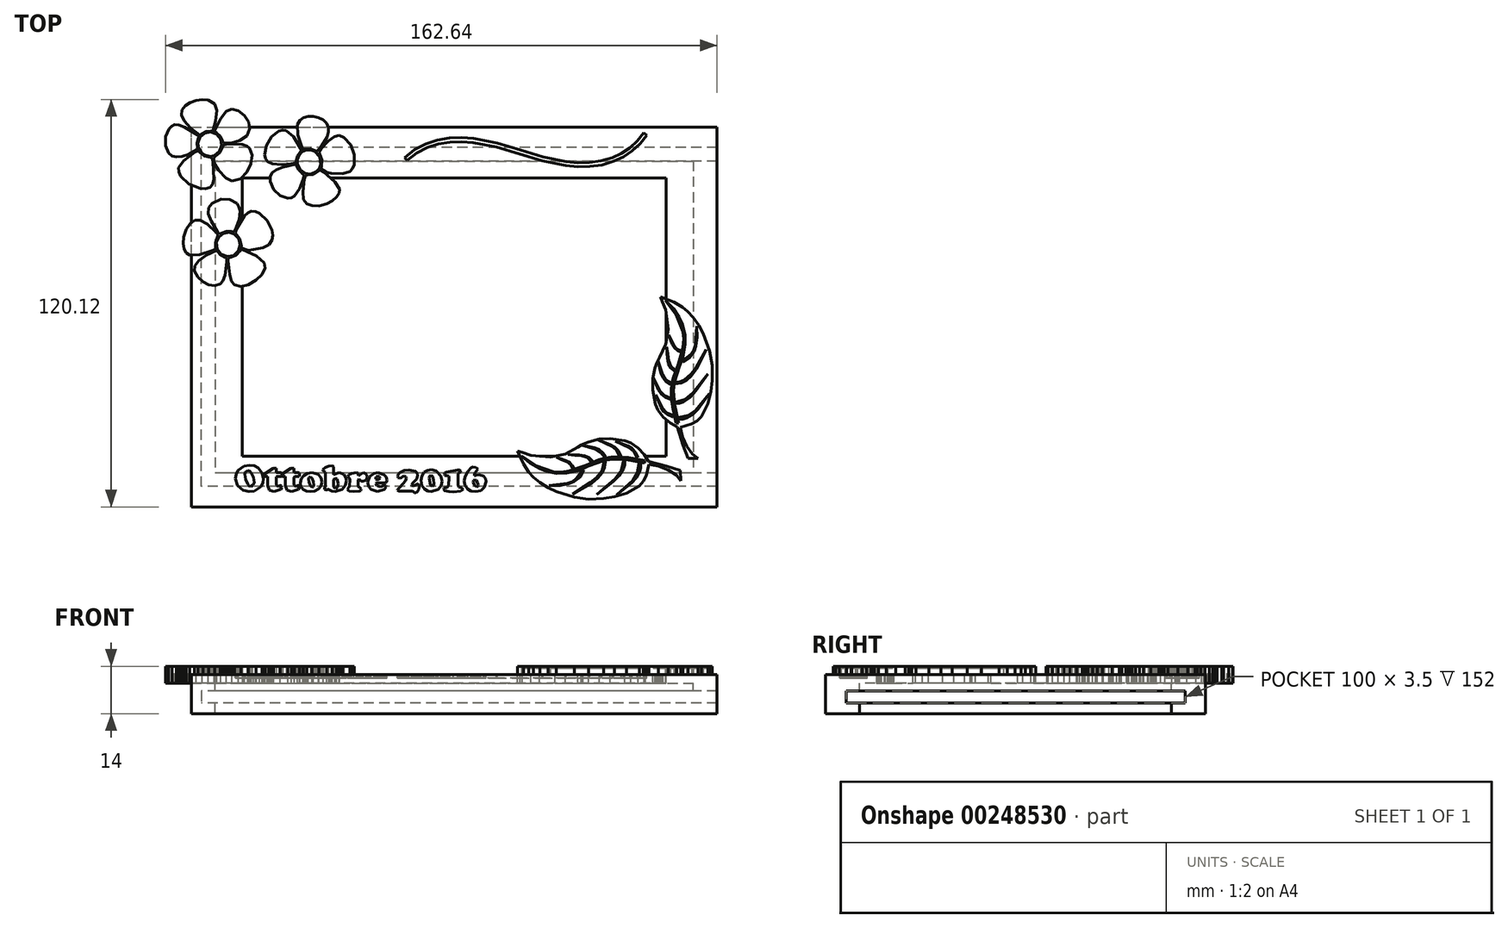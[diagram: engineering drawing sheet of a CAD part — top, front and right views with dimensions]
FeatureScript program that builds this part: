
annotation { "Feature Type Name" : "Feature", "Feature Type Description" : "" }
export const myFeature = defineFeature(function(context is Context, id is Id, definition is map)
    precondition{}
    {
        {
            var Q0;
            Q0=qCreatedBy(makeId("Top.planeOp"),FACE);
            var sketch = newSketch(context, id + "F0", { "sketchPlane" : qUnion([Q0])});
            skLineSegment(sketch, "E0", {"start": v(-50.6, -42.36) * mm, "end": v(-50.6, 49.64) * mm});
            skLineSegment(sketch, "E1", {"start": v(-50.6, 49.64) * mm, "end": v(90.4, 49.64) * mm});
            skLineSegment(sketch, "E2", {"start": v(90.4, 49.64) * mm, "end": v(90.4, -42.36) * mm});
            skLineSegment(sketch, "E3", {"start": v(90.4, -42.36) * mm, "end": v(-50.6, -42.36) * mm});
            skLineSegment(sketch, "E4", {"start": v(97.4, 59.64) * mm, "end": v(97.4, -52.22) * mm});
            skLineSegment(sketch, "E5", {"start": v(97.4, -52.36) * mm, "end": v(-57.31, -52.36) * mm});
            skLineSegment(sketch, "E6", {"start": v(-57.6, -52.22) * mm, "end": v(-57.6, 59.64) * mm});
            skLineSegment(sketch, "E7", {"start": v(-57.6, 59.64) * mm, "end": v(97.4, 59.64) * mm});
            skLineSegment(sketch, "E8", {"start": v(-42.6, 44.64) * mm, "end": v(-42.6, -37.36) * mm});
            skLineSegment(sketch, "E9", {"start": v(-42.6, -37.36) * mm, "end": v(82.4, -37.36) * mm});
            skLineSegment(sketch, "E10", {"start": v(82.4, -37.36) * mm, "end": v(82.4, 44.64) * mm});
            skLineSegment(sketch, "E11", {"start": v(82.4, 44.64) * mm, "end": v(-42.31, 44.64) * mm});
            skLineSegment(sketch, "E12", {"start": v(-57.6, -52.22) * mm, "end": v(-57.6, -52.36) * mm});
            skLineSegment(sketch, "E13", {"start": v(-57.6, -52.36) * mm, "end": v(-57.31, -52.36) * mm});
            skLineSegment(sketch, "E14", {"start": v(97.4, -52.22) * mm, "end": v(97.4, -52.36) * mm});
            skLineSegment(sketch, "E15", {"start": v(-42.31, 44.64) * mm, "end": v(-42.6, 44.64) * mm});
            skLineSegment(sketch, "E16", {"start": v(90.4, -42.36) * mm, "end": v(97.4, -42.36) * mm});
            skLineSegment(sketch, "E17", {"start": v(90.4, 49.64) * mm, "end": v(97.4, 49.64) * mm});
            skSolve(sketch);
        }
        {
            var Q0;
            Q0=makeQuery(id+"F0.imprint","IMPRINT",FACE,{"disambiguationData":[TD([[makeQuery(id+"F0.imprint","IMPRINT",EDGE,{"derivedFrom":sQuery(id+"F0.wireOp",EDGE,"E0")}),-1.0]])]});
            var Q1;
            Q1=makeQuery(id+"F0.imprint","IMPRINT",FACE,{"disambiguationData":[TD([[makeQuery(id+"F0.imprint","IMPRINT",EDGE,{"derivedFrom":sQuery(id+"F0.wireOp",EDGE,"E0")}),1.0]])]});
            var Q2;
            Q2=makeQuery(id+"F0.imprint","IMPRINT",FACE,{"disambiguationData":[TD([[makeQuery(id+"F0.imprint","IMPRINT",EDGE,{"derivedFrom":sQuery(id+"F0.wireOp",EDGE,"E2")}),1.0]])]});
            extrude(context, id + "F1", {"entities" : qUnion([Q0, Q1, Q2]), "depth" : 2.5 * mm});
        }
        {
            var Q0;
            Q0=makeQuery(id+"F0.imprint","IMPRINT",FACE,{"disambiguationData":[TD([[makeQuery(id+"F0.imprint","IMPRINT",EDGE,{"derivedFrom":sQuery(id+"F0.wireOp",EDGE,"E0")}),1.0]])]});
            extrude(context, id + "F2", {"entities" : qUnion([Q0]), "operationType" : NewBodyOperationType.ADD, "oppositeDirection" : true, "depth" : 9 * mm});
        }
        {
            var Q0;
            Q0=makeQuery(id+"F0.imprint","IMPRINT",FACE,{"disambiguationData":[TD([[makeQuery(id+"F0.imprint","IMPRINT",EDGE,{"derivedFrom":sQuery(id+"F0.wireOp",EDGE,"E2")}),1.0]])]});
            extrude(context, id + "F3", {"entities" : qUnion([Q0]), "operationType" : NewBodyOperationType.ADD, "oppositeDirection" : true, "depth" : 2.3 * mm});
        }
        {
            var Q0;
            Q0=makeQuery(id+"F2.opExtrude","SWEPT_FACE",FACE,{"disambiguationData":[OSD([sQuery(id+"F0.wireOp",EDGE,"E3"),sQuery(id+"F0.wireOp",EDGE,"E16")])]});
            var sketch = newSketch(context, id + "F4", { "sketchPlane" : qUnion([Q0])});
            skLineSegment(sketch, "E18.bottom", {"start": v(-97.4, -2.3) * mm, "end": v(54.6, -2.3) * mm});
            skLineSegment(sketch, "E18.top", {"start": v(-97.4, -5.8) * mm, "end": v(54.57, -5.8) * mm});
            skLineSegment(sketch, "E18.left", {"start": v(-97.4, -2.3) * mm, "end": v(-97.4, -5.8) * mm});
            skLineSegment(sketch, "E18.right", {"start": v(54.6, -2.3) * mm, "end": v(54.6, -5.8) * mm});
            skLineSegment(sketch, "E19.bottom", {"start": v(54.6, -5.8) * mm, "end": v(-97.4, -5.8) * mm});
            skLineSegment(sketch, "E19.top", {"start": v(54.6, -2.3) * mm, "end": v(-97.4, -2.3) * mm});
            skLineSegment(sketch, "E19.left", {"start": v(54.6, -5.8) * mm, "end": v(54.6, -2.3) * mm});
            skLineSegment(sketch, "E19.right", {"start": v(-97.4, -5.8) * mm, "end": v(-97.4, -2.3) * mm});
            skSolve(sketch);
        }
        {
            var Q0;
            Q0=makeQuery(id+"F2.opExtrude","SWEPT_FACE",FACE,{"disambiguationData":[OSD([sQuery(id+"F0.wireOp",EDGE,"E1"),sQuery(id+"F0.wireOp",EDGE,"E17")])]});
            var sketch = newSketch(context, id + "F5", { "sketchPlane" : qUnion([Q0])});
            skLineSegment(sketch, "E20.bottom", {"start": v(97.4, -2.3) * mm, "end": v(-54.6, -2.3) * mm});
            skLineSegment(sketch, "E20.top", {"start": v(97.4, -5.8) * mm, "end": v(-54.6, -5.8) * mm});
            skLineSegment(sketch, "E20.left", {"start": v(97.4, -2.3) * mm, "end": v(97.4, -5.8) * mm});
            skLineSegment(sketch, "E20.right", {"start": v(-54.6, -2.3) * mm, "end": v(-54.6, -5.8) * mm});
            skSolve(sketch);
        }
        {
            var Q0;
            Q0 = qSketchRegion(id + "F4", true);
            extrude(context, id + "F6", {"entities" : qUnion([Q0]), "operationType" : NewBodyOperationType.REMOVE, "oppositeDirection" : true, "depth" : 4 * mm});
        }
        {
            var Q0;
            {var subQ0=sQuery(id+"F5.wireOp",EDGE,"E20.right");Q0=makeQuery(id+"F5.imprint","IMPRINT",FACE,{"disambiguationData":[TD([[makeQuery(id+"F5.imprint","IMPRINT",EDGE,{"derivedFrom":subQ0}),1.0]])]});}
            var Q1;
            {var subQ0=sQuery(id+"F5.wireOp",EDGE,"E20.left");Q1=makeQuery(id+"F5.imprint","IMPRINT",FACE,{"disambiguationData":[TD([[makeQuery(id+"F5.imprint","IMPRINT",EDGE,{"derivedFrom":subQ0}),1.0]])]});}
            extrude(context, id + "F7", {"entities" : qUnion([Q0, Q1]), "operationType" : NewBodyOperationType.REMOVE, "oppositeDirection" : true, "depth" : 4 * mm});
        }
        {
            var Q0;
            Q0=makeQuery(id+"F2.opExtrude","SWEPT_FACE",FACE,{"disambiguationData":[OSD([sQuery(id+"F0.wireOp",EDGE,"E0")])]});
            var sketch = newSketch(context, id + "F8", { "sketchPlane" : qUnion([Q0])});
            skLineSegment(sketch, "E21.bottom", {"start": v(49.64, -2.3) * mm, "end": v(-42.36, -2.3) * mm});
            skLineSegment(sketch, "E21.top", {"start": v(49.64, -5.8) * mm, "end": v(-42.36, -5.8) * mm});
            skLineSegment(sketch, "E21.left", {"start": v(49.64, -2.3) * mm, "end": v(49.64, -5.8) * mm});
            skLineSegment(sketch, "E21.right", {"start": v(-42.36, -2.3) * mm, "end": v(-42.36, -5.8) * mm});
            skSolve(sketch);
        }
        {
            var Q0;
            Q0=makeQuery(id+"F8.imprint","IMPRINT",FACE,{"disambiguationData":[TD([[makeQuery(id+"F8.imprint","IMPRINT",EDGE,{"derivedFrom":sQuery(id+"F8.wireOp",EDGE,"E21.bottom")}),1.0]])]});
            extrude(context, id + "F9", {"entities" : qUnion([Q0]), "operationType" : NewBodyOperationType.REMOVE, "oppositeDirection" : true, "depth" : 4 * mm});
        }
        {
            var Q0;
            Q0=makeQuery(id+"F1.opExtrude","CAP_FACE",FACE,{"disambiguationData":[OSD([sQuery(id+"F0.wireOp",EDGE,"E4"),sQuery(id+"F0.wireOp",EDGE,"E5"),sQuery(id+"F0.wireOp",EDGE,"E6"),sQuery(id+"F0.wireOp",EDGE,"E7"),sQuery(id+"F0.wireOp",EDGE,"E8"),sQuery(id+"F0.wireOp",EDGE,"E9"),sQuery(id+"F0.wireOp",EDGE,"E10"),sQuery(id+"F0.wireOp",EDGE,"E11"),sQuery(id+"F0.wireOp",EDGE,"E12"),sQuery(id+"F0.wireOp",EDGE,"E13"),sQuery(id+"F0.wireOp",EDGE,"E14"),sQuery(id+"F0.wireOp",EDGE,"E15")])],"isStart":false});
            var sketch = newSketch(context, id + "F10", { "sketchPlane" : qUnion([Q0])});
            skLineSegment(sketch, "E22", {"start": v(-43.34, 12.36) * mm, "end": v(-44.56, 12.62) * mm});
            skLineSegment(sketch, "E23", {"start": v(-44.56, 12.62) * mm, "end": v(-45.45, 13.22) * mm});
            skLineSegment(sketch, "E24", {"start": v(-45.45, 13.22) * mm, "end": v(-46.62, 15.86) * mm});
            skLineSegment(sketch, "E25", {"start": v(-46.62, 15.86) * mm, "end": v(-46.97, 17.25) * mm});
            skLineSegment(sketch, "E26", {"start": v(-46.97, 17.25) * mm, "end": v(-47.22, 16.26) * mm});
            skLineSegment(sketch, "E27", {"start": v(-47.22, 16.26) * mm, "end": v(-48.3, 13.7) * mm});
            skLineSegment(sketch, "E28", {"start": v(-48.3, 13.7) * mm, "end": v(-49.1, 13.03) * mm});
            skLineSegment(sketch, "E29", {"start": v(-49.1, 13.03) * mm, "end": v(-50.16, 12.66) * mm});
            skLineSegment(sketch, "E30", {"start": v(-50.16, 12.66) * mm, "end": v(-52.63, 12.87) * mm});
            skLineSegment(sketch, "E31", {"start": v(-52.63, 12.87) * mm, "end": v(-54.94, 14.2) * mm});
            skLineSegment(sketch, "E32", {"start": v(-54.94, 14.2) * mm, "end": v(-56.58, 16.2) * mm});
            skLineSegment(sketch, "E33", {"start": v(-56.58, 16.2) * mm, "end": v(-57.03, 18.45) * mm});
            skLineSegment(sketch, "E34", {"start": v(-57.03, 18.45) * mm, "end": v(-56.32, 19.86) * mm});
            skLineSegment(sketch, "E35", {"start": v(-56.32, 19.86) * mm, "end": v(-54.27, 21.6) * mm});
            skLineSegment(sketch, "E36", {"start": v(-54.27, 21.6) * mm, "end": v(-54.18, 21.75) * mm});
            skLineSegment(sketch, "E37", {"start": v(-54.18, 21.75) * mm, "end": v(-55.13, 21.62) * mm});
            skLineSegment(sketch, "E38", {"start": v(-55.13, 21.62) * mm, "end": v(-58.2, 21.58) * mm});
            skLineSegment(sketch, "E39", {"start": v(-58.2, 21.58) * mm, "end": v(-59.42, 22.34) * mm});
            skLineSegment(sketch, "E40", {"start": v(-59.42, 22.34) * mm, "end": v(-60.13, 23.68) * mm});
            skLineSegment(sketch, "E41", {"start": v(-60.13, 23.68) * mm, "end": v(-60.37, 25.4) * mm});
            skLineSegment(sketch, "E42", {"start": v(-60.37, 25.4) * mm, "end": v(-60.18, 27.31) * mm});
            skLineSegment(sketch, "E43", {"start": v(-60.18, 27.31) * mm, "end": v(-59.6, 29.19) * mm});
            skLineSegment(sketch, "E44", {"start": v(-59.6, 29.19) * mm, "end": v(-58.69, 30.83) * mm});
            skLineSegment(sketch, "E45", {"start": v(-58.69, 30.83) * mm, "end": v(-57.46, 32.04) * mm});
            skLineSegment(sketch, "E46", {"start": v(-57.46, 32.04) * mm, "end": v(-55.97, 32.62) * mm});
            skLineSegment(sketch, "E47", {"start": v(-55.97, 32.62) * mm, "end": v(-54.14, 32.17) * mm});
            skLineSegment(sketch, "E48", {"start": v(-54.14, 32.17) * mm, "end": v(-51.85, 30.54) * mm});
            skLineSegment(sketch, "E49", {"start": v(-51.85, 30.54) * mm, "end": v(-51.1, 29.93) * mm});
            skLineSegment(sketch, "E50", {"start": v(-51.1, 29.93) * mm, "end": v(-51.57, 30.85) * mm});
            skLineSegment(sketch, "E51", {"start": v(-51.57, 30.85) * mm, "end": v(-52.74, 33.3) * mm});
            skLineSegment(sketch, "E52", {"start": v(-52.74, 33.3) * mm, "end": v(-53.03, 35.08) * mm});
            skLineSegment(sketch, "E53", {"start": v(-53.03, 35.08) * mm, "end": v(-52.68, 36.16) * mm});
            skLineSegment(sketch, "E54", {"start": v(-52.68, 36.16) * mm, "end": v(-51.98, 37.1) * mm});
            skLineSegment(sketch, "E55", {"start": v(-51.98, 37.1) * mm, "end": v(-49.88, 38.4) * mm});
            skLineSegment(sketch, "E56", {"start": v(-49.88, 38.4) * mm, "end": v(-47.29, 38.79) * mm});
            skLineSegment(sketch, "E57", {"start": v(-47.29, 38.79) * mm, "end": v(-44.81, 38.05) * mm});
            skLineSegment(sketch, "E58", {"start": v(-44.81, 38.05) * mm, "end": v(-43.79, 37.16) * mm});
            skLineSegment(sketch, "E59", {"start": v(-43.79, 37.16) * mm, "end": v(-43.16, 36) * mm});
            skLineSegment(sketch, "E60", {"start": v(-43.16, 36) * mm, "end": v(-42.94, 34.58) * mm});
            skLineSegment(sketch, "E61", {"start": v(-42.94, 34.58) * mm, "end": v(-43.12, 32.88) * mm});
            skLineSegment(sketch, "E62", {"start": v(-43.12, 32.88) * mm, "end": v(-43.13, 32.45) * mm});
            skLineSegment(sketch, "E63", {"start": v(-43.13, 32.45) * mm, "end": v(-42.7, 32.97) * mm});
            skLineSegment(sketch, "E64", {"start": v(-42.7, 32.97) * mm, "end": v(-41.54, 34.37) * mm});
            skLineSegment(sketch, "E65", {"start": v(-41.54, 34.37) * mm, "end": v(-40.34, 35.1) * mm});
            skLineSegment(sketch, "E66", {"start": v(-40.34, 35.1) * mm, "end": v(-39.05, 35.17) * mm});
            skLineSegment(sketch, "E67", {"start": v(-39.05, 35.17) * mm, "end": v(-37.57, 34.63) * mm});
            skLineSegment(sketch, "E68", {"start": v(-37.57, 34.63) * mm, "end": v(-35.67, 33.07) * mm});
            skLineSegment(sketch, "E69", {"start": v(-35.67, 33.07) * mm, "end": v(-34.1, 30.87) * mm});
            skLineSegment(sketch, "E70", {"start": v(-34.1, 30.87) * mm, "end": v(-33.47, 28.96) * mm});
            skLineSegment(sketch, "E71", {"start": v(-33.47, 28.96) * mm, "end": v(-33.27, 27.17) * mm});
            skLineSegment(sketch, "E72", {"start": v(-33.27, 27.17) * mm, "end": v(-33.68, 25.67) * mm});
            skLineSegment(sketch, "E73", {"start": v(-33.68, 25.67) * mm, "end": v(-34.55, 24.6) * mm});
            skLineSegment(sketch, "E74", {"start": v(-34.55, 24.6) * mm, "end": v(-36.05, 23.87) * mm});
            skLineSegment(sketch, "E75", {"start": v(-36.05, 23.87) * mm, "end": v(-38.36, 23.31) * mm});
            skLineSegment(sketch, "E76", {"start": v(-38.36, 23.31) * mm, "end": v(-40.2, 22.94) * mm});
            skLineSegment(sketch, "E77", {"start": v(-40.2, 22.94) * mm, "end": v(-39.3, 22.45) * mm});
            skLineSegment(sketch, "E78", {"start": v(-39.3, 22.45) * mm, "end": v(-36.3, 20.38) * mm});
            skLineSegment(sketch, "E79", {"start": v(-36.3, 20.38) * mm, "end": v(-35.66, 19.35) * mm});
            skLineSegment(sketch, "E80", {"start": v(-35.66, 19.35) * mm, "end": v(-35.54, 18.28) * mm});
            skLineSegment(sketch, "E81", {"start": v(-35.54, 18.28) * mm, "end": v(-36.46, 16.1) * mm});
            skLineSegment(sketch, "E82", {"start": v(-36.46, 16.1) * mm, "end": v(-38.38, 14.15) * mm});
            skLineSegment(sketch, "E83", {"start": v(-38.38, 14.15) * mm, "end": v(-40.84, 12.78) * mm});
            skLineSegment(sketch, "E84", {"start": v(-40.84, 12.78) * mm, "end": v(-43.34, 12.36) * mm});
            skLineSegment(sketch, "E85", {"start": v(-43.34, 12.36) * mm, "end": v(-43.34, 12.36) * mm});
            skLineSegment(sketch, "E86", {"start": v(-40.74, 13.15) * mm, "end": v(-38.48, 14.47) * mm});
            skLineSegment(sketch, "E87", {"start": v(-38.48, 14.47) * mm, "end": v(-36.79, 16.2) * mm});
            skLineSegment(sketch, "E88", {"start": v(-36.79, 16.2) * mm, "end": v(-35.9, 18.02) * mm});
            skLineSegment(sketch, "E89", {"start": v(-35.9, 18.02) * mm, "end": v(-36.06, 19.6) * mm});
            skLineSegment(sketch, "E90", {"start": v(-36.06, 19.6) * mm, "end": v(-38.45, 21.6) * mm});
            skLineSegment(sketch, "E91", {"start": v(-38.45, 21.6) * mm, "end": v(-42.61, 23.57) * mm});
            skLineSegment(sketch, "E92", {"start": v(-42.61, 23.57) * mm, "end": v(-42.98, 23.7) * mm});
            skLineSegment(sketch, "E93", {"start": v(-42.98, 23.7) * mm, "end": v(-43.4, 23.02) * mm});
            skLineSegment(sketch, "E94", {"start": v(-43.4, 23.02) * mm, "end": v(-44.4, 21.86) * mm});
            skLineSegment(sketch, "E95", {"start": v(-44.4, 21.86) * mm, "end": v(-45.86, 21.25) * mm});
            skLineSegment(sketch, "E96", {"start": v(-45.86, 21.25) * mm, "end": v(-46.82, 21.02) * mm});
            skLineSegment(sketch, "E97", {"start": v(-46.82, 21.02) * mm, "end": v(-46.8, 20.23) * mm});
            skLineSegment(sketch, "E98", {"start": v(-46.8, 20.23) * mm, "end": v(-46.32, 16.21) * mm});
            skLineSegment(sketch, "E99", {"start": v(-46.32, 16.21) * mm, "end": v(-45.73, 14.1) * mm});
            skLineSegment(sketch, "E100", {"start": v(-45.73, 14.1) * mm, "end": v(-44.87, 13.2) * mm});
            skLineSegment(sketch, "E101", {"start": v(-44.87, 13.2) * mm, "end": v(-43, 12.67) * mm});
            skLineSegment(sketch, "E102", {"start": v(-43, 12.67) * mm, "end": v(-40.74, 13.15) * mm});
            skLineSegment(sketch, "E103", {"start": v(-40.74, 13.15) * mm, "end": v(-40.74, 13.15) * mm});
            skLineSegment(sketch, "E104", {"start": v(-49.1, 13.41) * mm, "end": v(-48.28, 14.34) * mm});
            skLineSegment(sketch, "E105", {"start": v(-48.28, 14.34) * mm, "end": v(-47.63, 15.87) * mm});
            skLineSegment(sketch, "E106", {"start": v(-47.63, 15.87) * mm, "end": v(-47.1, 19.88) * mm});
            skLineSegment(sketch, "E107", {"start": v(-47.1, 19.88) * mm, "end": v(-47.19, 21) * mm});
            skLineSegment(sketch, "E108", {"start": v(-47.19, 21) * mm, "end": v(-47.69, 21.26) * mm});
            skLineSegment(sketch, "E109", {"start": v(-47.69, 21.26) * mm, "end": v(-49.2, 22.12) * mm});
            skLineSegment(sketch, "E110", {"start": v(-49.2, 22.12) * mm, "end": v(-50.1, 23.25) * mm});
            skLineSegment(sketch, "E111", {"start": v(-50.1, 23.25) * mm, "end": v(-53.17, 21.87) * mm});
            skLineSegment(sketch, "E112", {"start": v(-53.17, 21.87) * mm, "end": v(-55.45, 20.28) * mm});
            skLineSegment(sketch, "E113", {"start": v(-55.45, 20.28) * mm, "end": v(-56.6, 18.76) * mm});
            skLineSegment(sketch, "E114", {"start": v(-56.6, 18.76) * mm, "end": v(-56.68, 17.2) * mm});
            skLineSegment(sketch, "E115", {"start": v(-56.68, 17.2) * mm, "end": v(-55.73, 15.48) * mm});
            skLineSegment(sketch, "E116", {"start": v(-55.73, 15.48) * mm, "end": v(-54.2, 14.02) * mm});
            skLineSegment(sketch, "E117", {"start": v(-54.2, 14.02) * mm, "end": v(-52.44, 13.15) * mm});
            skLineSegment(sketch, "E118", {"start": v(-52.44, 13.15) * mm, "end": v(-50.68, 12.92) * mm});
            skLineSegment(sketch, "E119", {"start": v(-50.68, 12.92) * mm, "end": v(-49.1, 13.41) * mm});
            skLineSegment(sketch, "E120", {"start": v(-45.15, 21.8) * mm, "end": v(-43.7, 23.13) * mm});
            skLineSegment(sketch, "E121", {"start": v(-43.7, 23.13) * mm, "end": v(-43.17, 24.9) * mm});
            skLineSegment(sketch, "E122", {"start": v(-43.17, 24.9) * mm, "end": v(-43.59, 26.7) * mm});
            skLineSegment(sketch, "E123", {"start": v(-43.59, 26.7) * mm, "end": v(-44.96, 28.14) * mm});
            skLineSegment(sketch, "E124", {"start": v(-44.96, 28.14) * mm, "end": v(-46.58, 28.61) * mm});
            skLineSegment(sketch, "E125", {"start": v(-46.58, 28.61) * mm, "end": v(-48.2, 28.27) * mm});
            skLineSegment(sketch, "E126", {"start": v(-48.2, 28.27) * mm, "end": v(-49.5, 27.25) * mm});
            skLineSegment(sketch, "E127", {"start": v(-49.5, 27.25) * mm, "end": v(-50.18, 25.69) * mm});
            skLineSegment(sketch, "E128", {"start": v(-50.18, 25.69) * mm, "end": v(-49.95, 23.69) * mm});
            skLineSegment(sketch, "E129", {"start": v(-49.95, 23.69) * mm, "end": v(-48.79, 22.19) * mm});
            skLineSegment(sketch, "E130", {"start": v(-48.79, 22.19) * mm, "end": v(-47.07, 21.47) * mm});
            skLineSegment(sketch, "E131", {"start": v(-47.07, 21.47) * mm, "end": v(-45.15, 21.8) * mm});
            skLineSegment(sketch, "E132", {"start": v(-36.53, 24.04) * mm, "end": v(-34.66, 24.94) * mm});
            skLineSegment(sketch, "E133", {"start": v(-34.66, 24.94) * mm, "end": v(-33.79, 26.31) * mm});
            skLineSegment(sketch, "E134", {"start": v(-33.79, 26.31) * mm, "end": v(-33.6, 27.72) * mm});
            skLineSegment(sketch, "E135", {"start": v(-33.6, 27.72) * mm, "end": v(-33.82, 29.2) * mm});
            skLineSegment(sketch, "E136", {"start": v(-33.82, 29.2) * mm, "end": v(-35.22, 32.07) * mm});
            skLineSegment(sketch, "E137", {"start": v(-35.22, 32.07) * mm, "end": v(-37.45, 34.18) * mm});
            skLineSegment(sketch, "E138", {"start": v(-37.45, 34.18) * mm, "end": v(-38.7, 34.73) * mm});
            skLineSegment(sketch, "E139", {"start": v(-38.7, 34.73) * mm, "end": v(-39.98, 34.8) * mm});
            skLineSegment(sketch, "E140", {"start": v(-39.98, 34.8) * mm, "end": v(-40.97, 34.4) * mm});
            skLineSegment(sketch, "E141", {"start": v(-40.97, 34.4) * mm, "end": v(-41.98, 33.43) * mm});
            skLineSegment(sketch, "E142", {"start": v(-41.98, 33.43) * mm, "end": v(-44.19, 29.65) * mm});
            skLineSegment(sketch, "E143", {"start": v(-44.19, 29.65) * mm, "end": v(-44.66, 28.55) * mm});
            skLineSegment(sketch, "E144", {"start": v(-44.66, 28.55) * mm, "end": v(-44.5, 28.24) * mm});
            skLineSegment(sketch, "E145", {"start": v(-44.5, 28.24) * mm, "end": v(-43.3, 26.78) * mm});
            skLineSegment(sketch, "E146", {"start": v(-43.3, 26.78) * mm, "end": v(-42.87, 24.64) * mm});
            skLineSegment(sketch, "E147", {"start": v(-42.87, 24.64) * mm, "end": v(-42.86, 24.04) * mm});
            skLineSegment(sketch, "E148", {"start": v(-42.86, 24.04) * mm, "end": v(-41.98, 23.68) * mm});
            skLineSegment(sketch, "E149", {"start": v(-41.98, 23.68) * mm, "end": v(-40.82, 23.35) * mm});
            skLineSegment(sketch, "E150", {"start": v(-40.82, 23.35) * mm, "end": v(-39.23, 23.48) * mm});
            skLineSegment(sketch, "E151", {"start": v(-39.23, 23.48) * mm, "end": v(-36.53, 24.04) * mm});
            skLineSegment(sketch, "E152", {"start": v(-36.53, 24.04) * mm, "end": v(-36.53, 24.04) * mm});
            skLineSegment(sketch, "E153", {"start": v(-51.58, 23.12) * mm, "end": v(-50.39, 23.72) * mm});
            skLineSegment(sketch, "E154", {"start": v(-50.39, 23.72) * mm, "end": v(-50.45, 24.04) * mm});
            skLineSegment(sketch, "E155", {"start": v(-50.45, 24.04) * mm, "end": v(-50.5, 25.63) * mm});
            skLineSegment(sketch, "E156", {"start": v(-50.5, 25.63) * mm, "end": v(-49.97, 27.08) * mm});
            skLineSegment(sketch, "E157", {"start": v(-49.97, 27.08) * mm, "end": v(-49.67, 27.81) * mm});
            skLineSegment(sketch, "E158", {"start": v(-49.67, 27.81) * mm, "end": v(-50.35, 28.65) * mm});
            skLineSegment(sketch, "E159", {"start": v(-50.35, 28.65) * mm, "end": v(-52.93, 31) * mm});
            skLineSegment(sketch, "E160", {"start": v(-52.93, 31) * mm, "end": v(-54.99, 32.2) * mm});
            skLineSegment(sketch, "E161", {"start": v(-54.99, 32.2) * mm, "end": v(-56.52, 32.14) * mm});
            skLineSegment(sketch, "E162", {"start": v(-56.52, 32.14) * mm, "end": v(-57.97, 31.18) * mm});
            skLineSegment(sketch, "E163", {"start": v(-57.97, 31.18) * mm, "end": v(-59.14, 29.48) * mm});
            skLineSegment(sketch, "E164", {"start": v(-59.14, 29.48) * mm, "end": v(-59.89, 27.22) * mm});
            skLineSegment(sketch, "E165", {"start": v(-59.89, 27.22) * mm, "end": v(-60.04, 25.31) * mm});
            skLineSegment(sketch, "E166", {"start": v(-60.04, 25.31) * mm, "end": v(-59.77, 23.7) * mm});
            skLineSegment(sketch, "E167", {"start": v(-59.77, 23.7) * mm, "end": v(-59.13, 22.51) * mm});
            skLineSegment(sketch, "E168", {"start": v(-59.13, 22.51) * mm, "end": v(-58.14, 21.87) * mm});
            skLineSegment(sketch, "E169", {"start": v(-58.14, 21.87) * mm, "end": v(-55.11, 21.96) * mm});
            skLineSegment(sketch, "E170", {"start": v(-55.11, 21.96) * mm, "end": v(-51.58, 23.12) * mm});
            skLineSegment(sketch, "E171", {"start": v(-44.4, 29.96) * mm, "end": v(-43.52, 32.5) * mm});
            skLineSegment(sketch, "E172", {"start": v(-43.52, 32.5) * mm, "end": v(-43.28, 35.02) * mm});
            skLineSegment(sketch, "E173", {"start": v(-43.28, 35.02) * mm, "end": v(-43.54, 36.18) * mm});
            skLineSegment(sketch, "E174", {"start": v(-43.54, 36.18) * mm, "end": v(-44.17, 37.12) * mm});
            skLineSegment(sketch, "E175", {"start": v(-44.17, 37.12) * mm, "end": v(-46.22, 38.3) * mm});
            skLineSegment(sketch, "E176", {"start": v(-46.22, 38.3) * mm, "end": v(-48.84, 38.36) * mm});
            skLineSegment(sketch, "E177", {"start": v(-48.84, 38.36) * mm, "end": v(-51.42, 37.18) * mm});
            skLineSegment(sketch, "E178", {"start": v(-51.42, 37.18) * mm, "end": v(-52.5, 35.85) * mm});
            skLineSegment(sketch, "E179", {"start": v(-52.5, 35.85) * mm, "end": v(-52.63, 34.15) * mm});
            skLineSegment(sketch, "E180", {"start": v(-52.63, 34.15) * mm, "end": v(-51.78, 31.89) * mm});
            skLineSegment(sketch, "E181", {"start": v(-51.78, 31.89) * mm, "end": v(-49.93, 28.87) * mm});
            skLineSegment(sketch, "E182", {"start": v(-49.93, 28.87) * mm, "end": v(-49.33, 28.13) * mm});
            skLineSegment(sketch, "E183", {"start": v(-49.33, 28.13) * mm, "end": v(-48.74, 28.36) * mm});
            skLineSegment(sketch, "E184", {"start": v(-48.74, 28.36) * mm, "end": v(-47.29, 28.92) * mm});
            skLineSegment(sketch, "E185", {"start": v(-47.29, 28.92) * mm, "end": v(-45.77, 28.82) * mm});
            skLineSegment(sketch, "E186", {"start": v(-45.77, 28.82) * mm, "end": v(-45.05, 28.8) * mm});
            skLineSegment(sketch, "E187", {"start": v(-45.05, 28.8) * mm, "end": v(-44.4, 29.96) * mm});
            skLineSegment(sketch, "E188", {"start": v(-44.4, 29.96) * mm, "end": v(-44.4, 29.96) * mm});
            skLineSegment(sketch, "E189", {"start": v(-20.43, 36.02) * mm, "end": v(-22.8, 36.34) * mm});
            skLineSegment(sketch, "E190", {"start": v(-22.8, 36.34) * mm, "end": v(-24.44, 37.43) * mm});
            skLineSegment(sketch, "E191", {"start": v(-24.44, 37.43) * mm, "end": v(-25, 39.14) * mm});
            skLineSegment(sketch, "E192", {"start": v(-25, 39.14) * mm, "end": v(-25.02, 41.53) * mm});
            skLineSegment(sketch, "E193", {"start": v(-25.02, 41.53) * mm, "end": v(-25.05, 41.87) * mm});
            skLineSegment(sketch, "E194", {"start": v(-25.05, 41.87) * mm, "end": v(-25.5, 41.08) * mm});
            skLineSegment(sketch, "E195", {"start": v(-25.5, 41.08) * mm, "end": v(-26.76, 39.28) * mm});
            skLineSegment(sketch, "E196", {"start": v(-26.76, 39.28) * mm, "end": v(-28.2, 38.37) * mm});
            skLineSegment(sketch, "E197", {"start": v(-28.2, 38.37) * mm, "end": v(-29.84, 38.34) * mm});
            skLineSegment(sketch, "E198", {"start": v(-29.84, 38.34) * mm, "end": v(-31.68, 39.2) * mm});
            skLineSegment(sketch, "E199", {"start": v(-31.68, 39.2) * mm, "end": v(-33.33, 40.7) * mm});
            skLineSegment(sketch, "E200", {"start": v(-33.33, 40.7) * mm, "end": v(-34.4, 42.49) * mm});
            skLineSegment(sketch, "E201", {"start": v(-34.4, 42.49) * mm, "end": v(-34.77, 44.32) * mm});
            skLineSegment(sketch, "E202", {"start": v(-34.77, 44.32) * mm, "end": v(-34.36, 45.95) * mm});
            skLineSegment(sketch, "E203", {"start": v(-34.36, 45.95) * mm, "end": v(-33.02, 47.11) * mm});
            skLineSegment(sketch, "E204", {"start": v(-33.02, 47.11) * mm, "end": v(-31.14, 47.93) * mm});
            skLineSegment(sketch, "E205", {"start": v(-31.14, 47.93) * mm, "end": v(-30.94, 48.1) * mm});
            skLineSegment(sketch, "E206", {"start": v(-30.94, 48.1) * mm, "end": v(-31.99, 48.25) * mm});
            skLineSegment(sketch, "E207", {"start": v(-31.99, 48.25) * mm, "end": v(-33.83, 48.53) * mm});
            skLineSegment(sketch, "E208", {"start": v(-33.83, 48.53) * mm, "end": v(-35.08, 49.04) * mm});
            skLineSegment(sketch, "E209", {"start": v(-35.08, 49.04) * mm, "end": v(-35.82, 49.85) * mm});
            skLineSegment(sketch, "E210", {"start": v(-35.82, 49.85) * mm, "end": v(-36.18, 51.05) * mm});
            skLineSegment(sketch, "E211", {"start": v(-36.18, 51.05) * mm, "end": v(-36.18, 52.66) * mm});
            skLineSegment(sketch, "E212", {"start": v(-36.18, 52.66) * mm, "end": v(-35.77, 54.27) * mm});
            skLineSegment(sketch, "E213", {"start": v(-35.77, 54.27) * mm, "end": v(-34.03, 57.12) * mm});
            skLineSegment(sketch, "E214", {"start": v(-34.03, 57.12) * mm, "end": v(-31.62, 58.87) * mm});
            skLineSegment(sketch, "E215", {"start": v(-31.62, 58.87) * mm, "end": v(-30.37, 59.1) * mm});
            skLineSegment(sketch, "E216", {"start": v(-30.37, 59.1) * mm, "end": v(-29.2, 58.8) * mm});
            skLineSegment(sketch, "E217", {"start": v(-29.2, 58.8) * mm, "end": v(-27.76, 57.55) * mm});
            skLineSegment(sketch, "E218", {"start": v(-27.76, 57.55) * mm, "end": v(-26.3, 55.66) * mm});
            skLineSegment(sketch, "E219", {"start": v(-26.3, 55.66) * mm, "end": v(-26, 55.3) * mm});
            skLineSegment(sketch, "E220", {"start": v(-26, 55.3) * mm, "end": v(-26.04, 55.62) * mm});
            skLineSegment(sketch, "E221", {"start": v(-26.04, 55.62) * mm, "end": v(-26.79, 59.6) * mm});
            skLineSegment(sketch, "E222", {"start": v(-26.79, 59.6) * mm, "end": v(-26.54, 60.73) * mm});
            skLineSegment(sketch, "E223", {"start": v(-26.54, 60.73) * mm, "end": v(-25.93, 61.67) * mm});
            skLineSegment(sketch, "E224", {"start": v(-25.93, 61.67) * mm, "end": v(-23.91, 62.9) * mm});
            skLineSegment(sketch, "E225", {"start": v(-23.91, 62.9) * mm, "end": v(-21.3, 63.11) * mm});
            skLineSegment(sketch, "E226", {"start": v(-21.3, 63.11) * mm, "end": v(-18.65, 62.13) * mm});
            skLineSegment(sketch, "E227", {"start": v(-18.65, 62.13) * mm, "end": v(-17.48, 61.07) * mm});
            skLineSegment(sketch, "E228", {"start": v(-17.48, 61.07) * mm, "end": v(-16.87, 59.8) * mm});
            skLineSegment(sketch, "E229", {"start": v(-16.87, 59.8) * mm, "end": v(-16.83, 58.3) * mm});
            skLineSegment(sketch, "E230", {"start": v(-16.83, 58.3) * mm, "end": v(-17.34, 56.5) * mm});
            skLineSegment(sketch, "E231", {"start": v(-17.34, 56.5) * mm, "end": v(-17.67, 55.62) * mm});
            skLineSegment(sketch, "E232", {"start": v(-17.67, 55.62) * mm, "end": v(-16.83, 56.26) * mm});
            skLineSegment(sketch, "E233", {"start": v(-16.83, 56.26) * mm, "end": v(-14.5, 57.5) * mm});
            skLineSegment(sketch, "E234", {"start": v(-14.5, 57.5) * mm, "end": v(-13.13, 57.31) * mm});
            skLineSegment(sketch, "E235", {"start": v(-13.13, 57.31) * mm, "end": v(-11.88, 56.53) * mm});
            skLineSegment(sketch, "E236", {"start": v(-11.88, 56.53) * mm, "end": v(-9.9, 53.74) * mm});
            skLineSegment(sketch, "E237", {"start": v(-9.9, 53.74) * mm, "end": v(-9.07, 50.24) * mm});
            skLineSegment(sketch, "E238", {"start": v(-9.07, 50.24) * mm, "end": v(-9.23, 48.56) * mm});
            skLineSegment(sketch, "E239", {"start": v(-9.23, 48.56) * mm, "end": v(-9.86, 47.11) * mm});
            skLineSegment(sketch, "E240", {"start": v(-9.86, 47.11) * mm, "end": v(-10.74, 46.2) * mm});
            skLineSegment(sketch, "E241", {"start": v(-10.74, 46.2) * mm, "end": v(-11.94, 45.67) * mm});
            skLineSegment(sketch, "E242", {"start": v(-11.94, 45.67) * mm, "end": v(-15.95, 45.68) * mm});
            skLineSegment(sketch, "E243", {"start": v(-15.95, 45.68) * mm, "end": v(-17.03, 45.75) * mm});
            skLineSegment(sketch, "E244", {"start": v(-17.03, 45.75) * mm, "end": v(-16.3, 44.98) * mm});
            skLineSegment(sketch, "E245", {"start": v(-16.3, 44.98) * mm, "end": v(-14.6, 43.25) * mm});
            skLineSegment(sketch, "E246", {"start": v(-14.6, 43.25) * mm, "end": v(-13.7, 41.79) * mm});
            skLineSegment(sketch, "E247", {"start": v(-13.7, 41.79) * mm, "end": v(-13.57, 40.47) * mm});
            skLineSegment(sketch, "E248", {"start": v(-13.57, 40.47) * mm, "end": v(-14.17, 39.17) * mm});
            skLineSegment(sketch, "E249", {"start": v(-14.17, 39.17) * mm, "end": v(-15.32, 38.03) * mm});
            skLineSegment(sketch, "E250", {"start": v(-15.32, 38.03) * mm, "end": v(-16.9, 37.04) * mm});
            skLineSegment(sketch, "E251", {"start": v(-16.9, 37.04) * mm, "end": v(-18.68, 36.33) * mm});
            skLineSegment(sketch, "E252", {"start": v(-18.68, 36.33) * mm, "end": v(-20.43, 36.02) * mm});
            skLineSegment(sketch, "E253", {"start": v(-17.74, 37) * mm, "end": v(-16, 37.9) * mm});
            skLineSegment(sketch, "E254", {"start": v(-16, 37.9) * mm, "end": v(-14.73, 39) * mm});
            skLineSegment(sketch, "E255", {"start": v(-14.73, 39) * mm, "end": v(-14, 40.19) * mm});
            skLineSegment(sketch, "E256", {"start": v(-14, 40.19) * mm, "end": v(-13.9, 41.36) * mm});
            skLineSegment(sketch, "E257", {"start": v(-13.9, 41.36) * mm, "end": v(-15.27, 43.54) * mm});
            skLineSegment(sketch, "E258", {"start": v(-15.27, 43.54) * mm, "end": v(-18.61, 46.46) * mm});
            skLineSegment(sketch, "E259", {"start": v(-18.61, 46.46) * mm, "end": v(-19.55, 47.1) * mm});
            skLineSegment(sketch, "E260", {"start": v(-19.55, 47.1) * mm, "end": v(-20.04, 46.74) * mm});
            skLineSegment(sketch, "E261", {"start": v(-20.04, 46.74) * mm, "end": v(-21.61, 45.7) * mm});
            skLineSegment(sketch, "E262", {"start": v(-21.61, 45.7) * mm, "end": v(-23.39, 45.5) * mm});
            skLineSegment(sketch, "E263", {"start": v(-23.39, 45.5) * mm, "end": v(-23.96, 45.44) * mm});
            skLineSegment(sketch, "E264", {"start": v(-23.96, 45.44) * mm, "end": v(-24.28, 44.18) * mm});
            skLineSegment(sketch, "E265", {"start": v(-24.28, 44.18) * mm, "end": v(-24.73, 40.6) * mm});
            skLineSegment(sketch, "E266", {"start": v(-24.73, 40.6) * mm, "end": v(-24.49, 38.22) * mm});
            skLineSegment(sketch, "E267", {"start": v(-24.49, 38.22) * mm, "end": v(-23.55, 37.06) * mm});
            skLineSegment(sketch, "E268", {"start": v(-23.55, 37.06) * mm, "end": v(-21.97, 36.44) * mm});
            skLineSegment(sketch, "E269", {"start": v(-21.97, 36.44) * mm, "end": v(-19.96, 36.41) * mm});
            skLineSegment(sketch, "E270", {"start": v(-19.96, 36.41) * mm, "end": v(-17.74, 37) * mm});
            skLineSegment(sketch, "E271", {"start": v(-27.2, 39.24) * mm, "end": v(-25.64, 41.51) * mm});
            skLineSegment(sketch, "E272", {"start": v(-25.64, 41.51) * mm, "end": v(-24.54, 44.55) * mm});
            skLineSegment(sketch, "E273", {"start": v(-24.54, 44.55) * mm, "end": v(-24.3, 45.68) * mm});
            skLineSegment(sketch, "E274", {"start": v(-24.3, 45.68) * mm, "end": v(-24.9, 46.06) * mm});
            skLineSegment(sketch, "E275", {"start": v(-24.9, 46.06) * mm, "end": v(-25.9, 47) * mm});
            skLineSegment(sketch, "E276", {"start": v(-25.9, 47) * mm, "end": v(-26.53, 48.15) * mm});
            skLineSegment(sketch, "E277", {"start": v(-26.53, 48.15) * mm, "end": v(-26.8, 48.67) * mm});
            skLineSegment(sketch, "E278", {"start": v(-26.8, 48.67) * mm, "end": v(-30.59, 47.77) * mm});
            skLineSegment(sketch, "E279", {"start": v(-30.59, 47.77) * mm, "end": v(-32.62, 46.98) * mm});
            skLineSegment(sketch, "E280", {"start": v(-32.62, 46.98) * mm, "end": v(-33.84, 46.12) * mm});
            skLineSegment(sketch, "E281", {"start": v(-33.84, 46.12) * mm, "end": v(-34.38, 45.05) * mm});
            skLineSegment(sketch, "E282", {"start": v(-34.38, 45.05) * mm, "end": v(-34.36, 43.65) * mm});
            skLineSegment(sketch, "E283", {"start": v(-34.36, 43.65) * mm, "end": v(-33.3, 41.16) * mm});
            skLineSegment(sketch, "E284", {"start": v(-33.3, 41.16) * mm, "end": v(-31.38, 39.37) * mm});
            skLineSegment(sketch, "E285", {"start": v(-31.38, 39.37) * mm, "end": v(-29.16, 38.62) * mm});
            skLineSegment(sketch, "E286", {"start": v(-29.16, 38.62) * mm, "end": v(-28.12, 38.74) * mm});
            skLineSegment(sketch, "E287", {"start": v(-28.12, 38.74) * mm, "end": v(-27.2, 39.24) * mm});
            skLineSegment(sketch, "E288", {"start": v(-10.83, 46.47) * mm, "end": v(-10.04, 47.38) * mm});
            skLineSegment(sketch, "E289", {"start": v(-10.04, 47.38) * mm, "end": v(-9.57, 48.59) * mm});
            skLineSegment(sketch, "E290", {"start": v(-9.57, 48.59) * mm, "end": v(-9.53, 51.48) * mm});
            skLineSegment(sketch, "E291", {"start": v(-9.53, 51.48) * mm, "end": v(-10.56, 54.4) * mm});
            skLineSegment(sketch, "E292", {"start": v(-10.56, 54.4) * mm, "end": v(-12.55, 56.62) * mm});
            skLineSegment(sketch, "E293", {"start": v(-12.55, 56.62) * mm, "end": v(-13.96, 57.15) * mm});
            skLineSegment(sketch, "E294", {"start": v(-13.96, 57.15) * mm, "end": v(-15.46, 56.8) * mm});
            skLineSegment(sketch, "E295", {"start": v(-15.46, 56.8) * mm, "end": v(-17.2, 55.52) * mm});
            skLineSegment(sketch, "E296", {"start": v(-17.2, 55.52) * mm, "end": v(-19.36, 53.2) * mm});
            skLineSegment(sketch, "E297", {"start": v(-19.36, 53.2) * mm, "end": v(-20.04, 52.26) * mm});
            skLineSegment(sketch, "E298", {"start": v(-20.04, 52.26) * mm, "end": v(-19.75, 51.6) * mm});
            skLineSegment(sketch, "E299", {"start": v(-19.75, 51.6) * mm, "end": v(-19.1, 49.9) * mm});
            skLineSegment(sketch, "E300", {"start": v(-19.1, 49.9) * mm, "end": v(-19.25, 48.1) * mm});
            skLineSegment(sketch, "E301", {"start": v(-19.25, 48.1) * mm, "end": v(-19.34, 47.5) * mm});
            skLineSegment(sketch, "E302", {"start": v(-19.34, 47.5) * mm, "end": v(-18.65, 46.88) * mm});
            skLineSegment(sketch, "E303", {"start": v(-18.65, 46.88) * mm, "end": v(-17.74, 46.3) * mm});
            skLineSegment(sketch, "E304", {"start": v(-17.74, 46.3) * mm, "end": v(-16.44, 46.06) * mm});
            skLineSegment(sketch, "E305", {"start": v(-16.44, 46.06) * mm, "end": v(-12.94, 45.89) * mm});
            skLineSegment(sketch, "E306", {"start": v(-12.94, 45.89) * mm, "end": v(-10.83, 46.47) * mm});
            skLineSegment(sketch, "E307", {"start": v(-20.76, 46.52) * mm, "end": v(-19.88, 47.48) * mm});
            skLineSegment(sketch, "E308", {"start": v(-19.88, 47.48) * mm, "end": v(-19.44, 48.59) * mm});
            skLineSegment(sketch, "E309", {"start": v(-19.44, 48.59) * mm, "end": v(-19.72, 50.85) * mm});
            skLineSegment(sketch, "E310", {"start": v(-19.72, 50.85) * mm, "end": v(-21.24, 52.54) * mm});
            skLineSegment(sketch, "E311", {"start": v(-21.24, 52.54) * mm, "end": v(-22.35, 52.92) * mm});
            skLineSegment(sketch, "E312", {"start": v(-22.35, 52.92) * mm, "end": v(-23.65, 52.87) * mm});
            skLineSegment(sketch, "E313", {"start": v(-23.65, 52.87) * mm, "end": v(-24.96, 52.32) * mm});
            skLineSegment(sketch, "E314", {"start": v(-24.96, 52.32) * mm, "end": v(-25.87, 51.39) * mm});
            skLineSegment(sketch, "E315", {"start": v(-25.87, 51.39) * mm, "end": v(-26.32, 50.14) * mm});
            skLineSegment(sketch, "E316", {"start": v(-26.32, 50.14) * mm, "end": v(-26.27, 48.69) * mm});
            skLineSegment(sketch, "E317", {"start": v(-26.27, 48.69) * mm, "end": v(-25.47, 47) * mm});
            skLineSegment(sketch, "E318", {"start": v(-25.47, 47) * mm, "end": v(-24.1, 46) * mm});
            skLineSegment(sketch, "E319", {"start": v(-24.1, 46) * mm, "end": v(-22.43, 45.8) * mm});
            skLineSegment(sketch, "E320", {"start": v(-22.43, 45.8) * mm, "end": v(-20.76, 46.52) * mm});
            skLineSegment(sketch, "E321", {"start": v(-26.75, 49.44) * mm, "end": v(-26.37, 51.04) * mm});
            skLineSegment(sketch, "E322", {"start": v(-26.37, 51.04) * mm, "end": v(-25.42, 52.36) * mm});
            skLineSegment(sketch, "E323", {"start": v(-25.42, 52.36) * mm, "end": v(-25.02, 52.79) * mm});
            skLineSegment(sketch, "E324", {"start": v(-25.02, 52.79) * mm, "end": v(-27.5, 56.76) * mm});
            skLineSegment(sketch, "E325", {"start": v(-27.5, 56.76) * mm, "end": v(-29.6, 58.6) * mm});
            skLineSegment(sketch, "E326", {"start": v(-29.6, 58.6) * mm, "end": v(-30.62, 58.77) * mm});
            skLineSegment(sketch, "E327", {"start": v(-30.62, 58.77) * mm, "end": v(-31.75, 58.49) * mm});
            skLineSegment(sketch, "E328", {"start": v(-31.75, 58.49) * mm, "end": v(-33.94, 56.78) * mm});
            skLineSegment(sketch, "E329", {"start": v(-33.94, 56.78) * mm, "end": v(-35.42, 54.19) * mm});
            skLineSegment(sketch, "E330", {"start": v(-35.42, 54.19) * mm, "end": v(-35.92, 51.49) * mm});
            skLineSegment(sketch, "E331", {"start": v(-35.92, 51.49) * mm, "end": v(-35.7, 50.34) * mm});
            skLineSegment(sketch, "E332", {"start": v(-35.7, 50.34) * mm, "end": v(-35.14, 49.46) * mm});
            skLineSegment(sketch, "E333", {"start": v(-35.14, 49.46) * mm, "end": v(-33.66, 48.81) * mm});
            skLineSegment(sketch, "E334", {"start": v(-33.66, 48.81) * mm, "end": v(-31.06, 48.52) * mm});
            skLineSegment(sketch, "E335", {"start": v(-31.06, 48.52) * mm, "end": v(-28.08, 48.78) * mm});
            skLineSegment(sketch, "E336", {"start": v(-28.08, 48.78) * mm, "end": v(-26.76, 49.04) * mm});
            skLineSegment(sketch, "E337", {"start": v(-26.76, 49.04) * mm, "end": v(-26.75, 49.44) * mm});
            skLineSegment(sketch, "E338", {"start": v(-19.45, 53.59) * mm, "end": v(-17.58, 56.73) * mm});
            skLineSegment(sketch, "E339", {"start": v(-17.58, 56.73) * mm, "end": v(-17.14, 58.24) * mm});
            skLineSegment(sketch, "E340", {"start": v(-17.14, 58.24) * mm, "end": v(-17.14, 59.5) * mm});
            skLineSegment(sketch, "E341", {"start": v(-17.14, 59.5) * mm, "end": v(-17.71, 60.8) * mm});
            skLineSegment(sketch, "E342", {"start": v(-17.71, 60.8) * mm, "end": v(-18.74, 61.78) * mm});
            skLineSegment(sketch, "E343", {"start": v(-18.74, 61.78) * mm, "end": v(-20.08, 62.45) * mm});
            skLineSegment(sketch, "E344", {"start": v(-20.08, 62.45) * mm, "end": v(-21.58, 62.78) * mm});
            skLineSegment(sketch, "E345", {"start": v(-21.58, 62.78) * mm, "end": v(-23.1, 62.76) * mm});
            skLineSegment(sketch, "E346", {"start": v(-23.1, 62.76) * mm, "end": v(-24.5, 62.37) * mm});
            skLineSegment(sketch, "E347", {"start": v(-24.5, 62.37) * mm, "end": v(-25.63, 61.6) * mm});
            skLineSegment(sketch, "E348", {"start": v(-25.63, 61.6) * mm, "end": v(-26.35, 60.43) * mm});
            skLineSegment(sketch, "E349", {"start": v(-26.35, 60.43) * mm, "end": v(-26.15, 57.35) * mm});
            skLineSegment(sketch, "E350", {"start": v(-26.15, 57.35) * mm, "end": v(-24.77, 53.1) * mm});
            skLineSegment(sketch, "E351", {"start": v(-24.77, 53.1) * mm, "end": v(-23.88, 53.14) * mm});
            skLineSegment(sketch, "E352", {"start": v(-23.88, 53.14) * mm, "end": v(-22.46, 53.27) * mm});
            skLineSegment(sketch, "E353", {"start": v(-22.46, 53.27) * mm, "end": v(-20.63, 52.54) * mm});
            skLineSegment(sketch, "E354", {"start": v(-20.63, 52.54) * mm, "end": v(-19.45, 53.59) * mm});
            skLineSegment(sketch, "E355", {"start": v(-53.8, 41.12) * mm, "end": v(-56.24, 41.5) * mm});
            skLineSegment(sketch, "E356", {"start": v(-56.24, 41.5) * mm, "end": v(-58.58, 42.62) * mm});
            skLineSegment(sketch, "E357", {"start": v(-58.58, 42.62) * mm, "end": v(-60.46, 44.26) * mm});
            skLineSegment(sketch, "E358", {"start": v(-60.46, 44.26) * mm, "end": v(-61.53, 46.18) * mm});
            skLineSegment(sketch, "E359", {"start": v(-61.53, 46.18) * mm, "end": v(-61.68, 47.26) * mm});
            skLineSegment(sketch, "E360", {"start": v(-61.68, 47.26) * mm, "end": v(-61.45, 48.23) * mm});
            skLineSegment(sketch, "E361", {"start": v(-61.45, 48.23) * mm, "end": v(-59.67, 50.33) * mm});
            skLineSegment(sketch, "E362", {"start": v(-59.67, 50.33) * mm, "end": v(-58.93, 50.97) * mm});
            skLineSegment(sketch, "E363", {"start": v(-58.93, 50.97) * mm, "end": v(-60.48, 50.68) * mm});
            skLineSegment(sketch, "E364", {"start": v(-60.48, 50.68) * mm, "end": v(-62.43, 50.46) * mm});
            skLineSegment(sketch, "E365", {"start": v(-62.43, 50.46) * mm, "end": v(-63.64, 50.94) * mm});
            skLineSegment(sketch, "E366", {"start": v(-63.64, 50.94) * mm, "end": v(-64.94, 52.4) * mm});
            skLineSegment(sketch, "E367", {"start": v(-64.94, 52.4) * mm, "end": v(-65.58, 54.43) * mm});
            skLineSegment(sketch, "E368", {"start": v(-65.58, 54.43) * mm, "end": v(-65.53, 56.7) * mm});
            skLineSegment(sketch, "E369", {"start": v(-65.53, 56.7) * mm, "end": v(-64.73, 58.87) * mm});
            skLineSegment(sketch, "E370", {"start": v(-64.73, 58.87) * mm, "end": v(-63.78, 60.05) * mm});
            skLineSegment(sketch, "E371", {"start": v(-63.78, 60.05) * mm, "end": v(-62.65, 60.62) * mm});
            skLineSegment(sketch, "E372", {"start": v(-62.65, 60.62) * mm, "end": v(-61.27, 60.58) * mm});
            skLineSegment(sketch, "E373", {"start": v(-61.27, 60.58) * mm, "end": v(-59.56, 59.95) * mm});
            skLineSegment(sketch, "E374", {"start": v(-59.56, 59.95) * mm, "end": v(-58.6, 59.5) * mm});
            skLineSegment(sketch, "E375", {"start": v(-58.6, 59.5) * mm, "end": v(-59.27, 60.43) * mm});
            skLineSegment(sketch, "E376", {"start": v(-59.27, 60.43) * mm, "end": v(-60.7, 62.66) * mm});
            skLineSegment(sketch, "E377", {"start": v(-60.7, 62.66) * mm, "end": v(-60.88, 64.28) * mm});
            skLineSegment(sketch, "E378", {"start": v(-60.88, 64.28) * mm, "end": v(-60.35, 65.38) * mm});
            skLineSegment(sketch, "E379", {"start": v(-60.35, 65.38) * mm, "end": v(-59.44, 66.33) * mm});
            skLineSegment(sketch, "E380", {"start": v(-59.44, 66.33) * mm, "end": v(-56.9, 67.68) * mm});
            skLineSegment(sketch, "E381", {"start": v(-56.9, 67.68) * mm, "end": v(-53.94, 68.1) * mm});
            skLineSegment(sketch, "E382", {"start": v(-53.94, 68.1) * mm, "end": v(-51.29, 67.36) * mm});
            skLineSegment(sketch, "E383", {"start": v(-51.29, 67.36) * mm, "end": v(-50.32, 66.49) * mm});
            skLineSegment(sketch, "E384", {"start": v(-50.32, 66.49) * mm, "end": v(-49.8, 65.3) * mm});
            skLineSegment(sketch, "E385", {"start": v(-49.8, 65.3) * mm, "end": v(-49.72, 63.7) * mm});
            skLineSegment(sketch, "E386", {"start": v(-49.72, 63.7) * mm, "end": v(-50.04, 61.58) * mm});
            skLineSegment(sketch, "E387", {"start": v(-50.04, 61.58) * mm, "end": v(-50.16, 60.84) * mm});
            skLineSegment(sketch, "E388", {"start": v(-50.16, 60.84) * mm, "end": v(-49.91, 61.16) * mm});
            skLineSegment(sketch, "E389", {"start": v(-49.91, 61.16) * mm, "end": v(-47.34, 64.72) * mm});
            skLineSegment(sketch, "E390", {"start": v(-47.34, 64.72) * mm, "end": v(-46.27, 65.24) * mm});
            skLineSegment(sketch, "E391", {"start": v(-46.27, 65.24) * mm, "end": v(-45.06, 65.27) * mm});
            skLineSegment(sketch, "E392", {"start": v(-45.06, 65.27) * mm, "end": v(-42.6, 64.12) * mm});
            skLineSegment(sketch, "E393", {"start": v(-42.6, 64.12) * mm, "end": v(-40.7, 61.85) * mm});
            skLineSegment(sketch, "E394", {"start": v(-40.7, 61.85) * mm, "end": v(-40.17, 60.47) * mm});
            skLineSegment(sketch, "E395", {"start": v(-40.17, 60.47) * mm, "end": v(-40.06, 59.02) * mm});
            skLineSegment(sketch, "E396", {"start": v(-40.06, 59.02) * mm, "end": v(-40.34, 57.79) * mm});
            skLineSegment(sketch, "E397", {"start": v(-40.34, 57.79) * mm, "end": v(-40.98, 56.78) * mm});
            skLineSegment(sketch, "E398", {"start": v(-40.98, 56.78) * mm, "end": v(-43.43, 55.32) * mm});
            skLineSegment(sketch, "E399", {"start": v(-43.43, 55.32) * mm, "end": v(-43.97, 55.06) * mm});
            skLineSegment(sketch, "E400", {"start": v(-43.97, 55.06) * mm, "end": v(-43.42, 54.92) * mm});
            skLineSegment(sketch, "E401", {"start": v(-43.42, 54.92) * mm, "end": v(-40.64, 54.1) * mm});
            skLineSegment(sketch, "E402", {"start": v(-40.64, 54.1) * mm, "end": v(-39.9, 53.26) * mm});
            skLineSegment(sketch, "E403", {"start": v(-39.9, 53.26) * mm, "end": v(-39.48, 52.07) * mm});
            skLineSegment(sketch, "E404", {"start": v(-39.48, 52.07) * mm, "end": v(-39.5, 49.69) * mm});
            skLineSegment(sketch, "E405", {"start": v(-39.5, 49.69) * mm, "end": v(-40.34, 47.22) * mm});
            skLineSegment(sketch, "E406", {"start": v(-40.34, 47.22) * mm, "end": v(-41.8, 45.09) * mm});
            skLineSegment(sketch, "E407", {"start": v(-41.8, 45.09) * mm, "end": v(-43.68, 43.7) * mm});
            skLineSegment(sketch, "E408", {"start": v(-43.68, 43.7) * mm, "end": v(-45.17, 43.38) * mm});
            skLineSegment(sketch, "E409", {"start": v(-45.17, 43.38) * mm, "end": v(-46.62, 43.75) * mm});
            skLineSegment(sketch, "E410", {"start": v(-46.62, 43.75) * mm, "end": v(-48.14, 44.88) * mm});
            skLineSegment(sketch, "E411", {"start": v(-48.14, 44.88) * mm, "end": v(-49.83, 46.82) * mm});
            skLineSegment(sketch, "E412", {"start": v(-49.83, 46.82) * mm, "end": v(-50.67, 47.83) * mm});
            skLineSegment(sketch, "E413", {"start": v(-50.67, 47.83) * mm, "end": v(-50.65, 46.7) * mm});
            skLineSegment(sketch, "E414", {"start": v(-50.65, 46.7) * mm, "end": v(-50.7, 44.11) * mm});
            skLineSegment(sketch, "E415", {"start": v(-50.7, 44.11) * mm, "end": v(-51.2, 42.4) * mm});
            skLineSegment(sketch, "E416", {"start": v(-51.2, 42.4) * mm, "end": v(-52.2, 41.45) * mm});
            skLineSegment(sketch, "E417", {"start": v(-52.2, 41.45) * mm, "end": v(-53.8, 41.12) * mm});
            skLineSegment(sketch, "E418", {"start": v(-53.8, 41.12) * mm, "end": v(-53.8, 41.12) * mm});
            skLineSegment(sketch, "E419", {"start": v(-52.16, 41.88) * mm, "end": v(-51.4, 42.7) * mm});
            skLineSegment(sketch, "E420", {"start": v(-51.4, 42.7) * mm, "end": v(-51, 44.2) * mm});
            skLineSegment(sketch, "E421", {"start": v(-51, 44.2) * mm, "end": v(-51.22, 49.43) * mm});
            skLineSegment(sketch, "E422", {"start": v(-51.22, 49.43) * mm, "end": v(-51.43, 50.55) * mm});
            skLineSegment(sketch, "E423", {"start": v(-51.43, 50.55) * mm, "end": v(-52.03, 50.67) * mm});
            skLineSegment(sketch, "E424", {"start": v(-52.03, 50.67) * mm, "end": v(-53.76, 51.08) * mm});
            skLineSegment(sketch, "E425", {"start": v(-53.76, 51.08) * mm, "end": v(-55.15, 52.2) * mm});
            skLineSegment(sketch, "E426", {"start": v(-55.15, 52.2) * mm, "end": v(-55.65, 52.65) * mm});
            skLineSegment(sketch, "E427", {"start": v(-55.65, 52.65) * mm, "end": v(-56.52, 52.2) * mm});
            skLineSegment(sketch, "E428", {"start": v(-56.52, 52.2) * mm, "end": v(-59.88, 49.7) * mm});
            skLineSegment(sketch, "E429", {"start": v(-59.88, 49.7) * mm, "end": v(-61.33, 47.65) * mm});
            skLineSegment(sketch, "E430", {"start": v(-61.33, 47.65) * mm, "end": v(-61.3, 46.36) * mm});
            skLineSegment(sketch, "E431", {"start": v(-61.3, 46.36) * mm, "end": v(-60.7, 45.08) * mm});
            skLineSegment(sketch, "E432", {"start": v(-60.7, 45.08) * mm, "end": v(-58.28, 42.83) * mm});
            skLineSegment(sketch, "E433", {"start": v(-58.28, 42.83) * mm, "end": v(-55.1, 41.55) * mm});
            skLineSegment(sketch, "E434", {"start": v(-55.1, 41.55) * mm, "end": v(-53.53, 41.47) * mm});
            skLineSegment(sketch, "E435", {"start": v(-53.53, 41.47) * mm, "end": v(-52.16, 41.88) * mm});
            skLineSegment(sketch, "E436", {"start": v(-52.16, 41.88) * mm, "end": v(-52.16, 41.88) * mm});
            skLineSegment(sketch, "E437", {"start": v(-43.05, 44.43) * mm, "end": v(-41.2, 46.36) * mm});
            skLineSegment(sketch, "E438", {"start": v(-41.2, 46.36) * mm, "end": v(-40.04, 48.84) * mm});
            skLineSegment(sketch, "E439", {"start": v(-40.04, 48.84) * mm, "end": v(-39.7, 51.35) * mm});
            skLineSegment(sketch, "E440", {"start": v(-39.7, 51.35) * mm, "end": v(-40.38, 53.36) * mm});
            skLineSegment(sketch, "E441", {"start": v(-40.38, 53.36) * mm, "end": v(-41.22, 54.05) * mm});
            skLineSegment(sketch, "E442", {"start": v(-41.22, 54.05) * mm, "end": v(-42.54, 54.48) * mm});
            skLineSegment(sketch, "E443", {"start": v(-42.54, 54.48) * mm, "end": v(-47.03, 54.6) * mm});
            skLineSegment(sketch, "E444", {"start": v(-47.03, 54.6) * mm, "end": v(-48.28, 54.3) * mm});
            skLineSegment(sketch, "E445", {"start": v(-48.28, 54.3) * mm, "end": v(-48.4, 53.61) * mm});
            skLineSegment(sketch, "E446", {"start": v(-48.4, 53.61) * mm, "end": v(-49.2, 52.07) * mm});
            skLineSegment(sketch, "E447", {"start": v(-49.2, 52.07) * mm, "end": v(-50.58, 51) * mm});
            skLineSegment(sketch, "E448", {"start": v(-50.58, 51) * mm, "end": v(-51.03, 50.66) * mm});
            skLineSegment(sketch, "E449", {"start": v(-51.03, 50.66) * mm, "end": v(-50.93, 49.58) * mm});
            skLineSegment(sketch, "E450", {"start": v(-50.93, 49.58) * mm, "end": v(-50.63, 48.5) * mm});
            skLineSegment(sketch, "E451", {"start": v(-50.63, 48.5) * mm, "end": v(-49.52, 46.95) * mm});
            skLineSegment(sketch, "E452", {"start": v(-49.52, 46.95) * mm, "end": v(-47.4, 44.64) * mm});
            skLineSegment(sketch, "E453", {"start": v(-47.4, 44.64) * mm, "end": v(-45.61, 43.71) * mm});
            skLineSegment(sketch, "E454", {"start": v(-45.61, 43.71) * mm, "end": v(-43.05, 44.43) * mm});
            skLineSegment(sketch, "E455", {"start": v(-50.87, 51.22) * mm, "end": v(-49.3, 52.47) * mm});
            skLineSegment(sketch, "E456", {"start": v(-49.3, 52.47) * mm, "end": v(-48.64, 54.22) * mm});
            skLineSegment(sketch, "E457", {"start": v(-48.64, 54.22) * mm, "end": v(-48.92, 56.06) * mm});
            skLineSegment(sketch, "E458", {"start": v(-48.92, 56.06) * mm, "end": v(-50.2, 57.57) * mm});
            skLineSegment(sketch, "E459", {"start": v(-50.2, 57.57) * mm, "end": v(-51.97, 58.17) * mm});
            skLineSegment(sketch, "E460", {"start": v(-51.97, 58.17) * mm, "end": v(-53.67, 57.82) * mm});
            skLineSegment(sketch, "E461", {"start": v(-53.67, 57.82) * mm, "end": v(-55, 56.7) * mm});
            skLineSegment(sketch, "E462", {"start": v(-55, 56.7) * mm, "end": v(-55.64, 54.93) * mm});
            skLineSegment(sketch, "E463", {"start": v(-55.64, 54.93) * mm, "end": v(-55.44, 53.4) * mm});
            skLineSegment(sketch, "E464", {"start": v(-55.44, 53.4) * mm, "end": v(-54.68, 52.15) * mm});
            skLineSegment(sketch, "E465", {"start": v(-54.68, 52.15) * mm, "end": v(-53.49, 51.3) * mm});
            skLineSegment(sketch, "E466", {"start": v(-53.49, 51.3) * mm, "end": v(-51.98, 51) * mm});
            skLineSegment(sketch, "E467", {"start": v(-51.98, 51) * mm, "end": v(-50.87, 51.22) * mm});
            skLineSegment(sketch, "E468", {"start": v(-50.87, 51.22) * mm, "end": v(-50.87, 51.22) * mm});
            skLineSegment(sketch, "E469", {"start": v(-58.34, 51.63) * mm, "end": v(-55.86, 53.02) * mm});
            skLineSegment(sketch, "E470", {"start": v(-55.86, 53.02) * mm, "end": v(-55.85, 53.55) * mm});
            skLineSegment(sketch, "E471", {"start": v(-55.85, 53.55) * mm, "end": v(-55.97, 54.9) * mm});
            skLineSegment(sketch, "E472", {"start": v(-55.97, 54.9) * mm, "end": v(-55.56, 56.38) * mm});
            skLineSegment(sketch, "E473", {"start": v(-55.56, 56.38) * mm, "end": v(-55.3, 56.92) * mm});
            skLineSegment(sketch, "E474", {"start": v(-55.3, 56.92) * mm, "end": v(-55.84, 57.33) * mm});
            skLineSegment(sketch, "E475", {"start": v(-55.84, 57.33) * mm, "end": v(-59.64, 59.62) * mm});
            skLineSegment(sketch, "E476", {"start": v(-59.64, 59.62) * mm, "end": v(-61.3, 60.22) * mm});
            skLineSegment(sketch, "E477", {"start": v(-61.3, 60.22) * mm, "end": v(-62.5, 60.32) * mm});
            skLineSegment(sketch, "E478", {"start": v(-62.5, 60.32) * mm, "end": v(-63.43, 59.9) * mm});
            skLineSegment(sketch, "E479", {"start": v(-63.43, 59.9) * mm, "end": v(-64.2, 59.12) * mm});
            skLineSegment(sketch, "E480", {"start": v(-64.2, 59.12) * mm, "end": v(-65.15, 56.85) * mm});
            skLineSegment(sketch, "E481", {"start": v(-65.15, 56.85) * mm, "end": v(-65.23, 54.21) * mm});
            skLineSegment(sketch, "E482", {"start": v(-65.23, 54.21) * mm, "end": v(-64.27, 51.93) * mm});
            skLineSegment(sketch, "E483", {"start": v(-64.27, 51.93) * mm, "end": v(-63.29, 51.11) * mm});
            skLineSegment(sketch, "E484", {"start": v(-63.29, 51.11) * mm, "end": v(-62.04, 50.79) * mm});
            skLineSegment(sketch, "E485", {"start": v(-62.04, 50.79) * mm, "end": v(-60.43, 50.96) * mm});
            skLineSegment(sketch, "E486", {"start": v(-60.43, 50.96) * mm, "end": v(-58.34, 51.63) * mm});
            skLineSegment(sketch, "E487", {"start": v(-43.3, 55.73) * mm, "end": v(-41.13, 57.1) * mm});
            skLineSegment(sketch, "E488", {"start": v(-41.13, 57.1) * mm, "end": v(-40.37, 59.05) * mm});
            skLineSegment(sketch, "E489", {"start": v(-40.37, 59.05) * mm, "end": v(-40.73, 61.15) * mm});
            skLineSegment(sketch, "E490", {"start": v(-40.73, 61.15) * mm, "end": v(-41.93, 63.07) * mm});
            skLineSegment(sketch, "E491", {"start": v(-41.93, 63.07) * mm, "end": v(-43.67, 64.46) * mm});
            skLineSegment(sketch, "E492", {"start": v(-43.67, 64.46) * mm, "end": v(-45.63, 64.97) * mm});
            skLineSegment(sketch, "E493", {"start": v(-45.63, 64.97) * mm, "end": v(-47.28, 64.32) * mm});
            skLineSegment(sketch, "E494", {"start": v(-47.28, 64.32) * mm, "end": v(-48.99, 62.1) * mm});
            skLineSegment(sketch, "E495", {"start": v(-48.99, 62.1) * mm, "end": v(-50.85, 58.38) * mm});
            skLineSegment(sketch, "E496", {"start": v(-50.85, 58.38) * mm, "end": v(-50.22, 57.94) * mm});
            skLineSegment(sketch, "E497", {"start": v(-50.22, 57.94) * mm, "end": v(-49.05, 56.9) * mm});
            skLineSegment(sketch, "E498", {"start": v(-49.05, 56.9) * mm, "end": v(-48.45, 55.54) * mm});
            skLineSegment(sketch, "E499", {"start": v(-48.45, 55.54) * mm, "end": v(-48.16, 54.95) * mm});
            skLineSegment(sketch, "E500", {"start": v(-48.16, 54.95) * mm, "end": v(-47.01, 54.94) * mm});
            skLineSegment(sketch, "E501", {"start": v(-47.01, 54.94) * mm, "end": v(-45.89, 54.97) * mm});
            skLineSegment(sketch, "E502", {"start": v(-45.89, 54.97) * mm, "end": v(-43.3, 55.73) * mm});
            skLineSegment(sketch, "E503", {"start": v(-54.63, 57.58) * mm, "end": v(-53.3, 58.33) * mm});
            skLineSegment(sketch, "E504", {"start": v(-53.3, 58.33) * mm, "end": v(-51.87, 58.48) * mm});
            skLineSegment(sketch, "E505", {"start": v(-51.87, 58.48) * mm, "end": v(-51.3, 58.42) * mm});
            skLineSegment(sketch, "E506", {"start": v(-51.3, 58.42) * mm, "end": v(-51.17, 58.65) * mm});
            skLineSegment(sketch, "E507", {"start": v(-51.17, 58.65) * mm, "end": v(-50.43, 61.37) * mm});
            skLineSegment(sketch, "E508", {"start": v(-50.43, 61.37) * mm, "end": v(-50.05, 64.57) * mm});
            skLineSegment(sketch, "E509", {"start": v(-50.05, 64.57) * mm, "end": v(-50.75, 66.53) * mm});
            skLineSegment(sketch, "E510", {"start": v(-50.75, 66.53) * mm, "end": v(-52.65, 67.61) * mm});
            skLineSegment(sketch, "E511", {"start": v(-52.65, 67.61) * mm, "end": v(-54.33, 67.76) * mm});
            skLineSegment(sketch, "E512", {"start": v(-54.33, 67.76) * mm, "end": v(-56.16, 67.5) * mm});
            skLineSegment(sketch, "E513", {"start": v(-56.16, 67.5) * mm, "end": v(-57.9, 66.9) * mm});
            skLineSegment(sketch, "E514", {"start": v(-57.9, 66.9) * mm, "end": v(-59.35, 65.99) * mm});
            skLineSegment(sketch, "E515", {"start": v(-59.35, 65.99) * mm, "end": v(-60.4, 64.68) * mm});
            skLineSegment(sketch, "E516", {"start": v(-60.4, 64.68) * mm, "end": v(-60.52, 63.22) * mm});
            skLineSegment(sketch, "E517", {"start": v(-60.52, 63.22) * mm, "end": v(-59.68, 61.48) * mm});
            skLineSegment(sketch, "E518", {"start": v(-59.68, 61.48) * mm, "end": v(-57.85, 59.32) * mm});
            skLineSegment(sketch, "E519", {"start": v(-57.85, 59.32) * mm, "end": v(-55.06, 57.24) * mm});
            skLineSegment(sketch, "E520", {"start": v(-55.06, 57.24) * mm, "end": v(-54.63, 57.58) * mm});
            skLineSegment(sketch, "E521", {"start": v(77.31, -39.88) * mm, "end": v(76.52, -43.19) * mm});
            skLineSegment(sketch, "E522", {"start": v(76.52, -43.19) * mm, "end": v(75.65, -44.83) * mm});
            skLineSegment(sketch, "E523", {"start": v(75.65, -44.83) * mm, "end": v(74.5, -46.15) * mm});
            skLineSegment(sketch, "E524", {"start": v(74.5, -46.15) * mm, "end": v(70.7, -48.32) * mm});
            skLineSegment(sketch, "E525", {"start": v(70.7, -48.32) * mm, "end": v(67.2, -49.39) * mm});
            skLineSegment(sketch, "E526", {"start": v(67.2, -49.39) * mm, "end": v(63.97, -49.86) * mm});
            skLineSegment(sketch, "E527", {"start": v(63.97, -49.86) * mm, "end": v(59.5, -50.08) * mm});
            skLineSegment(sketch, "E528", {"start": v(59.5, -50.08) * mm, "end": v(55.3, -49.48) * mm});
            skLineSegment(sketch, "E529", {"start": v(55.3, -49.48) * mm, "end": v(49.96, -47.88) * mm});
            skLineSegment(sketch, "E530", {"start": v(49.96, -47.88) * mm, "end": v(47.53, -46.73) * mm});
            skLineSegment(sketch, "E531", {"start": v(47.53, -46.73) * mm, "end": v(45.22, -45.2) * mm});
            skLineSegment(sketch, "E532", {"start": v(45.22, -45.2) * mm, "end": v(43.29, -43.65) * mm});
            skLineSegment(sketch, "E533", {"start": v(43.29, -43.65) * mm, "end": v(41.92, -42.15) * mm});
            skLineSegment(sketch, "E534", {"start": v(41.92, -42.15) * mm, "end": v(40.34, -39.71) * mm});
            skLineSegment(sketch, "E535", {"start": v(40.34, -39.71) * mm, "end": v(38.56, -35.87) * mm});
            skLineSegment(sketch, "E536", {"start": v(38.56, -35.87) * mm, "end": v(40.02, -36.3) * mm});
            skLineSegment(sketch, "E537", {"start": v(40.02, -36.3) * mm, "end": v(42.52, -37.14) * mm});
            skLineSegment(sketch, "E538", {"start": v(42.52, -37.14) * mm, "end": v(48.29, -37.64) * mm});
            skLineSegment(sketch, "E539", {"start": v(48.29, -37.64) * mm, "end": v(52.66, -36.73) * mm});
            skLineSegment(sketch, "E540", {"start": v(52.66, -36.73) * mm, "end": v(56.4, -34.74) * mm});
            skLineSegment(sketch, "E541", {"start": v(56.4, -34.74) * mm, "end": v(57.9, -33.86) * mm});
            skLineSegment(sketch, "E542", {"start": v(57.9, -33.86) * mm, "end": v(59.52, -33.22) * mm});
            skLineSegment(sketch, "E543", {"start": v(59.52, -33.22) * mm, "end": v(62.66, -32.37) * mm});
            skLineSegment(sketch, "E544", {"start": v(62.66, -32.37) * mm, "end": v(65.88, -32.23) * mm});
            skLineSegment(sketch, "E545", {"start": v(65.88, -32.23) * mm, "end": v(70.14, -32.85) * mm});
            skLineSegment(sketch, "E546", {"start": v(70.14, -32.85) * mm, "end": v(71.96, -33.52) * mm});
            skLineSegment(sketch, "E547", {"start": v(71.96, -33.52) * mm, "end": v(74.1, -34.96) * mm});
            skLineSegment(sketch, "E548", {"start": v(74.1, -34.96) * mm, "end": v(75.96, -36.91) * mm});
            skLineSegment(sketch, "E549", {"start": v(75.96, -36.91) * mm, "end": v(77.22, -38.89) * mm});
            skLineSegment(sketch, "E550", {"start": v(77.22, -38.89) * mm, "end": v(82.52, -40.35) * mm});
            skLineSegment(sketch, "E551", {"start": v(82.52, -40.35) * mm, "end": v(86.52, -41.64) * mm});
            skLineSegment(sketch, "E552", {"start": v(86.52, -41.64) * mm, "end": v(86.7, -44.6) * mm});
            skLineSegment(sketch, "E553", {"start": v(86.7, -44.6) * mm, "end": v(85.42, -43.04) * mm});
            skLineSegment(sketch, "E554", {"start": v(85.42, -43.04) * mm, "end": v(83.03, -41.5) * mm});
            skLineSegment(sketch, "E555", {"start": v(83.03, -41.5) * mm, "end": v(80.12, -40.34) * mm});
            skLineSegment(sketch, "E556", {"start": v(80.12, -40.34) * mm, "end": v(77.31, -39.88) * mm});
            skLineSegment(sketch, "E557", {"start": v(76, -39.4) * mm, "end": v(70.67, -38.45) * mm});
            skLineSegment(sketch, "E558", {"start": v(70.67, -38.45) * mm, "end": v(66.5, -38.34) * mm});
            skLineSegment(sketch, "E559", {"start": v(66.5, -38.34) * mm, "end": v(64.07, -38.68) * mm});
            skLineSegment(sketch, "E560", {"start": v(64.07, -38.68) * mm, "end": v(59.33, -40.39) * mm});
            skLineSegment(sketch, "E561", {"start": v(59.33, -40.39) * mm, "end": v(56.83, -41.56) * mm});
            skLineSegment(sketch, "E562", {"start": v(56.83, -41.56) * mm, "end": v(53.08, -42.43) * mm});
            skLineSegment(sketch, "E563", {"start": v(53.08, -42.43) * mm, "end": v(50.12, -42.56) * mm});
            skLineSegment(sketch, "E564", {"start": v(50.12, -42.56) * mm, "end": v(47.07, -41.87) * mm});
            skLineSegment(sketch, "E565", {"start": v(47.07, -41.87) * mm, "end": v(44.88, -40.98) * mm});
            skLineSegment(sketch, "E566", {"start": v(44.88, -40.98) * mm, "end": v(42.25, -39.45) * mm});
            skLineSegment(sketch, "E567", {"start": v(42.25, -39.45) * mm, "end": v(39.7, -37.23) * mm});
            skLineSegment(sketch, "E568", {"start": v(39.7, -37.23) * mm, "end": v(44.09, -40.19) * mm});
            skLineSegment(sketch, "E569", {"start": v(44.09, -40.19) * mm, "end": v(49.16, -41.96) * mm});
            skLineSegment(sketch, "E570", {"start": v(49.16, -41.96) * mm, "end": v(51.43, -42.07) * mm});
            skLineSegment(sketch, "E571", {"start": v(51.43, -42.07) * mm, "end": v(53.83, -41.74) * mm});
            skLineSegment(sketch, "E572", {"start": v(53.83, -41.74) * mm, "end": v(58.74, -40.1) * mm});
            skLineSegment(sketch, "E573", {"start": v(58.74, -40.1) * mm, "end": v(62.55, -38.47) * mm});
            skLineSegment(sketch, "E574", {"start": v(62.55, -38.47) * mm, "end": v(64.46, -37.9) * mm});
            skLineSegment(sketch, "E575", {"start": v(64.46, -37.9) * mm, "end": v(66.18, -37.73) * mm});
            skLineSegment(sketch, "E576", {"start": v(66.18, -37.73) * mm, "end": v(68.7, -37.61) * mm});
            skLineSegment(sketch, "E577", {"start": v(68.7, -37.61) * mm, "end": v(71.19, -37.83) * mm});
            skLineSegment(sketch, "E578", {"start": v(71.19, -37.83) * mm, "end": v(76.07, -38.65) * mm});
            skLineSegment(sketch, "E579", {"start": v(76.07, -38.65) * mm, "end": v(76, -39.4) * mm});
            skLineSegment(sketch, "E580", {"start": v(74.44, -39.61) * mm, "end": v(74.91, -39.68) * mm});
            skLineSegment(sketch, "E581", {"start": v(74.91, -39.68) * mm, "end": v(74.91, -40.72) * mm});
            skLineSegment(sketch, "E582", {"start": v(74.91, -40.72) * mm, "end": v(74.6, -41.82) * mm});
            skLineSegment(sketch, "E583", {"start": v(74.6, -41.82) * mm, "end": v(73.69, -43.75) * mm});
            skLineSegment(sketch, "E584", {"start": v(73.69, -43.75) * mm, "end": v(72.22, -45.33) * mm});
            skLineSegment(sketch, "E585", {"start": v(72.22, -45.33) * mm, "end": v(67.8, -48.83) * mm});
            skLineSegment(sketch, "E586", {"start": v(67.8, -48.83) * mm, "end": v(72.6, -44.49) * mm});
            skLineSegment(sketch, "E587", {"start": v(72.6, -44.49) * mm, "end": v(73.93, -42.38) * mm});
            skLineSegment(sketch, "E588", {"start": v(73.93, -42.38) * mm, "end": v(74.44, -39.61) * mm});
            skLineSegment(sketch, "E589", {"start": v(69.78, -38.86) * mm, "end": v(70.17, -38.84) * mm});
            skLineSegment(sketch, "E590", {"start": v(70.17, -38.84) * mm, "end": v(70.23, -38.77) * mm});
            skLineSegment(sketch, "E591", {"start": v(70.23, -38.77) * mm, "end": v(70.2, -39.9) * mm});
            skLineSegment(sketch, "E592", {"start": v(70.2, -39.9) * mm, "end": v(69.84, -41.08) * mm});
            skLineSegment(sketch, "E593", {"start": v(69.84, -41.08) * mm, "end": v(68.59, -43.2) * mm});
            skLineSegment(sketch, "E594", {"start": v(68.59, -43.2) * mm, "end": v(66.8, -44.94) * mm});
            skLineSegment(sketch, "E595", {"start": v(66.8, -44.94) * mm, "end": v(61.95, -48.66) * mm});
            skLineSegment(sketch, "E596", {"start": v(61.95, -48.66) * mm, "end": v(67.4, -44.01) * mm});
            skLineSegment(sketch, "E597", {"start": v(67.4, -44.01) * mm, "end": v(69.15, -41.6) * mm});
            skLineSegment(sketch, "E598", {"start": v(69.15, -41.6) * mm, "end": v(69.78, -38.86) * mm});
            skLineSegment(sketch, "E599", {"start": v(64, -39.24) * mm, "end": v(64.5, -39.08) * mm});
            skLineSegment(sketch, "E600", {"start": v(64.5, -39.08) * mm, "end": v(64.23, -40.71) * mm});
            skLineSegment(sketch, "E601", {"start": v(64.23, -40.71) * mm, "end": v(63.64, -42.21) * mm});
            skLineSegment(sketch, "E602", {"start": v(63.64, -42.21) * mm, "end": v(62.34, -43.77) * mm});
            skLineSegment(sketch, "E603", {"start": v(62.34, -43.77) * mm, "end": v(60.44, -45.37) * mm});
            skLineSegment(sketch, "E604", {"start": v(60.44, -45.37) * mm, "end": v(59.53, -45.91) * mm});
            skLineSegment(sketch, "E605", {"start": v(59.53, -45.91) * mm, "end": v(54.79, -48.55) * mm});
            skLineSegment(sketch, "E606", {"start": v(54.79, -48.55) * mm, "end": v(60.05, -45.21) * mm});
            skLineSegment(sketch, "E607", {"start": v(60.05, -45.21) * mm, "end": v(61.75, -43.8) * mm});
            skLineSegment(sketch, "E608", {"start": v(61.75, -43.8) * mm, "end": v(63.44, -41.69) * mm});
            skLineSegment(sketch, "E609", {"start": v(63.44, -41.69) * mm, "end": v(63.89, -40.38) * mm});
            skLineSegment(sketch, "E610", {"start": v(63.89, -40.38) * mm, "end": v(64, -39.24) * mm});
            skLineSegment(sketch, "E611", {"start": v(57.56, -41.7) * mm, "end": v(58.19, -41.5) * mm});
            skLineSegment(sketch, "E612", {"start": v(58.19, -41.5) * mm, "end": v(57.05, -43.48) * mm});
            skLineSegment(sketch, "E613", {"start": v(57.05, -43.48) * mm, "end": v(55.22, -44.97) * mm});
            skLineSegment(sketch, "E614", {"start": v(55.22, -44.97) * mm, "end": v(53.62, -45.6) * mm});
            skLineSegment(sketch, "E615", {"start": v(53.62, -45.6) * mm, "end": v(51.05, -46.03) * mm});
            skLineSegment(sketch, "E616", {"start": v(51.05, -46.03) * mm, "end": v(47.79, -46.06) * mm});
            skLineSegment(sketch, "E617", {"start": v(47.79, -46.06) * mm, "end": v(53.3, -45.44) * mm});
            skLineSegment(sketch, "E618", {"start": v(53.3, -45.44) * mm, "end": v(54.78, -44.87) * mm});
            skLineSegment(sketch, "E619", {"start": v(54.78, -44.87) * mm, "end": v(55.9, -44.07) * mm});
            skLineSegment(sketch, "E620", {"start": v(55.9, -44.07) * mm, "end": v(57.56, -41.7) * mm});
            skLineSegment(sketch, "E621", {"start": v(73.7, -37.8) * mm, "end": v(74.16, -37.78) * mm});
            skLineSegment(sketch, "E622", {"start": v(74.16, -37.78) * mm, "end": v(73.4, -36.23) * mm});
            skLineSegment(sketch, "E623", {"start": v(73.4, -36.23) * mm, "end": v(72.39, -35.15) * mm});
            skLineSegment(sketch, "E624", {"start": v(72.39, -35.15) * mm, "end": v(71.08, -34.4) * mm});
            skLineSegment(sketch, "E625", {"start": v(71.08, -34.4) * mm, "end": v(67.4, -33.03) * mm});
            skLineSegment(sketch, "E626", {"start": v(67.4, -33.03) * mm, "end": v(71.5, -34.9) * mm});
            skLineSegment(sketch, "E627", {"start": v(71.5, -34.9) * mm, "end": v(72.84, -36) * mm});
            skLineSegment(sketch, "E628", {"start": v(72.84, -36) * mm, "end": v(73.7, -37.8) * mm});
            skLineSegment(sketch, "E629", {"start": v(68.57, -37.34) * mm, "end": v(69, -37.36) * mm});
            skLineSegment(sketch, "E630", {"start": v(69, -37.36) * mm, "end": v(68.26, -35.77) * mm});
            skLineSegment(sketch, "E631", {"start": v(68.26, -35.77) * mm, "end": v(67.24, -34.69) * mm});
            skLineSegment(sketch, "E632", {"start": v(67.24, -34.69) * mm, "end": v(65.93, -33.95) * mm});
            skLineSegment(sketch, "E633", {"start": v(65.93, -33.95) * mm, "end": v(62.26, -32.57) * mm});
            skLineSegment(sketch, "E634", {"start": v(62.26, -32.57) * mm, "end": v(66.36, -34.43) * mm});
            skLineSegment(sketch, "E635", {"start": v(66.36, -34.43) * mm, "end": v(67.7, -35.55) * mm});
            skLineSegment(sketch, "E636", {"start": v(67.7, -35.55) * mm, "end": v(68.57, -37.34) * mm});
            skLineSegment(sketch, "E637", {"start": v(64.18, -37.66) * mm, "end": v(64.65, -37.58) * mm});
            skLineSegment(sketch, "E638", {"start": v(64.65, -37.58) * mm, "end": v(63.73, -36.35) * mm});
            skLineSegment(sketch, "E639", {"start": v(63.73, -36.35) * mm, "end": v(62.56, -35.44) * mm});
            skLineSegment(sketch, "E640", {"start": v(62.56, -35.44) * mm, "end": v(61.15, -34.91) * mm});
            skLineSegment(sketch, "E641", {"start": v(61.15, -34.91) * mm, "end": v(57.31, -34.13) * mm});
            skLineSegment(sketch, "E642", {"start": v(57.31, -34.13) * mm, "end": v(61.65, -35.32) * mm});
            skLineSegment(sketch, "E643", {"start": v(61.65, -35.32) * mm, "end": v(63.14, -36.21) * mm});
            skLineSegment(sketch, "E644", {"start": v(63.14, -36.21) * mm, "end": v(64.18, -37.66) * mm});
            skLineSegment(sketch, "E645", {"start": v(60.25, -39) * mm, "end": v(60.64, -38.83) * mm});
            skLineSegment(sketch, "E646", {"start": v(60.64, -38.83) * mm, "end": v(59.69, -37.83) * mm});
            skLineSegment(sketch, "E647", {"start": v(59.69, -37.83) * mm, "end": v(58.37, -37.23) * mm});
            skLineSegment(sketch, "E648", {"start": v(58.37, -37.23) * mm, "end": v(56.9, -37.05) * mm});
            skLineSegment(sketch, "E649", {"start": v(56.9, -37.05) * mm, "end": v(53.37, -36.9) * mm});
            skLineSegment(sketch, "E650", {"start": v(53.37, -36.9) * mm, "end": v(55.5, -37.2) * mm});
            skLineSegment(sketch, "E651", {"start": v(55.5, -37.2) * mm, "end": v(57.5, -37.3) * mm});
            skLineSegment(sketch, "E652", {"start": v(57.5, -37.3) * mm, "end": v(59.13, -37.86) * mm});
            skLineSegment(sketch, "E653", {"start": v(59.13, -37.86) * mm, "end": v(60.25, -39) * mm});
            skLineSegment(sketch, "E654", {"start": v(54.93, -41.34) * mm, "end": v(55.3, -41.26) * mm});
            skLineSegment(sketch, "E655", {"start": v(55.3, -41.26) * mm, "end": v(54.74, -40.16) * mm});
            skLineSegment(sketch, "E656", {"start": v(54.74, -40.16) * mm, "end": v(53.89, -39.25) * mm});
            skLineSegment(sketch, "E657", {"start": v(53.89, -39.25) * mm, "end": v(52.79, -38.63) * mm});
            skLineSegment(sketch, "E658", {"start": v(52.79, -38.63) * mm, "end": v(49.95, -37.67) * mm});
            skLineSegment(sketch, "E659", {"start": v(49.95, -37.67) * mm, "end": v(51.5, -38.4) * mm});
            skLineSegment(sketch, "E660", {"start": v(51.5, -38.4) * mm, "end": v(53.15, -39.03) * mm});
            skLineSegment(sketch, "E661", {"start": v(53.15, -39.03) * mm, "end": v(54.27, -39.97) * mm});
            skLineSegment(sketch, "E662", {"start": v(54.27, -39.97) * mm, "end": v(54.93, -41.34) * mm});
            skLineSegment(sketch, "E663", {"start": v(86.63, -28.88) * mm, "end": v(89.9, -27.92) * mm});
            skLineSegment(sketch, "E664", {"start": v(89.9, -27.92) * mm, "end": v(91.5, -26.98) * mm});
            skLineSegment(sketch, "E665", {"start": v(91.5, -26.98) * mm, "end": v(92.75, -25.77) * mm});
            skLineSegment(sketch, "E666", {"start": v(92.75, -25.77) * mm, "end": v(94.74, -21.86) * mm});
            skLineSegment(sketch, "E667", {"start": v(94.74, -21.86) * mm, "end": v(95.63, -18.31) * mm});
            skLineSegment(sketch, "E668", {"start": v(95.63, -18.31) * mm, "end": v(95.95, -15.06) * mm});
            skLineSegment(sketch, "E669", {"start": v(95.95, -15.06) * mm, "end": v(95.95, -10.6) * mm});
            skLineSegment(sketch, "E670", {"start": v(95.95, -10.6) * mm, "end": v(95.15, -6.43) * mm});
            skLineSegment(sketch, "E671", {"start": v(95.15, -6.43) * mm, "end": v(93.3, -1.17) * mm});
            skLineSegment(sketch, "E672", {"start": v(93.3, -1.17) * mm, "end": v(92.02, 1.2) * mm});
            skLineSegment(sketch, "E673", {"start": v(92.02, 1.2) * mm, "end": v(90.4, 3.43) * mm});
            skLineSegment(sketch, "E674", {"start": v(90.4, 3.43) * mm, "end": v(88.74, 5.29) * mm});
            skLineSegment(sketch, "E675", {"start": v(88.74, 5.29) * mm, "end": v(87.18, 6.58) * mm});
            skLineSegment(sketch, "E676", {"start": v(87.18, 6.58) * mm, "end": v(84.67, 8.05) * mm});
            skLineSegment(sketch, "E677", {"start": v(84.67, 8.05) * mm, "end": v(80.74, 9.63) * mm});
            skLineSegment(sketch, "E678", {"start": v(80.74, 9.63) * mm, "end": v(81.24, 8.2) * mm});
            skLineSegment(sketch, "E679", {"start": v(81.24, 8.2) * mm, "end": v(82.2, 5.74) * mm});
            skLineSegment(sketch, "E680", {"start": v(82.2, 5.74) * mm, "end": v(82.98, 0) * mm});
            skLineSegment(sketch, "E681", {"start": v(82.98, 0) * mm, "end": v(82.29, -4.41) * mm});
            skLineSegment(sketch, "E682", {"start": v(82.29, -4.41) * mm, "end": v(80.48, -8.24) * mm});
            skLineSegment(sketch, "E683", {"start": v(80.48, -8.24) * mm, "end": v(79.67, -9.78) * mm});
            skLineSegment(sketch, "E684", {"start": v(79.67, -9.78) * mm, "end": v(79.11, -11.43) * mm});
            skLineSegment(sketch, "E685", {"start": v(79.11, -11.43) * mm, "end": v(78.42, -14.6) * mm});
            skLineSegment(sketch, "E686", {"start": v(78.42, -14.6) * mm, "end": v(78.43, -17.83) * mm});
            skLineSegment(sketch, "E687", {"start": v(78.43, -17.83) * mm, "end": v(79.26, -22.05) * mm});
            skLineSegment(sketch, "E688", {"start": v(79.26, -22.05) * mm, "end": v(80.01, -23.83) * mm});
            skLineSegment(sketch, "E689", {"start": v(80.01, -23.83) * mm, "end": v(81.55, -25.9) * mm});
            skLineSegment(sketch, "E690", {"start": v(81.55, -25.9) * mm, "end": v(83.6, -27.67) * mm});
            skLineSegment(sketch, "E691", {"start": v(83.6, -27.67) * mm, "end": v(85.63, -28.84) * mm});
            skLineSegment(sketch, "E692", {"start": v(85.63, -28.84) * mm, "end": v(87.35, -34.05) * mm});
            skLineSegment(sketch, "E693", {"start": v(87.35, -34.05) * mm, "end": v(88.84, -38) * mm});
            skLineSegment(sketch, "E694", {"start": v(88.84, -38) * mm, "end": v(91.8, -38.02) * mm});
            skLineSegment(sketch, "E695", {"start": v(91.8, -38.02) * mm, "end": v(90.17, -36.82) * mm});
            skLineSegment(sketch, "E696", {"start": v(90.17, -36.82) * mm, "end": v(88.53, -34.5) * mm});
            skLineSegment(sketch, "E697", {"start": v(88.53, -34.5) * mm, "end": v(87.23, -31.66) * mm});
            skLineSegment(sketch, "E698", {"start": v(87.23, -31.66) * mm, "end": v(86.63, -28.88) * mm});
            skLineSegment(sketch, "E699", {"start": v(86.63, -28.88) * mm, "end": v(86.63, -28.88) * mm});
            skLineSegment(sketch, "E700", {"start": v(86.1, -27.6) * mm, "end": v(84.88, -22.3) * mm});
            skLineSegment(sketch, "E701", {"start": v(84.88, -22.3) * mm, "end": v(84.56, -18.15) * mm});
            skLineSegment(sketch, "E702", {"start": v(84.56, -18.15) * mm, "end": v(84.8, -15.7) * mm});
            skLineSegment(sketch, "E703", {"start": v(84.8, -15.7) * mm, "end": v(86.26, -10.9) * mm});
            skLineSegment(sketch, "E704", {"start": v(86.26, -10.9) * mm, "end": v(87.31, -8.33) * mm});
            skLineSegment(sketch, "E705", {"start": v(87.31, -8.33) * mm, "end": v(88, -4.55) * mm});
            skLineSegment(sketch, "E706", {"start": v(88, -4.55) * mm, "end": v(87.98, -1.6) * mm});
            skLineSegment(sketch, "E707", {"start": v(87.98, -1.6) * mm, "end": v(87.15, 1.43) * mm});
            skLineSegment(sketch, "E708", {"start": v(87.15, 1.43) * mm, "end": v(86.15, 3.57) * mm});
            skLineSegment(sketch, "E709", {"start": v(86.15, 3.57) * mm, "end": v(84.5, 6.12) * mm});
            skLineSegment(sketch, "E710", {"start": v(84.5, 6.12) * mm, "end": v(82.16, 8.57) * mm});
            skLineSegment(sketch, "E711", {"start": v(82.16, 8.57) * mm, "end": v(85.33, 4.32) * mm});
            skLineSegment(sketch, "E712", {"start": v(85.33, 4.32) * mm, "end": v(87.34, -0.66) * mm});
            skLineSegment(sketch, "E713", {"start": v(87.34, -0.66) * mm, "end": v(87.56, -2.92) * mm});
            skLineSegment(sketch, "E714", {"start": v(87.56, -2.92) * mm, "end": v(87.35, -5.33) * mm});
            skLineSegment(sketch, "E715", {"start": v(87.35, -5.33) * mm, "end": v(85.95, -10.32) * mm});
            skLineSegment(sketch, "E716", {"start": v(85.95, -10.32) * mm, "end": v(84.5, -14.2) * mm});
            skLineSegment(sketch, "E717", {"start": v(84.5, -14.2) * mm, "end": v(84.03, -16.14) * mm});
            skLineSegment(sketch, "E718", {"start": v(84.03, -16.14) * mm, "end": v(83.94, -17.86) * mm});
            skLineSegment(sketch, "E719", {"start": v(83.94, -17.86) * mm, "end": v(83.94, -20.4) * mm});
            skLineSegment(sketch, "E720", {"start": v(83.94, -20.4) * mm, "end": v(84.28, -22.86) * mm});
            skLineSegment(sketch, "E721", {"start": v(84.28, -22.86) * mm, "end": v(85.34, -27.7) * mm});
            skLineSegment(sketch, "E722", {"start": v(85.34, -27.7) * mm, "end": v(86.1, -27.6) * mm});
            skLineSegment(sketch, "E723", {"start": v(86.22, -26.02) * mm, "end": v(86.31, -26.5) * mm});
            skLineSegment(sketch, "E724", {"start": v(86.31, -26.5) * mm, "end": v(87.35, -26.44) * mm});
            skLineSegment(sketch, "E725", {"start": v(87.35, -26.44) * mm, "end": v(88.44, -26.07) * mm});
            skLineSegment(sketch, "E726", {"start": v(88.44, -26.07) * mm, "end": v(90.32, -25.07) * mm});
            skLineSegment(sketch, "E727", {"start": v(90.32, -25.07) * mm, "end": v(91.83, -23.53) * mm});
            skLineSegment(sketch, "E728", {"start": v(91.83, -23.53) * mm, "end": v(95.1, -18.95) * mm});
            skLineSegment(sketch, "E729", {"start": v(95.1, -18.95) * mm, "end": v(91, -23.94) * mm});
            skLineSegment(sketch, "E730", {"start": v(91, -23.94) * mm, "end": v(88.96, -25.38) * mm});
            skLineSegment(sketch, "E731", {"start": v(88.96, -25.38) * mm, "end": v(86.22, -26.02) * mm});
            skLineSegment(sketch, "E732", {"start": v(85.24, -21.4) * mm, "end": v(85.24, -21.8) * mm});
            skLineSegment(sketch, "E733", {"start": v(85.24, -21.8) * mm, "end": v(85.18, -21.86) * mm});
            skLineSegment(sketch, "E734", {"start": v(85.18, -21.86) * mm, "end": v(86.3, -21.77) * mm});
            skLineSegment(sketch, "E735", {"start": v(86.3, -21.77) * mm, "end": v(87.46, -21.36) * mm});
            skLineSegment(sketch, "E736", {"start": v(87.46, -21.36) * mm, "end": v(89.51, -20) * mm});
            skLineSegment(sketch, "E737", {"start": v(89.51, -20) * mm, "end": v(91.17, -18.12) * mm});
            skLineSegment(sketch, "E738", {"start": v(91.17, -18.12) * mm, "end": v(94.66, -13.1) * mm});
            skLineSegment(sketch, "E739", {"start": v(94.66, -13.1) * mm, "end": v(90.27, -18.77) * mm});
            skLineSegment(sketch, "E740", {"start": v(90.27, -18.77) * mm, "end": v(87.95, -20.64) * mm});
            skLineSegment(sketch, "E741", {"start": v(87.95, -20.64) * mm, "end": v(85.24, -21.4) * mm});
            skLineSegment(sketch, "E742", {"start": v(85.35, -15.6) * mm, "end": v(85.2, -16.12) * mm});
            skLineSegment(sketch, "E743", {"start": v(85.2, -16.12) * mm, "end": v(86.82, -15.77) * mm});
            skLineSegment(sketch, "E744", {"start": v(86.82, -15.77) * mm, "end": v(88.3, -15.11) * mm});
            skLineSegment(sketch, "E745", {"start": v(88.3, -15.11) * mm, "end": v(89.78, -13.73) * mm});
            skLineSegment(sketch, "E746", {"start": v(89.78, -13.73) * mm, "end": v(91.3, -11.75) * mm});
            skLineSegment(sketch, "E747", {"start": v(91.3, -11.75) * mm, "end": v(91.79, -10.82) * mm});
            skLineSegment(sketch, "E748", {"start": v(91.79, -10.82) * mm, "end": v(94.2, -5.96) * mm});
            skLineSegment(sketch, "E749", {"start": v(94.2, -5.96) * mm, "end": v(91.12, -11.38) * mm});
            skLineSegment(sketch, "E750", {"start": v(91.12, -11.38) * mm, "end": v(89.78, -13.14) * mm});
            skLineSegment(sketch, "E751", {"start": v(89.78, -13.14) * mm, "end": v(87.76, -14.94) * mm});
            skLineSegment(sketch, "E752", {"start": v(87.76, -14.94) * mm, "end": v(86.48, -15.45) * mm});
            skLineSegment(sketch, "E753", {"start": v(86.48, -15.45) * mm, "end": v(85.35, -15.6) * mm});
            skLineSegment(sketch, "E754", {"start": v(87.5, -9.06) * mm, "end": v(87.3, -9.7) * mm});
            skLineSegment(sketch, "E755", {"start": v(87.3, -9.7) * mm, "end": v(89.24, -8.46) * mm});
            skLineSegment(sketch, "E756", {"start": v(89.24, -8.46) * mm, "end": v(90.64, -6.57) * mm});
            skLineSegment(sketch, "E757", {"start": v(90.64, -6.57) * mm, "end": v(91.19, -4.93) * mm});
            skLineSegment(sketch, "E758", {"start": v(91.19, -4.93) * mm, "end": v(91.5, -2.35) * mm});
            skLineSegment(sketch, "E759", {"start": v(91.5, -2.35) * mm, "end": v(91.36, 0.91) * mm});
            skLineSegment(sketch, "E760", {"start": v(91.36, 0.91) * mm, "end": v(91.02, -4.63) * mm});
            skLineSegment(sketch, "E761", {"start": v(91.02, -4.63) * mm, "end": v(90.52, -6.13) * mm});
            skLineSegment(sketch, "E762", {"start": v(90.52, -6.13) * mm, "end": v(89.78, -7.28) * mm});
            skLineSegment(sketch, "E763", {"start": v(89.78, -7.28) * mm, "end": v(87.5, -9.06) * mm});
            skLineSegment(sketch, "E764", {"start": v(84.38, -25.37) * mm, "end": v(84.37, -25.83) * mm});
            skLineSegment(sketch, "E765", {"start": v(84.37, -25.83) * mm, "end": v(82.8, -25.15) * mm});
            skLineSegment(sketch, "E766", {"start": v(82.8, -25.15) * mm, "end": v(81.66, -24.19) * mm});
            skLineSegment(sketch, "E767", {"start": v(81.66, -24.19) * mm, "end": v(80.86, -22.91) * mm});
            skLineSegment(sketch, "E768", {"start": v(80.86, -22.91) * mm, "end": v(79.3, -19.31) * mm});
            skLineSegment(sketch, "E769", {"start": v(79.3, -19.31) * mm, "end": v(81.36, -23.32) * mm});
            skLineSegment(sketch, "E770", {"start": v(81.36, -23.32) * mm, "end": v(82.54, -24.6) * mm});
            skLineSegment(sketch, "E771", {"start": v(82.54, -24.6) * mm, "end": v(84.38, -25.37) * mm});
            skLineSegment(sketch, "E772", {"start": v(84.38, -25.37) * mm, "end": v(84.38, -25.37) * mm});
            skLineSegment(sketch, "E773", {"start": v(83.67, -20.27) * mm, "end": v(83.7, -20.7) * mm});
            skLineSegment(sketch, "E774", {"start": v(83.7, -20.7) * mm, "end": v(82.09, -20.03) * mm});
            skLineSegment(sketch, "E775", {"start": v(82.09, -20.03) * mm, "end": v(80.95, -19.07) * mm});
            skLineSegment(sketch, "E776", {"start": v(80.95, -19.07) * mm, "end": v(80.15, -17.8) * mm});
            skLineSegment(sketch, "E777", {"start": v(80.15, -17.8) * mm, "end": v(78.6, -14.2) * mm});
            skLineSegment(sketch, "E778", {"start": v(78.6, -14.2) * mm, "end": v(80.66, -18.2) * mm});
            skLineSegment(sketch, "E779", {"start": v(80.66, -18.2) * mm, "end": v(81.83, -19.48) * mm});
            skLineSegment(sketch, "E780", {"start": v(81.83, -19.48) * mm, "end": v(83.67, -20.27) * mm});
            skLineSegment(sketch, "E781", {"start": v(83.77, -15.87) * mm, "end": v(83.71, -16.34) * mm});
            skLineSegment(sketch, "E782", {"start": v(83.71, -16.34) * mm, "end": v(82.44, -15.48) * mm});
            skLineSegment(sketch, "E783", {"start": v(82.44, -15.48) * mm, "end": v(81.47, -14.36) * mm});
            skLineSegment(sketch, "E784", {"start": v(81.47, -14.36) * mm, "end": v(80.88, -12.98) * mm});
            skLineSegment(sketch, "E785", {"start": v(80.88, -12.98) * mm, "end": v(79.91, -9.18) * mm});
            skLineSegment(sketch, "E786", {"start": v(79.91, -9.18) * mm, "end": v(81.32, -13.45) * mm});
            skLineSegment(sketch, "E787", {"start": v(81.32, -13.45) * mm, "end": v(82.28, -14.9) * mm});
            skLineSegment(sketch, "E788", {"start": v(82.28, -14.9) * mm, "end": v(83.77, -15.87) * mm});
            skLineSegment(sketch, "E789", {"start": v(84.93, -11.88) * mm, "end": v(84.77, -12.27) * mm});
            skLineSegment(sketch, "E790", {"start": v(84.77, -12.27) * mm, "end": v(83.72, -11.37) * mm});
            skLineSegment(sketch, "E791", {"start": v(83.72, -11.37) * mm, "end": v(83.06, -10.08) * mm});
            skLineSegment(sketch, "E792", {"start": v(83.06, -10.08) * mm, "end": v(82.81, -8.64) * mm});
            skLineSegment(sketch, "E793", {"start": v(82.81, -8.64) * mm, "end": v(82.48, -5.11) * mm});
            skLineSegment(sketch, "E794", {"start": v(82.48, -5.11) * mm, "end": v(82.9, -7.21) * mm});
            skLineSegment(sketch, "E795", {"start": v(82.9, -7.21) * mm, "end": v(83.08, -9.22) * mm});
            skLineSegment(sketch, "E796", {"start": v(83.08, -9.22) * mm, "end": v(83.73, -10.82) * mm});
            skLineSegment(sketch, "E797", {"start": v(83.73, -10.82) * mm, "end": v(84.93, -11.88) * mm});
            skLineSegment(sketch, "E798", {"start": v(87, -6.45) * mm, "end": v(86.94, -6.81) * mm});
            skLineSegment(sketch, "E799", {"start": v(86.94, -6.81) * mm, "end": v(85.81, -6.32) * mm});
            skLineSegment(sketch, "E800", {"start": v(85.81, -6.32) * mm, "end": v(84.86, -5.51) * mm});
            skLineSegment(sketch, "E801", {"start": v(84.86, -5.51) * mm, "end": v(84.19, -4.44) * mm});
            skLineSegment(sketch, "E802", {"start": v(84.19, -4.44) * mm, "end": v(83.1, -1.66) * mm});
            skLineSegment(sketch, "E803", {"start": v(83.1, -1.66) * mm, "end": v(83.9, -3.18) * mm});
            skLineSegment(sketch, "E804", {"start": v(83.9, -3.18) * mm, "end": v(84.61, -4.78) * mm});
            skLineSegment(sketch, "E805", {"start": v(84.61, -4.78) * mm, "end": v(85.6, -5.85) * mm});
            skLineSegment(sketch, "E806", {"start": v(85.6, -5.85) * mm, "end": v(87, -6.45) * mm});
            skLineSegment(sketch, "E807", {"start": v(75.75, 57.9) * mm, "end": v(73.87, 55.59) * mm});
            skLineSegment(sketch, "E808", {"start": v(73.87, 55.59) * mm, "end": v(71.67, 53.58) * mm});
            skLineSegment(sketch, "E809", {"start": v(71.67, 53.58) * mm, "end": v(69.2, 51.9) * mm});
            skLineSegment(sketch, "E810", {"start": v(69.2, 51.9) * mm, "end": v(66.5, 50.62) * mm});
            skLineSegment(sketch, "E811", {"start": v(66.5, 50.62) * mm, "end": v(63.24, 49.65) * mm});
            skLineSegment(sketch, "E812", {"start": v(63.24, 49.65) * mm, "end": v(59.84, 49.17) * mm});
            skLineSegment(sketch, "E813", {"start": v(59.84, 49.17) * mm, "end": v(56.39, 49.12) * mm});
            skLineSegment(sketch, "E814", {"start": v(56.39, 49.12) * mm, "end": v(52.93, 49.44) * mm});
            skLineSegment(sketch, "E815", {"start": v(52.93, 49.44) * mm, "end": v(46.13, 50.87) * mm});
            skLineSegment(sketch, "E816", {"start": v(46.13, 50.87) * mm, "end": v(39.4, 52.87) * mm});
            skLineSegment(sketch, "E817", {"start": v(39.4, 52.87) * mm, "end": v(32.61, 54.87) * mm});
            skLineSegment(sketch, "E818", {"start": v(32.61, 54.87) * mm, "end": v(25.64, 56.26) * mm});
            skLineSegment(sketch, "E819", {"start": v(25.64, 56.26) * mm, "end": v(22.07, 56.53) * mm});
            skLineSegment(sketch, "E820", {"start": v(22.07, 56.53) * mm, "end": v(18.47, 56.4) * mm});
            skLineSegment(sketch, "E821", {"start": v(18.47, 56.4) * mm, "end": v(14.93, 55.83) * mm});
            skLineSegment(sketch, "E822", {"start": v(14.93, 55.83) * mm, "end": v(11.5, 54.71) * mm});
            skLineSegment(sketch, "E823", {"start": v(11.5, 54.71) * mm, "end": v(8.2, 52.96) * mm});
            skLineSegment(sketch, "E824", {"start": v(8.2, 52.96) * mm, "end": v(5.25, 50.64) * mm});
            skLineSegment(sketch, "E825", {"start": v(5.25, 50.64) * mm, "end": v(6.06, 49.78) * mm});
            skLineSegment(sketch, "E826", {"start": v(6.06, 49.78) * mm, "end": v(8.84, 51.97) * mm});
            skLineSegment(sketch, "E827", {"start": v(8.84, 51.97) * mm, "end": v(11.96, 53.62) * mm});
            skLineSegment(sketch, "E828", {"start": v(11.96, 53.62) * mm, "end": v(15.2, 54.68) * mm});
            skLineSegment(sketch, "E829", {"start": v(15.2, 54.68) * mm, "end": v(18.59, 55.23) * mm});
            skLineSegment(sketch, "E830", {"start": v(18.59, 55.23) * mm, "end": v(22.04, 55.34) * mm});
            skLineSegment(sketch, "E831", {"start": v(22.04, 55.34) * mm, "end": v(25.5, 55.08) * mm});
            skLineSegment(sketch, "E832", {"start": v(25.5, 55.08) * mm, "end": v(32.31, 53.72) * mm});
            skLineSegment(sketch, "E833", {"start": v(32.31, 53.72) * mm, "end": v(39.04, 51.74) * mm});
            skLineSegment(sketch, "E834", {"start": v(39.04, 51.74) * mm, "end": v(45.82, 49.72) * mm});
            skLineSegment(sketch, "E835", {"start": v(45.82, 49.72) * mm, "end": v(52.77, 48.26) * mm});
            skLineSegment(sketch, "E836", {"start": v(52.77, 48.26) * mm, "end": v(56.34, 47.94) * mm});
            skLineSegment(sketch, "E837", {"start": v(56.34, 47.94) * mm, "end": v(59.93, 48) * mm});
            skLineSegment(sketch, "E838", {"start": v(59.93, 48) * mm, "end": v(63.49, 48.5) * mm});
            skLineSegment(sketch, "E839", {"start": v(63.49, 48.5) * mm, "end": v(66.94, 49.52) * mm});
            skLineSegment(sketch, "E840", {"start": v(66.94, 49.52) * mm, "end": v(69.78, 50.88) * mm});
            skLineSegment(sketch, "E841", {"start": v(69.78, 50.88) * mm, "end": v(72.4, 52.64) * mm});
            skLineSegment(sketch, "E842", {"start": v(72.4, 52.64) * mm, "end": v(74.73, 54.77) * mm});
            skLineSegment(sketch, "E843", {"start": v(74.73, 54.77) * mm, "end": v(76.72, 57.22) * mm});
            skLineSegment(sketch, "E844", {"start": v(76.72, 57.22) * mm, "end": v(75.75, 57.9) * mm});
            skLineSegment(sketch, "E845", {"start": v(-40.38, -40.06) * mm, "end": v(-39.06, -40.27) * mm});
            skLineSegment(sketch, "E846", {"start": v(-39.06, -40.27) * mm, "end": v(-37.9, -40.87) * mm});
            skLineSegment(sketch, "E847", {"start": v(-37.9, -40.87) * mm, "end": v(-36.75, -42.32) * mm});
            skLineSegment(sketch, "E848", {"start": v(-36.75, -42.32) * mm, "end": v(-36.3, -44.08) * mm});
            skLineSegment(sketch, "E849", {"start": v(-36.3, -44.08) * mm, "end": v(-36.52, -45.31) * mm});
            skLineSegment(sketch, "E850", {"start": v(-36.52, -45.31) * mm, "end": v(-37.17, -46.4) * mm});
            skLineSegment(sketch, "E851", {"start": v(-37.17, -46.4) * mm, "end": v(-39.07, -47.66) * mm});
            skLineSegment(sketch, "E852", {"start": v(-39.07, -47.66) * mm, "end": v(-40.52, -47.9) * mm});
            skLineSegment(sketch, "E853", {"start": v(-40.52, -47.9) * mm, "end": v(-42.35, -47.5) * mm});
            skLineSegment(sketch, "E854", {"start": v(-42.35, -47.5) * mm, "end": v(-44, -46.04) * mm});
            skLineSegment(sketch, "E855", {"start": v(-44, -46.04) * mm, "end": v(-44.57, -43.98) * mm});
            skLineSegment(sketch, "E856", {"start": v(-44.57, -43.98) * mm, "end": v(-44.39, -42.74) * mm});
            skLineSegment(sketch, "E857", {"start": v(-44.39, -42.74) * mm, "end": v(-43.83, -41.66) * mm});
            skLineSegment(sketch, "E858", {"start": v(-43.83, -41.66) * mm, "end": v(-42.05, -40.35) * mm});
            skLineSegment(sketch, "E859", {"start": v(-42.05, -40.35) * mm, "end": v(-40.38, -40.06) * mm});
            skLineSegment(sketch, "E860", {"start": v(-40.9, -41.65) * mm, "end": v(-41.64, -42.06) * mm});
            skLineSegment(sketch, "E861", {"start": v(-41.64, -42.06) * mm, "end": v(-41.85, -42.8) * mm});
            skLineSegment(sketch, "E862", {"start": v(-41.85, -42.8) * mm, "end": v(-41.6, -44.24) * mm});
            skLineSegment(sketch, "E863", {"start": v(-41.6, -44.24) * mm, "end": v(-40.96, -45.69) * mm});
            skLineSegment(sketch, "E864", {"start": v(-40.96, -45.69) * mm, "end": v(-40.54, -46.12) * mm});
            skLineSegment(sketch, "E865", {"start": v(-40.54, -46.12) * mm, "end": v(-40.03, -46.28) * mm});
            skLineSegment(sketch, "E866", {"start": v(-40.03, -46.28) * mm, "end": v(-39.35, -45.96) * mm});
            skLineSegment(sketch, "E867", {"start": v(-39.35, -45.96) * mm, "end": v(-39.1, -45.14) * mm});
            skLineSegment(sketch, "E868", {"start": v(-39.1, -45.14) * mm, "end": v(-39.3, -43.7) * mm});
            skLineSegment(sketch, "E869", {"start": v(-39.3, -43.7) * mm, "end": v(-39.87, -42.38) * mm});
            skLineSegment(sketch, "E870", {"start": v(-39.87, -42.38) * mm, "end": v(-40.35, -41.85) * mm});
            skLineSegment(sketch, "E871", {"start": v(-40.35, -41.85) * mm, "end": v(-40.9, -41.65) * mm});
            skLineSegment(sketch, "E872", {"start": v(-32.56, -43.7) * mm, "end": v(-32.56, -45.56) * mm});
            skLineSegment(sketch, "E873", {"start": v(-32.56, -45.56) * mm, "end": v(-32.4, -46.1) * mm});
            skLineSegment(sketch, "E874", {"start": v(-32.4, -46.1) * mm, "end": v(-31.98, -46.3) * mm});
            skLineSegment(sketch, "E875", {"start": v(-31.98, -46.3) * mm, "end": v(-31.4, -46.11) * mm});
            skLineSegment(sketch, "E876", {"start": v(-31.4, -46.11) * mm, "end": v(-31.24, -46.06) * mm});
            skLineSegment(sketch, "E877", {"start": v(-31.24, -46.06) * mm, "end": v(-31, -46.22) * mm});
            skLineSegment(sketch, "E878", {"start": v(-31, -46.22) * mm, "end": v(-30.9, -46.57) * mm});
            skLineSegment(sketch, "E879", {"start": v(-30.9, -46.57) * mm, "end": v(-31.27, -47.22) * mm});
            skLineSegment(sketch, "E880", {"start": v(-31.27, -47.22) * mm, "end": v(-33.16, -47.9) * mm});
            skLineSegment(sketch, "E881", {"start": v(-33.16, -47.9) * mm, "end": v(-34.58, -47.4) * mm});
            skLineSegment(sketch, "E882", {"start": v(-34.58, -47.4) * mm, "end": v(-35.11, -46.08) * mm});
            skLineSegment(sketch, "E883", {"start": v(-35.11, -46.08) * mm, "end": v(-35.11, -43.53) * mm});
            skLineSegment(sketch, "E884", {"start": v(-35.11, -43.53) * mm, "end": v(-35.15, -43.38) * mm});
            skLineSegment(sketch, "E885", {"start": v(-35.15, -43.38) * mm, "end": v(-35.3, -43.34) * mm});
            skLineSegment(sketch, "E886", {"start": v(-35.3, -43.34) * mm, "end": v(-35.87, -43.34) * mm});
            skLineSegment(sketch, "E887", {"start": v(-35.87, -43.34) * mm, "end": v(-36.07, -43.3) * mm});
            skLineSegment(sketch, "E888", {"start": v(-36.07, -43.3) * mm, "end": v(-36.12, -43.05) * mm});
            skLineSegment(sketch, "E889", {"start": v(-36.12, -43.05) * mm, "end": v(-36.12, -42.8) * mm});
            skLineSegment(sketch, "E890", {"start": v(-36.12, -42.8) * mm, "end": v(-36, -42.56) * mm});
            skLineSegment(sketch, "E891", {"start": v(-36, -42.56) * mm, "end": v(-33.47, -40.97) * mm});
            skLineSegment(sketch, "E892", {"start": v(-33.47, -40.97) * mm, "end": v(-33.23, -40.92) * mm});
            skLineSegment(sketch, "E893", {"start": v(-33.23, -40.92) * mm, "end": v(-32.79, -40.92) * mm});
            skLineSegment(sketch, "E894", {"start": v(-32.79, -40.92) * mm, "end": v(-32.6, -41) * mm});
            skLineSegment(sketch, "E895", {"start": v(-32.6, -41) * mm, "end": v(-32.56, -41.24) * mm});
            skLineSegment(sketch, "E896", {"start": v(-32.56, -41.24) * mm, "end": v(-32.56, -41.98) * mm});
            skLineSegment(sketch, "E897", {"start": v(-32.56, -41.98) * mm, "end": v(-32.5, -42.2) * mm});
            skLineSegment(sketch, "E898", {"start": v(-32.5, -42.2) * mm, "end": v(-32.28, -42.25) * mm});
            skLineSegment(sketch, "E899", {"start": v(-32.28, -42.25) * mm, "end": v(-31.26, -42.25) * mm});
            skLineSegment(sketch, "E900", {"start": v(-31.26, -42.25) * mm, "end": v(-31, -42.32) * mm});
            skLineSegment(sketch, "E901", {"start": v(-31, -42.32) * mm, "end": v(-30.94, -42.64) * mm});
            skLineSegment(sketch, "E902", {"start": v(-30.94, -42.64) * mm, "end": v(-30.94, -42.96) * mm});
            skLineSegment(sketch, "E903", {"start": v(-30.94, -42.96) * mm, "end": v(-31.01, -43.33) * mm});
            skLineSegment(sketch, "E904", {"start": v(-31.01, -43.33) * mm, "end": v(-31.3, -43.43) * mm});
            skLineSegment(sketch, "E905", {"start": v(-31.3, -43.43) * mm, "end": v(-32.3, -43.43) * mm});
            skLineSegment(sketch, "E906", {"start": v(-32.3, -43.43) * mm, "end": v(-32.5, -43.49) * mm});
            skLineSegment(sketch, "E907", {"start": v(-32.5, -43.49) * mm, "end": v(-32.56, -43.7) * mm});
            skLineSegment(sketch, "E908", {"start": v(-27.33, -43.7) * mm, "end": v(-27.33, -45.56) * mm});
            skLineSegment(sketch, "E909", {"start": v(-27.33, -45.56) * mm, "end": v(-27.17, -46.1) * mm});
            skLineSegment(sketch, "E910", {"start": v(-27.17, -46.1) * mm, "end": v(-26.75, -46.3) * mm});
            skLineSegment(sketch, "E911", {"start": v(-26.75, -46.3) * mm, "end": v(-26.18, -46.11) * mm});
            skLineSegment(sketch, "E912", {"start": v(-26.18, -46.11) * mm, "end": v(-26.02, -46.06) * mm});
            skLineSegment(sketch, "E913", {"start": v(-26.02, -46.06) * mm, "end": v(-25.78, -46.22) * mm});
            skLineSegment(sketch, "E914", {"start": v(-25.78, -46.22) * mm, "end": v(-25.67, -46.57) * mm});
            skLineSegment(sketch, "E915", {"start": v(-25.67, -46.57) * mm, "end": v(-26.04, -47.22) * mm});
            skLineSegment(sketch, "E916", {"start": v(-26.04, -47.22) * mm, "end": v(-27.94, -47.9) * mm});
            skLineSegment(sketch, "E917", {"start": v(-27.94, -47.9) * mm, "end": v(-29.35, -47.4) * mm});
            skLineSegment(sketch, "E918", {"start": v(-29.35, -47.4) * mm, "end": v(-29.89, -46.08) * mm});
            skLineSegment(sketch, "E919", {"start": v(-29.89, -46.08) * mm, "end": v(-29.89, -43.53) * mm});
            skLineSegment(sketch, "E920", {"start": v(-29.89, -43.53) * mm, "end": v(-29.92, -43.38) * mm});
            skLineSegment(sketch, "E921", {"start": v(-29.92, -43.38) * mm, "end": v(-30.08, -43.34) * mm});
            skLineSegment(sketch, "E922", {"start": v(-30.08, -43.34) * mm, "end": v(-30.64, -43.34) * mm});
            skLineSegment(sketch, "E923", {"start": v(-30.64, -43.34) * mm, "end": v(-30.85, -43.3) * mm});
            skLineSegment(sketch, "E924", {"start": v(-30.85, -43.3) * mm, "end": v(-30.9, -43.05) * mm});
            skLineSegment(sketch, "E925", {"start": v(-30.9, -43.05) * mm, "end": v(-30.9, -42.8) * mm});
            skLineSegment(sketch, "E926", {"start": v(-30.9, -42.8) * mm, "end": v(-30.76, -42.56) * mm});
            skLineSegment(sketch, "E927", {"start": v(-30.76, -42.56) * mm, "end": v(-28.24, -40.97) * mm});
            skLineSegment(sketch, "E928", {"start": v(-28.24, -40.97) * mm, "end": v(-28, -40.92) * mm});
            skLineSegment(sketch, "E929", {"start": v(-28, -40.92) * mm, "end": v(-27.56, -40.92) * mm});
            skLineSegment(sketch, "E930", {"start": v(-27.56, -40.92) * mm, "end": v(-27.38, -41) * mm});
            skLineSegment(sketch, "E931", {"start": v(-27.38, -41) * mm, "end": v(-27.33, -41.24) * mm});
            skLineSegment(sketch, "E932", {"start": v(-27.33, -41.24) * mm, "end": v(-27.33, -41.98) * mm});
            skLineSegment(sketch, "E933", {"start": v(-27.33, -41.98) * mm, "end": v(-27.28, -42.2) * mm});
            skLineSegment(sketch, "E934", {"start": v(-27.28, -42.2) * mm, "end": v(-27.05, -42.25) * mm});
            skLineSegment(sketch, "E935", {"start": v(-27.05, -42.25) * mm, "end": v(-26.04, -42.25) * mm});
            skLineSegment(sketch, "E936", {"start": v(-26.04, -42.25) * mm, "end": v(-25.77, -42.32) * mm});
            skLineSegment(sketch, "E937", {"start": v(-25.77, -42.32) * mm, "end": v(-25.7, -42.64) * mm});
            skLineSegment(sketch, "E938", {"start": v(-25.7, -42.64) * mm, "end": v(-25.7, -42.96) * mm});
            skLineSegment(sketch, "E939", {"start": v(-25.7, -42.96) * mm, "end": v(-25.79, -43.33) * mm});
            skLineSegment(sketch, "E940", {"start": v(-25.79, -43.33) * mm, "end": v(-26.07, -43.43) * mm});
            skLineSegment(sketch, "E941", {"start": v(-26.07, -43.43) * mm, "end": v(-27.07, -43.43) * mm});
            skLineSegment(sketch, "E942", {"start": v(-27.07, -43.43) * mm, "end": v(-27.28, -43.49) * mm});
            skLineSegment(sketch, "E943", {"start": v(-27.28, -43.49) * mm, "end": v(-27.33, -43.7) * mm});
            skLineSegment(sketch, "E944", {"start": v(-22.02, -42.25) * mm, "end": v(-20.25, -42.77) * mm});
            skLineSegment(sketch, "E945", {"start": v(-20.25, -42.77) * mm, "end": v(-19.38, -43.75) * mm});
            skLineSegment(sketch, "E946", {"start": v(-19.38, -43.75) * mm, "end": v(-19.03, -45.06) * mm});
            skLineSegment(sketch, "E947", {"start": v(-19.03, -45.06) * mm, "end": v(-19.3, -46.16) * mm});
            skLineSegment(sketch, "E948", {"start": v(-19.3, -46.16) * mm, "end": v(-20.13, -47.1) * mm});
            skLineSegment(sketch, "E949", {"start": v(-20.13, -47.1) * mm, "end": v(-21.25, -47.7) * mm});
            skLineSegment(sketch, "E950", {"start": v(-21.25, -47.7) * mm, "end": v(-22.53, -47.9) * mm});
            skLineSegment(sketch, "E951", {"start": v(-22.53, -47.9) * mm, "end": v(-23.72, -47.7) * mm});
            skLineSegment(sketch, "E952", {"start": v(-23.72, -47.7) * mm, "end": v(-24.66, -47.14) * mm});
            skLineSegment(sketch, "E953", {"start": v(-24.66, -47.14) * mm, "end": v(-25.26, -46.3) * mm});
            skLineSegment(sketch, "E954", {"start": v(-25.26, -46.3) * mm, "end": v(-25.46, -45.25) * mm});
            skLineSegment(sketch, "E955", {"start": v(-25.46, -45.25) * mm, "end": v(-25.21, -44.06) * mm});
            skLineSegment(sketch, "E956", {"start": v(-25.21, -44.06) * mm, "end": v(-24.49, -43.12) * mm});
            skLineSegment(sketch, "E957", {"start": v(-24.49, -43.12) * mm, "end": v(-23.36, -42.46) * mm});
            skLineSegment(sketch, "E958", {"start": v(-23.36, -42.46) * mm, "end": v(-22.02, -42.25) * mm});
            skLineSegment(sketch, "E959", {"start": v(-22.46, -43.52) * mm, "end": v(-22.85, -43.7) * mm});
            skLineSegment(sketch, "E960", {"start": v(-22.85, -43.7) * mm, "end": v(-23, -44.18) * mm});
            skLineSegment(sketch, "E961", {"start": v(-23, -44.18) * mm, "end": v(-22.88, -45.08) * mm});
            skLineSegment(sketch, "E962", {"start": v(-22.88, -45.08) * mm, "end": v(-22.58, -46.09) * mm});
            skLineSegment(sketch, "E963", {"start": v(-22.58, -46.09) * mm, "end": v(-22.02, -46.54) * mm});
            skLineSegment(sketch, "E964", {"start": v(-22.02, -46.54) * mm, "end": v(-21.65, -46.39) * mm});
            skLineSegment(sketch, "E965", {"start": v(-21.65, -46.39) * mm, "end": v(-21.53, -45.92) * mm});
            skLineSegment(sketch, "E966", {"start": v(-21.53, -45.92) * mm, "end": v(-21.66, -44.87) * mm});
            skLineSegment(sketch, "E967", {"start": v(-21.66, -44.87) * mm, "end": v(-21.96, -43.9) * mm});
            skLineSegment(sketch, "E968", {"start": v(-21.96, -43.9) * mm, "end": v(-22.46, -43.52) * mm});
            skLineSegment(sketch, "E969", {"start": v(-15.63, -40.55) * mm, "end": v(-15.7, -42.7) * mm});
            skLineSegment(sketch, "E970", {"start": v(-15.7, -42.7) * mm, "end": v(-15.7, -42.82) * mm});
            skLineSegment(sketch, "E971", {"start": v(-15.7, -42.82) * mm, "end": v(-15.63, -42.93) * mm});
            skLineSegment(sketch, "E972", {"start": v(-15.63, -42.93) * mm, "end": v(-15.41, -42.78) * mm});
            skLineSegment(sketch, "E973", {"start": v(-15.41, -42.78) * mm, "end": v(-14, -42.25) * mm});
            skLineSegment(sketch, "E974", {"start": v(-14, -42.25) * mm, "end": v(-12.63, -42.8) * mm});
            skLineSegment(sketch, "E975", {"start": v(-12.63, -42.8) * mm, "end": v(-12.08, -43.62) * mm});
            skLineSegment(sketch, "E976", {"start": v(-12.08, -43.62) * mm, "end": v(-11.9, -44.63) * mm});
            skLineSegment(sketch, "E977", {"start": v(-11.9, -44.63) * mm, "end": v(-12.2, -46.08) * mm});
            skLineSegment(sketch, "E978", {"start": v(-12.2, -46.08) * mm, "end": v(-13.09, -47.2) * mm});
            skLineSegment(sketch, "E979", {"start": v(-13.09, -47.2) * mm, "end": v(-15.1, -47.9) * mm});
            skLineSegment(sketch, "E980", {"start": v(-15.1, -47.9) * mm, "end": v(-16.14, -47.74) * mm});
            skLineSegment(sketch, "E981", {"start": v(-16.14, -47.74) * mm, "end": v(-17.14, -47.25) * mm});
            skLineSegment(sketch, "E982", {"start": v(-17.14, -47.25) * mm, "end": v(-17.28, -47.2) * mm});
            skLineSegment(sketch, "E983", {"start": v(-17.28, -47.2) * mm, "end": v(-17.62, -47.3) * mm});
            skLineSegment(sketch, "E984", {"start": v(-17.62, -47.3) * mm, "end": v(-17.95, -47.36) * mm});
            skLineSegment(sketch, "E985", {"start": v(-17.95, -47.36) * mm, "end": v(-18.3, -47.14) * mm});
            skLineSegment(sketch, "E986", {"start": v(-18.3, -47.14) * mm, "end": v(-18.27, -46.97) * mm});
            skLineSegment(sketch, "E987", {"start": v(-18.27, -46.97) * mm, "end": v(-18.12, -46.08) * mm});
            skLineSegment(sketch, "E988", {"start": v(-18.12, -46.08) * mm, "end": v(-18.08, -44.4) * mm});
            skLineSegment(sketch, "E989", {"start": v(-18.08, -44.4) * mm, "end": v(-18.08, -42.89) * mm});
            skLineSegment(sketch, "E990", {"start": v(-18.08, -42.89) * mm, "end": v(-18.13, -42.18) * mm});
            skLineSegment(sketch, "E991", {"start": v(-18.13, -42.18) * mm, "end": v(-18.37, -41.95) * mm});
            skLineSegment(sketch, "E992", {"start": v(-18.37, -41.95) * mm, "end": v(-18.77, -41.71) * mm});
            skLineSegment(sketch, "E993", {"start": v(-18.77, -41.71) * mm, "end": v(-18.88, -41.4) * mm});
            skLineSegment(sketch, "E994", {"start": v(-18.88, -41.4) * mm, "end": v(-18.1, -40.69) * mm});
            skLineSegment(sketch, "E995", {"start": v(-18.1, -40.69) * mm, "end": v(-17.02, -40.36) * mm});
            skLineSegment(sketch, "E996", {"start": v(-17.02, -40.36) * mm, "end": v(-15.92, -40.22) * mm});
            skLineSegment(sketch, "E997", {"start": v(-15.92, -40.22) * mm, "end": v(-15.63, -40.55) * mm});
            skLineSegment(sketch, "E998", {"start": v(-15.16, -43.91) * mm, "end": v(-15.59, -44.12) * mm});
            skLineSegment(sketch, "E999", {"start": v(-15.59, -44.12) * mm, "end": v(-15.7, -44.74) * mm});
            skLineSegment(sketch, "E1000", {"start": v(-15.7, -44.74) * mm, "end": v(-15.6, -46.5) * mm});
            skLineSegment(sketch, "E1001", {"start": v(-15.6, -46.5) * mm, "end": v(-15.14, -46.91) * mm});
            skLineSegment(sketch, "E1002", {"start": v(-15.14, -46.91) * mm, "end": v(-14.53, -46.57) * mm});
            skLineSegment(sketch, "E1003", {"start": v(-14.53, -46.57) * mm, "end": v(-14.32, -45.58) * mm});
            skLineSegment(sketch, "E1004", {"start": v(-14.32, -45.58) * mm, "end": v(-14.67, -44.18) * mm});
            skLineSegment(sketch, "E1005", {"start": v(-14.67, -44.18) * mm, "end": v(-15.16, -43.91) * mm});
            skLineSegment(sketch, "E1006", {"start": v(-8.91, -42.29) * mm, "end": v(-8.56, -42.37) * mm});
            skLineSegment(sketch, "E1007", {"start": v(-8.56, -42.37) * mm, "end": v(-8.45, -42.9) * mm});
            skLineSegment(sketch, "E1008", {"start": v(-8.45, -42.9) * mm, "end": v(-8.28, -43.14) * mm});
            skLineSegment(sketch, "E1009", {"start": v(-8.28, -43.14) * mm, "end": v(-8.07, -42.98) * mm});
            skLineSegment(sketch, "E1010", {"start": v(-8.07, -42.98) * mm, "end": v(-6.91, -42.3) * mm});
            skLineSegment(sketch, "E1011", {"start": v(-6.91, -42.3) * mm, "end": v(-6.1, -42.62) * mm});
            skLineSegment(sketch, "E1012", {"start": v(-6.1, -42.62) * mm, "end": v(-5.84, -43.03) * mm});
            skLineSegment(sketch, "E1013", {"start": v(-5.84, -43.03) * mm, "end": v(-5.74, -43.5) * mm});
            skLineSegment(sketch, "E1014", {"start": v(-5.74, -43.5) * mm, "end": v(-5.86, -44.04) * mm});
            skLineSegment(sketch, "E1015", {"start": v(-5.86, -44.04) * mm, "end": v(-6.17, -44.5) * mm});
            skLineSegment(sketch, "E1016", {"start": v(-6.17, -44.5) * mm, "end": v(-7.04, -44.83) * mm});
            skLineSegment(sketch, "E1017", {"start": v(-7.04, -44.83) * mm, "end": v(-7.51, -44.73) * mm});
            skLineSegment(sketch, "E1018", {"start": v(-7.51, -44.73) * mm, "end": v(-8.01, -44.33) * mm});
            skLineSegment(sketch, "E1019", {"start": v(-8.01, -44.33) * mm, "end": v(-8.23, -44.2) * mm});
            skLineSegment(sketch, "E1020", {"start": v(-8.23, -44.2) * mm, "end": v(-8.43, -44.39) * mm});
            skLineSegment(sketch, "E1021", {"start": v(-8.43, -44.39) * mm, "end": v(-8.47, -45.11) * mm});
            skLineSegment(sketch, "E1022", {"start": v(-8.47, -45.11) * mm, "end": v(-8.41, -46.25) * mm});
            skLineSegment(sketch, "E1023", {"start": v(-8.41, -46.25) * mm, "end": v(-8.3, -46.48) * mm});
            skLineSegment(sketch, "E1024", {"start": v(-8.3, -46.48) * mm, "end": v(-8.01, -46.6) * mm});
            skLineSegment(sketch, "E1025", {"start": v(-8.01, -46.6) * mm, "end": v(-7.51, -47.13) * mm});
            skLineSegment(sketch, "E1026", {"start": v(-7.51, -47.13) * mm, "end": v(-7.67, -47.52) * mm});
            skLineSegment(sketch, "E1027", {"start": v(-7.67, -47.52) * mm, "end": v(-8.1, -47.74) * mm});
            skLineSegment(sketch, "E1028", {"start": v(-8.1, -47.74) * mm, "end": v(-9.65, -47.85) * mm});
            skLineSegment(sketch, "E1029", {"start": v(-9.65, -47.85) * mm, "end": v(-11.14, -47.68) * mm});
            skLineSegment(sketch, "E1030", {"start": v(-11.14, -47.68) * mm, "end": v(-11.59, -47.15) * mm});
            skLineSegment(sketch, "E1031", {"start": v(-11.59, -47.15) * mm, "end": v(-11.26, -46.63) * mm});
            skLineSegment(sketch, "E1032", {"start": v(-11.26, -46.63) * mm, "end": v(-11.04, -46.45) * mm});
            skLineSegment(sketch, "E1033", {"start": v(-11.04, -46.45) * mm, "end": v(-10.95, -46.21) * mm});
            skLineSegment(sketch, "E1034", {"start": v(-10.95, -46.21) * mm, "end": v(-10.87, -44.35) * mm});
            skLineSegment(sketch, "E1035", {"start": v(-10.87, -44.35) * mm, "end": v(-10.92, -44) * mm});
            skLineSegment(sketch, "E1036", {"start": v(-10.92, -44) * mm, "end": v(-11.14, -43.82) * mm});
            skLineSegment(sketch, "E1037", {"start": v(-11.14, -43.82) * mm, "end": v(-11.53, -43.38) * mm});
            skLineSegment(sketch, "E1038", {"start": v(-11.53, -43.38) * mm, "end": v(-11.26, -42.93) * mm});
            skLineSegment(sketch, "E1039", {"start": v(-11.26, -42.93) * mm, "end": v(-10.36, -42.54) * mm});
            skLineSegment(sketch, "E1040", {"start": v(-10.36, -42.54) * mm, "end": v(-8.91, -42.29) * mm});
            skLineSegment(sketch, "E1041", {"start": v(-0.45, -45.27) * mm, "end": v(-3.04, -45.27) * mm});
            skLineSegment(sketch, "E1042", {"start": v(-3.04, -45.27) * mm, "end": v(-3.21, -45.42) * mm});
            skLineSegment(sketch, "E1043", {"start": v(-3.21, -45.42) * mm, "end": v(-2.83, -46.1) * mm});
            skLineSegment(sketch, "E1044", {"start": v(-2.83, -46.1) * mm, "end": v(-2, -46.41) * mm});
            skLineSegment(sketch, "E1045", {"start": v(-2, -46.41) * mm, "end": v(-1.4, -46.31) * mm});
            skLineSegment(sketch, "E1046", {"start": v(-1.4, -46.31) * mm, "end": v(-0.87, -46.06) * mm});
            skLineSegment(sketch, "E1047", {"start": v(-0.87, -46.06) * mm, "end": v(-0.57, -45.93) * mm});
            skLineSegment(sketch, "E1048", {"start": v(-0.57, -45.93) * mm, "end": v(-0.3, -46.1) * mm});
            skLineSegment(sketch, "E1049", {"start": v(-0.3, -46.1) * mm, "end": v(-0.16, -46.47) * mm});
            skLineSegment(sketch, "E1050", {"start": v(-0.16, -46.47) * mm, "end": v(-0.65, -47.24) * mm});
            skLineSegment(sketch, "E1051", {"start": v(-0.65, -47.24) * mm, "end": v(-2.67, -47.9) * mm});
            skLineSegment(sketch, "E1052", {"start": v(-2.67, -47.9) * mm, "end": v(-4.61, -47.22) * mm});
            skLineSegment(sketch, "E1053", {"start": v(-4.61, -47.22) * mm, "end": v(-5.24, -46.42) * mm});
            skLineSegment(sketch, "E1054", {"start": v(-5.24, -46.42) * mm, "end": v(-5.57, -45.1) * mm});
            skLineSegment(sketch, "E1055", {"start": v(-5.57, -45.1) * mm, "end": v(-5, -43.44) * mm});
            skLineSegment(sketch, "E1056", {"start": v(-5, -43.44) * mm, "end": v(-3.77, -42.49) * mm});
            skLineSegment(sketch, "E1057", {"start": v(-3.77, -42.49) * mm, "end": v(-2.55, -42.25) * mm});
            skLineSegment(sketch, "E1058", {"start": v(-2.55, -42.25) * mm, "end": v(-0.77, -42.85) * mm});
            skLineSegment(sketch, "E1059", {"start": v(-0.77, -42.85) * mm, "end": v(-0.18, -43.55) * mm});
            skLineSegment(sketch, "E1060", {"start": v(-0.18, -43.55) * mm, "end": v(0.08, -44.46) * mm});
            skLineSegment(sketch, "E1061", {"start": v(0.08, -44.46) * mm, "end": v(-0.07, -45.05) * mm});
            skLineSegment(sketch, "E1062", {"start": v(-0.07, -45.05) * mm, "end": v(-0.45, -45.27) * mm});
            skLineSegment(sketch, "E1063", {"start": v(-2.9, -44.24) * mm, "end": v(-2.34, -44.24) * mm});
            skLineSegment(sketch, "E1064", {"start": v(-2.34, -44.24) * mm, "end": v(-2, -43.92) * mm});
            skLineSegment(sketch, "E1065", {"start": v(-2, -43.92) * mm, "end": v(-2.16, -43.43) * mm});
            skLineSegment(sketch, "E1066", {"start": v(-2.16, -43.43) * mm, "end": v(-2.6, -43.24) * mm});
            skLineSegment(sketch, "E1067", {"start": v(-2.6, -43.24) * mm, "end": v(-3.1, -43.49) * mm});
            skLineSegment(sketch, "E1068", {"start": v(-3.1, -43.49) * mm, "end": v(-3.26, -43.94) * mm});
            skLineSegment(sketch, "E1069", {"start": v(-3.26, -43.94) * mm, "end": v(-3.18, -44.18) * mm});
            skLineSegment(sketch, "E1070", {"start": v(-3.18, -44.18) * mm, "end": v(-2.9, -44.24) * mm});
            skLineSegment(sketch, "E1071", {"start": v(7.42, -47.74) * mm, "end": v(3.67, -47.74) * mm});
            skLineSegment(sketch, "E1072", {"start": v(3.67, -47.74) * mm, "end": v(3.17, -47.46) * mm});
            skLineSegment(sketch, "E1073", {"start": v(3.17, -47.46) * mm, "end": v(3.28, -47.2) * mm});
            skLineSegment(sketch, "E1074", {"start": v(3.28, -47.2) * mm, "end": v(3.96, -46.53) * mm});
            skLineSegment(sketch, "E1075", {"start": v(3.96, -46.53) * mm, "end": v(5.53, -44.66) * mm});
            skLineSegment(sketch, "E1076", {"start": v(5.53, -44.66) * mm, "end": v(5.8, -43.9) * mm});
            skLineSegment(sketch, "E1077", {"start": v(5.8, -43.9) * mm, "end": v(5.64, -43.47) * mm});
            skLineSegment(sketch, "E1078", {"start": v(5.64, -43.47) * mm, "end": v(5.2, -43.3) * mm});
            skLineSegment(sketch, "E1079", {"start": v(5.2, -43.3) * mm, "end": v(4.82, -43.37) * mm});
            skLineSegment(sketch, "E1080", {"start": v(4.82, -43.37) * mm, "end": v(4.24, -43.82) * mm});
            skLineSegment(sketch, "E1081", {"start": v(4.24, -43.82) * mm, "end": v(3.92, -43.92) * mm});
            skLineSegment(sketch, "E1082", {"start": v(3.92, -43.92) * mm, "end": v(3.44, -43.72) * mm});
            skLineSegment(sketch, "E1083", {"start": v(3.44, -43.72) * mm, "end": v(3.22, -43.28) * mm});
            skLineSegment(sketch, "E1084", {"start": v(3.22, -43.28) * mm, "end": v(3.42, -42.8) * mm});
            skLineSegment(sketch, "E1085", {"start": v(3.42, -42.8) * mm, "end": v(3.95, -42.27) * mm});
            skLineSegment(sketch, "E1086", {"start": v(3.95, -42.27) * mm, "end": v(5.2, -41.63) * mm});
            skLineSegment(sketch, "E1087", {"start": v(5.2, -41.63) * mm, "end": v(6.59, -41.42) * mm});
            skLineSegment(sketch, "E1088", {"start": v(6.59, -41.42) * mm, "end": v(8.41, -41.84) * mm});
            skLineSegment(sketch, "E1089", {"start": v(8.41, -41.84) * mm, "end": v(8.93, -42.38) * mm});
            skLineSegment(sketch, "E1090", {"start": v(8.93, -42.38) * mm, "end": v(9.13, -43.11) * mm});
            skLineSegment(sketch, "E1091", {"start": v(9.13, -43.11) * mm, "end": v(8.8, -44.12) * mm});
            skLineSegment(sketch, "E1092", {"start": v(8.8, -44.12) * mm, "end": v(7.8, -45.2) * mm});
            skLineSegment(sketch, "E1093", {"start": v(7.8, -45.2) * mm, "end": v(7.32, -45.8) * mm});
            skLineSegment(sketch, "E1094", {"start": v(7.32, -45.8) * mm, "end": v(7.47, -46.07) * mm});
            skLineSegment(sketch, "E1095", {"start": v(7.47, -46.07) * mm, "end": v(7.81, -46.17) * mm});
            skLineSegment(sketch, "E1096", {"start": v(7.81, -46.17) * mm, "end": v(8.68, -45.8) * mm});
            skLineSegment(sketch, "E1097", {"start": v(8.68, -45.8) * mm, "end": v(8.93, -45.57) * mm});
            skLineSegment(sketch, "E1098", {"start": v(8.93, -45.57) * mm, "end": v(9.11, -45.53) * mm});
            skLineSegment(sketch, "E1099", {"start": v(9.11, -45.53) * mm, "end": v(9.47, -45.74) * mm});
            skLineSegment(sketch, "E1100", {"start": v(9.47, -45.74) * mm, "end": v(9.6, -46.36) * mm});
            skLineSegment(sketch, "E1101", {"start": v(9.6, -46.36) * mm, "end": v(9.44, -47.2) * mm});
            skLineSegment(sketch, "E1102", {"start": v(9.44, -47.2) * mm, "end": v(9.01, -47.93) * mm});
            skLineSegment(sketch, "E1103", {"start": v(9.01, -47.93) * mm, "end": v(8.38, -48.26) * mm});
            skLineSegment(sketch, "E1104", {"start": v(8.38, -48.26) * mm, "end": v(8.16, -48.2) * mm});
            skLineSegment(sketch, "E1105", {"start": v(8.16, -48.2) * mm, "end": v(7.97, -47.99) * mm});
            skLineSegment(sketch, "E1106", {"start": v(7.97, -47.99) * mm, "end": v(7.78, -47.79) * mm});
            skLineSegment(sketch, "E1107", {"start": v(7.78, -47.79) * mm, "end": v(7.42, -47.74) * mm});
            skLineSegment(sketch, "E1108", {"start": v(13.11, -41.38) * mm, "end": v(14.57, -41.75) * mm});
            skLineSegment(sketch, "E1109", {"start": v(14.57, -41.75) * mm, "end": v(15.98, -43.23) * mm});
            skLineSegment(sketch, "E1110", {"start": v(15.98, -43.23) * mm, "end": v(16.33, -44.76) * mm});
            skLineSegment(sketch, "E1111", {"start": v(16.33, -44.76) * mm, "end": v(16.05, -46.1) * mm});
            skLineSegment(sketch, "E1112", {"start": v(16.05, -46.1) * mm, "end": v(15.2, -47.17) * mm});
            skLineSegment(sketch, "E1113", {"start": v(15.2, -47.17) * mm, "end": v(13.23, -47.9) * mm});
            skLineSegment(sketch, "E1114", {"start": v(13.23, -47.9) * mm, "end": v(12.1, -47.7) * mm});
            skLineSegment(sketch, "E1115", {"start": v(12.1, -47.7) * mm, "end": v(11.14, -47.1) * mm});
            skLineSegment(sketch, "E1116", {"start": v(11.14, -47.1) * mm, "end": v(10.38, -46) * mm});
            skLineSegment(sketch, "E1117", {"start": v(10.38, -46) * mm, "end": v(10.12, -44.57) * mm});
            skLineSegment(sketch, "E1118", {"start": v(10.12, -44.57) * mm, "end": v(10.36, -43.2) * mm});
            skLineSegment(sketch, "E1119", {"start": v(10.36, -43.2) * mm, "end": v(11.06, -42.16) * mm});
            skLineSegment(sketch, "E1120", {"start": v(11.06, -42.16) * mm, "end": v(11.98, -41.58) * mm});
            skLineSegment(sketch, "E1121", {"start": v(11.98, -41.58) * mm, "end": v(13.11, -41.38) * mm});
            skLineSegment(sketch, "E1122", {"start": v(12.99, -43.02) * mm, "end": v(12.6, -43.24) * mm});
            skLineSegment(sketch, "E1123", {"start": v(12.6, -43.24) * mm, "end": v(12.47, -43.9) * mm});
            skLineSegment(sketch, "E1124", {"start": v(12.47, -43.9) * mm, "end": v(12.9, -45.95) * mm});
            skLineSegment(sketch, "E1125", {"start": v(12.9, -45.95) * mm, "end": v(13.37, -46.3) * mm});
            skLineSegment(sketch, "E1126", {"start": v(13.37, -46.3) * mm, "end": v(13.74, -46.08) * mm});
            skLineSegment(sketch, "E1127", {"start": v(13.74, -46.08) * mm, "end": v(13.87, -45.41) * mm});
            skLineSegment(sketch, "E1128", {"start": v(13.87, -45.41) * mm, "end": v(13.76, -44.35) * mm});
            skLineSegment(sketch, "E1129", {"start": v(13.76, -44.35) * mm, "end": v(13.49, -43.43) * mm});
            skLineSegment(sketch, "E1130", {"start": v(13.49, -43.43) * mm, "end": v(12.99, -43.02) * mm});
            skLineSegment(sketch, "E1131", {"start": v(17.18, -46.67) * mm, "end": v(17.54, -46.7) * mm});
            skLineSegment(sketch, "E1132", {"start": v(17.54, -46.7) * mm, "end": v(17.75, -46.73) * mm});
            skLineSegment(sketch, "E1133", {"start": v(17.75, -46.73) * mm, "end": v(18.3, -45.99) * mm});
            skLineSegment(sketch, "E1134", {"start": v(18.3, -45.99) * mm, "end": v(18.33, -43.6) * mm});
            skLineSegment(sketch, "E1135", {"start": v(18.33, -43.6) * mm, "end": v(18.21, -43.2) * mm});
            skLineSegment(sketch, "E1136", {"start": v(18.21, -43.2) * mm, "end": v(17.77, -43.08) * mm});
            skLineSegment(sketch, "E1137", {"start": v(17.77, -43.08) * mm, "end": v(17.55, -43.1) * mm});
            skLineSegment(sketch, "E1138", {"start": v(17.55, -43.1) * mm, "end": v(17.36, -43.1) * mm});
            skLineSegment(sketch, "E1139", {"start": v(17.36, -43.1) * mm, "end": v(17.05, -43) * mm});
            skLineSegment(sketch, "E1140", {"start": v(17.05, -43) * mm, "end": v(16.94, -42.74) * mm});
            skLineSegment(sketch, "E1141", {"start": v(16.94, -42.74) * mm, "end": v(17.11, -42.4) * mm});
            skLineSegment(sketch, "E1142", {"start": v(17.11, -42.4) * mm, "end": v(17.6, -42.08) * mm});
            skLineSegment(sketch, "E1143", {"start": v(17.6, -42.08) * mm, "end": v(20.92, -41.42) * mm});
            skLineSegment(sketch, "E1144", {"start": v(20.92, -41.42) * mm, "end": v(21.62, -41.54) * mm});
            skLineSegment(sketch, "E1145", {"start": v(21.62, -41.54) * mm, "end": v(21.84, -41.9) * mm});
            skLineSegment(sketch, "E1146", {"start": v(21.84, -41.9) * mm, "end": v(21.77, -42.12) * mm});
            skLineSegment(sketch, "E1147", {"start": v(21.77, -42.12) * mm, "end": v(21.48, -42.3) * mm});
            skLineSegment(sketch, "E1148", {"start": v(21.48, -42.3) * mm, "end": v(21.09, -42.65) * mm});
            skLineSegment(sketch, "E1149", {"start": v(21.09, -42.65) * mm, "end": v(21.01, -44.33) * mm});
            skLineSegment(sketch, "E1150", {"start": v(21.01, -44.33) * mm, "end": v(21.06, -45.91) * mm});
            skLineSegment(sketch, "E1151", {"start": v(21.06, -45.91) * mm, "end": v(21.1, -46.2) * mm});
            skLineSegment(sketch, "E1152", {"start": v(21.1, -46.2) * mm, "end": v(21.35, -46.6) * mm});
            skLineSegment(sketch, "E1153", {"start": v(21.35, -46.6) * mm, "end": v(22, -46.74) * mm});
            skLineSegment(sketch, "E1154", {"start": v(22, -46.74) * mm, "end": v(22.51, -47.16) * mm});
            skLineSegment(sketch, "E1155", {"start": v(22.51, -47.16) * mm, "end": v(21.78, -47.72) * mm});
            skLineSegment(sketch, "E1156", {"start": v(21.78, -47.72) * mm, "end": v(19.68, -47.9) * mm});
            skLineSegment(sketch, "E1157", {"start": v(19.68, -47.9) * mm, "end": v(18.35, -47.81) * mm});
            skLineSegment(sketch, "E1158", {"start": v(18.35, -47.81) * mm, "end": v(17.12, -47.54) * mm});
            skLineSegment(sketch, "E1159", {"start": v(17.12, -47.54) * mm, "end": v(16.7, -47.08) * mm});
            skLineSegment(sketch, "E1160", {"start": v(16.7, -47.08) * mm, "end": v(16.84, -46.8) * mm});
            skLineSegment(sketch, "E1161", {"start": v(16.84, -46.8) * mm, "end": v(17.18, -46.67) * mm});
            skLineSegment(sketch, "E1162", {"start": v(25.42, -40.57) * mm, "end": v(26.2, -40.74) * mm});
            skLineSegment(sketch, "E1163", {"start": v(26.2, -40.74) * mm, "end": v(26.68, -40.97) * mm});
            skLineSegment(sketch, "E1164", {"start": v(26.68, -40.97) * mm, "end": v(26.88, -41.2) * mm});
            skLineSegment(sketch, "E1165", {"start": v(26.88, -41.2) * mm, "end": v(26.82, -41.38) * mm});
            skLineSegment(sketch, "E1166", {"start": v(26.82, -41.38) * mm, "end": v(26.41, -41.84) * mm});
            skLineSegment(sketch, "E1167", {"start": v(26.41, -41.84) * mm, "end": v(26.02, -42.42) * mm});
            skLineSegment(sketch, "E1168", {"start": v(26.02, -42.42) * mm, "end": v(25.85, -42.93) * mm});
            skLineSegment(sketch, "E1169", {"start": v(25.85, -42.93) * mm, "end": v(25.9, -43.07) * mm});
            skLineSegment(sketch, "E1170", {"start": v(25.9, -43.07) * mm, "end": v(26.02, -43.12) * mm});
            skLineSegment(sketch, "E1171", {"start": v(26.02, -43.12) * mm, "end": v(26.41, -43) * mm});
            skLineSegment(sketch, "E1172", {"start": v(26.41, -43) * mm, "end": v(27.27, -42.84) * mm});
            skLineSegment(sketch, "E1173", {"start": v(27.27, -42.84) * mm, "end": v(28.54, -43.28) * mm});
            skLineSegment(sketch, "E1174", {"start": v(28.54, -43.28) * mm, "end": v(29.13, -44) * mm});
            skLineSegment(sketch, "E1175", {"start": v(29.13, -44) * mm, "end": v(29.33, -44.93) * mm});
            skLineSegment(sketch, "E1176", {"start": v(29.33, -44.93) * mm, "end": v(28.85, -46.5) * mm});
            skLineSegment(sketch, "E1177", {"start": v(28.85, -46.5) * mm, "end": v(27.75, -47.55) * mm});
            skLineSegment(sketch, "E1178", {"start": v(27.75, -47.55) * mm, "end": v(26.2, -47.9) * mm});
            skLineSegment(sketch, "E1179", {"start": v(26.2, -47.9) * mm, "end": v(24.9, -47.68) * mm});
            skLineSegment(sketch, "E1180", {"start": v(24.9, -47.68) * mm, "end": v(23.86, -47.05) * mm});
            skLineSegment(sketch, "E1181", {"start": v(23.86, -47.05) * mm, "end": v(23.1, -45.87) * mm});
            skLineSegment(sketch, "E1182", {"start": v(23.1, -45.87) * mm, "end": v(22.87, -44.69) * mm});
            skLineSegment(sketch, "E1183", {"start": v(22.87, -44.69) * mm, "end": v(23.15, -43.28) * mm});
            skLineSegment(sketch, "E1184", {"start": v(23.15, -43.28) * mm, "end": v(23.99, -41.83) * mm});
            skLineSegment(sketch, "E1185", {"start": v(23.99, -41.83) * mm, "end": v(24.84, -40.86) * mm});
            skLineSegment(sketch, "E1186", {"start": v(24.84, -40.86) * mm, "end": v(25.42, -40.57) * mm});
            skLineSegment(sketch, "E1187", {"start": v(26.02, -44.4) * mm, "end": v(25.63, -44.57) * mm});
            skLineSegment(sketch, "E1188", {"start": v(25.63, -44.57) * mm, "end": v(25.5, -45.04) * mm});
            skLineSegment(sketch, "E1189", {"start": v(25.5, -45.04) * mm, "end": v(25.82, -45.95) * mm});
            skLineSegment(sketch, "E1190", {"start": v(25.82, -45.95) * mm, "end": v(26.48, -46.4) * mm});
            skLineSegment(sketch, "E1191", {"start": v(26.48, -46.4) * mm, "end": v(26.84, -46.27) * mm});
            skLineSegment(sketch, "E1192", {"start": v(26.84, -46.27) * mm, "end": v(26.98, -45.9) * mm});
            skLineSegment(sketch, "E1193", {"start": v(26.98, -45.9) * mm, "end": v(26.82, -45.14) * mm});
            skLineSegment(sketch, "E1194", {"start": v(26.82, -45.14) * mm, "end": v(26.41, -44.55) * mm});
            skLineSegment(sketch, "E1195", {"start": v(26.41, -44.55) * mm, "end": v(26.02, -44.4) * mm});
            skSolve(sketch);
        }
        {
            var Q0;
            Q0=makeQuery(id+"F10.imprint","IMPRINT",FACE,{"disambiguationData":[TD([[makeQuery(id+"F10.imprint","IMPRINT",EDGE,{"derivedFrom":sQuery(id+"F10.wireOp",EDGE,"E845")}),-1.0]])]});
            var Q1;
            Q1=makeQuery(id+"F10.imprint","IMPRINT",FACE,{"disambiguationData":[TD([[makeQuery(id+"F10.imprint","IMPRINT",EDGE,{"derivedFrom":sQuery(id+"F10.wireOp",EDGE,"E872")}),-1.0]])]});
            var Q2;
            Q2=makeQuery(id+"F10.imprint","IMPRINT",FACE,{"disambiguationData":[TD([[makeQuery(id+"F10.imprint","IMPRINT",EDGE,{"derivedFrom":sQuery(id+"F10.wireOp",EDGE,"E908")}),-1.0]])]});
            var Q3;
            Q3=makeQuery(id+"F10.imprint","IMPRINT",FACE,{"disambiguationData":[TD([[makeQuery(id+"F10.imprint","IMPRINT",EDGE,{"derivedFrom":sQuery(id+"F10.wireOp",EDGE,"E944")}),-1.0]])]});
            var Q4;
            Q4=makeQuery(id+"F10.imprint","IMPRINT",FACE,{"disambiguationData":[TD([[makeQuery(id+"F10.imprint","IMPRINT",EDGE,{"derivedFrom":sQuery(id+"F10.wireOp",EDGE,"E969")}),-1.0]])]});
            var Q5;
            Q5=makeQuery(id+"F10.imprint","IMPRINT",FACE,{"disambiguationData":[TD([[makeQuery(id+"F10.imprint","IMPRINT",EDGE,{"derivedFrom":sQuery(id+"F10.wireOp",EDGE,"E1006")}),-1.0]])]});
            var Q6;
            Q6=makeQuery(id+"F10.imprint","IMPRINT",FACE,{"disambiguationData":[TD([[makeQuery(id+"F10.imprint","IMPRINT",EDGE,{"derivedFrom":sQuery(id+"F10.wireOp",EDGE,"E1041")}),-1.0]])]});
            var Q7;
            Q7=makeQuery(id+"F10.imprint","IMPRINT",FACE,{"disambiguationData":[TD([[makeQuery(id+"F10.imprint","IMPRINT",EDGE,{"derivedFrom":sQuery(id+"F10.wireOp",EDGE,"E1071")}),-1.0]])]});
            var Q8;
            Q8=makeQuery(id+"F10.imprint","IMPRINT",FACE,{"disambiguationData":[TD([[makeQuery(id+"F10.imprint","IMPRINT",EDGE,{"derivedFrom":sQuery(id+"F10.wireOp",EDGE,"E1108")}),-1.0]])]});
            var Q9;
            Q9=makeQuery(id+"F10.imprint","IMPRINT",FACE,{"disambiguationData":[TD([[makeQuery(id+"F10.imprint","IMPRINT",EDGE,{"derivedFrom":sQuery(id+"F10.wireOp",EDGE,"E1131")}),-1.0]])]});
            var Q10;
            Q10=makeQuery(id+"F10.imprint","IMPRINT",FACE,{"disambiguationData":[TD([[makeQuery(id+"F10.imprint","IMPRINT",EDGE,{"derivedFrom":sQuery(id+"F10.wireOp",EDGE,"E1162")}),-1.0]])]});
            var Q11;
            Q11=makeQuery(id+"F10.imprint","IMPRINT",FACE,{"disambiguationData":[TD([[makeQuery(id+"F10.imprint","IMPRINT",EDGE,{"derivedFrom":sQuery(id+"F10.wireOp",EDGE,"E807")}),1.0]])]});
            extrude(context, id + "F11", {"entities" : qUnion([Q0, Q1, Q2, Q3, Q4, Q5, Q6, Q7, Q8, Q9, Q10, Q11]), "operationType" : NewBodyOperationType.REMOVE, "oppositeDirection" : true, "depth" : 1 * mm});
        }
        {
            var Q0;
            Q0=makeQuery(id+"F10.imprint","IMPRINT",FACE,{"disambiguationData":[TD([[makeQuery(id+"F10.imprint","IMPRINT",EDGE,{"derivedFrom":sQuery(id+"F10.wireOp",EDGE,"E437")}),1.0]])]});
            var Q1;
            {var subQ0=sQuery(id+"F10.wireOp",EDGE,"E490");Q1=makeQuery(id+"F10.imprint","IMPRINT",FACE,{"disambiguationData":[TD([[makeQuery(id+"F10.imprint","IMPRINT",EDGE,{"derivedFrom":subQ0}),1.0]])]});}
            var Q2;
            Q2=makeQuery(id+"F10.imprint","IMPRINT",FACE,{"disambiguationData":[TD([[makeQuery(id+"F10.imprint","IMPRINT",EDGE,{"derivedFrom":sQuery(id+"F10.wireOp",EDGE,"E419")}),1.0]])]});
            var Q3;
            {var subQ4=sQuery(id+"F10.wireOp",EDGE,"E476");Q3=makeQuery(id+"F10.imprint","IMPRINT",FACE,{"disambiguationData":[TD([[makeQuery(id+"F10.imprint","IMPRINT",EDGE,{"derivedFrom":subQ4}),1.0]])]});}
            var Q4;
            {var subQ0=sQuery(id+"F10.wireOp",EDGE,"E508");Q4=makeQuery(id+"F10.imprint","IMPRINT",FACE,{"disambiguationData":[TD([[makeQuery(id+"F10.imprint","IMPRINT",EDGE,{"derivedFrom":subQ0}),1.0]])]});}
            var Q5;
            Q5=makeQuery(id+"F10.imprint","IMPRINT",FACE,{"disambiguationData":[TD([[makeQuery(id+"F10.imprint","IMPRINT",EDGE,{"derivedFrom":sQuery(id+"F10.wireOp",EDGE,"E455")}),1.0]])]});
            var Q6;
            {var subQ0=sQuery(id+"F10.wireOp",EDGE,"E342");Q6=makeQuery(id+"F10.imprint","IMPRINT",FACE,{"disambiguationData":[TD([[makeQuery(id+"F10.imprint","IMPRINT",EDGE,{"derivedFrom":subQ0}),1.0]])]});}
            var Q7;
            Q7=makeQuery(id+"F10.imprint","IMPRINT",FACE,{"disambiguationData":[TD([[makeQuery(id+"F10.imprint","IMPRINT",EDGE,{"derivedFrom":sQuery(id+"F10.wireOp",EDGE,"E288")}),1.0]])]});
            var Q8;
            Q8=makeQuery(id+"F10.imprint","IMPRINT",FACE,{"disambiguationData":[TD([[makeQuery(id+"F10.imprint","IMPRINT",EDGE,{"derivedFrom":sQuery(id+"F10.wireOp",EDGE,"E253")}),1.0]])]});
            var Q9;
            Q9=makeQuery(id+"F10.imprint","IMPRINT",FACE,{"disambiguationData":[TD([[makeQuery(id+"F10.imprint","IMPRINT",EDGE,{"derivedFrom":sQuery(id+"F10.wireOp",EDGE,"E271")}),1.0]])]});
            var Q10;
            {var subQ6=sQuery(id+"F10.wireOp",EDGE,"E274");Q10=makeQuery(id+"F10.imprint","IMPRINT",FACE,{"disambiguationData":[TD([[makeQuery(id+"F10.imprint","IMPRINT",EDGE,{"derivedFrom":subQ6}),1.0]])]});}
            var Q11;
            Q11=makeQuery(id+"F10.imprint","IMPRINT",FACE,{"disambiguationData":[TD([[makeQuery(id+"F10.imprint","IMPRINT",EDGE,{"derivedFrom":sQuery(id+"F10.wireOp",EDGE,"E321")}),1.0]])]});
            var Q12;
            Q12=makeQuery(id+"F10.imprint","IMPRINT",FACE,{"disambiguationData":[TD([[makeQuery(id+"F10.imprint","IMPRINT",EDGE,{"derivedFrom":sQuery(id+"F10.wireOp",EDGE,"E307")}),1.0]])]});
            var Q13;
            {var subQ0=sQuery(id+"F10.wireOp",EDGE,"E163");Q13=makeQuery(id+"F10.imprint","IMPRINT",FACE,{"disambiguationData":[TD([[makeQuery(id+"F10.imprint","IMPRINT",EDGE,{"derivedFrom":subQ0}),1.0]])]});}
            var Q14;
            {var subQ5=sQuery(id+"F10.wireOp",EDGE,"E429");Q14=makeQuery(id+"F10.imprint","IMPRINT",FACE,{"disambiguationData":[TD([[makeQuery(id+"F10.imprint","IMPRINT",EDGE,{"derivedFrom":subQ5}),1.0]])]});}
            var Q15;
            Q15=makeQuery(id+"F10.imprint","IMPRINT",FACE,{"disambiguationData":[TD([[makeQuery(id+"F10.imprint","IMPRINT",EDGE,{"derivedFrom":sQuery(id+"F10.wireOp",EDGE,"E153")}),1.0]])]});
            var Q16;
            Q16=makeQuery(id+"F10.imprint","IMPRINT",FACE,{"disambiguationData":[TD([[makeQuery(id+"F10.imprint","IMPRINT",EDGE,{"derivedFrom":sQuery(id+"F10.wireOp",EDGE,"E171")}),1.0]])]});
            var Q17;
            Q17=makeQuery(id+"F10.imprint","IMPRINT",FACE,{"disambiguationData":[TD([[makeQuery(id+"F10.imprint","IMPRINT",EDGE,{"derivedFrom":sQuery(id+"F10.wireOp",EDGE,"E132")}),1.0]])]});
            var Q18;
            {var subQ0=sQuery(id+"F10.wireOp",EDGE,"E143");Q18=makeQuery(id+"F10.imprint","IMPRINT",FACE,{"disambiguationData":[TD([[makeQuery(id+"F10.imprint","IMPRINT",EDGE,{"derivedFrom":subQ0}),1.0]])]});}
            var Q19;
            {var subQ0=sQuery(id+"F10.wireOp",EDGE,"E86");Q19=makeQuery(id+"F10.imprint","IMPRINT",FACE,{"disambiguationData":[TD([[makeQuery(id+"F10.imprint","IMPRINT",EDGE,{"derivedFrom":subQ0}),1.0]])]});}
            var Q20;
            {var subQ0=sQuery(id+"F10.wireOp",EDGE,"E92");Q20=makeQuery(id+"F10.imprint","IMPRINT",FACE,{"disambiguationData":[TD([[makeQuery(id+"F10.imprint","IMPRINT",EDGE,{"derivedFrom":subQ0}),1.0]])]});}
            var Q21;
            Q21=makeQuery(id+"F10.imprint","IMPRINT",FACE,{"disambiguationData":[TD([[makeQuery(id+"F10.imprint","IMPRINT",EDGE,{"derivedFrom":sQuery(id+"F10.wireOp",EDGE,"E104")}),1.0]])]});
            var Q22;
            Q22=makeQuery(id+"F10.imprint","IMPRINT",FACE,{"disambiguationData":[TD([[makeQuery(id+"F10.imprint","IMPRINT",EDGE,{"derivedFrom":sQuery(id+"F10.wireOp",EDGE,"E120")}),1.0]])]});
            var Q23;
            Q23=makeQuery(id+"F10.imprint","IMPRINT",FACE,{"disambiguationData":[TD([[makeQuery(id+"F10.imprint","IMPRINT",EDGE,{"derivedFrom":sQuery(id+"F10.wireOp",EDGE,"E338")}),1.0]])]});
            var Q24;
            {var subQ0=sQuery(id+"F10.wireOp",EDGE,"E259");Q24=makeQuery(id+"F10.imprint","IMPRINT",FACE,{"disambiguationData":[TD([[makeQuery(id+"F10.imprint","IMPRINT",EDGE,{"derivedFrom":subQ0}),1.0]])]});}
            var Q25;
            Q25=makeQuery(id+"F10.imprint","IMPRINT",FACE,{"disambiguationData":[TD([[makeQuery(id+"F10.imprint","IMPRINT",EDGE,{"derivedFrom":sQuery(id+"F10.wireOp",EDGE,"E487")}),1.0]])]});
            var Q26;
            Q26=makeQuery(id+"F10.imprint","IMPRINT",FACE,{"disambiguationData":[TD([[makeQuery(id+"F10.imprint","IMPRINT",EDGE,{"derivedFrom":sQuery(id+"F10.wireOp",EDGE,"E503")}),1.0]])]});
            var Q27;
            {var subQ0=sQuery(id+"F10.wireOp",EDGE,"E470");Q27=makeQuery(id+"F10.imprint","IMPRINT",FACE,{"disambiguationData":[TD([[makeQuery(id+"F10.imprint","IMPRINT",EDGE,{"derivedFrom":subQ0}),1.0]])]});}
            var Q28;
            {var subQ10=sQuery(id+"F10.wireOp",EDGE,"E542");Q28=makeQuery(id+"F10.imprint","IMPRINT",FACE,{"disambiguationData":[TD([[makeQuery(id+"F10.imprint","IMPRINT",EDGE,{"derivedFrom":subQ10}),-1.0]])]});}
            var Q29;
            {var subQ10=sQuery(id+"F10.wireOp",EDGE,"E540");Q29=makeQuery(id+"F10.imprint","IMPRINT",FACE,{"disambiguationData":[TD([[makeQuery(id+"F10.imprint","IMPRINT",EDGE,{"derivedFrom":subQ10}),-1.0]])]});}
            var Q30;
            Q30=makeQuery(id+"F10.imprint","IMPRINT",FACE,{"disambiguationData":[TD([[makeQuery(id+"F10.imprint","IMPRINT",EDGE,{"derivedFrom":sQuery(id+"F10.wireOp",EDGE,"E599")}),-1.0]])]});
            var Q31;
            Q31=makeQuery(id+"F10.imprint","IMPRINT",FACE,{"disambiguationData":[TD([[makeQuery(id+"F10.imprint","IMPRINT",EDGE,{"derivedFrom":sQuery(id+"F10.wireOp",EDGE,"E580")}),-1.0]])]});
            var Q32;
            Q32=makeQuery(id+"F10.imprint","IMPRINT",FACE,{"disambiguationData":[TD([[makeQuery(id+"F10.imprint","IMPRINT",EDGE,{"derivedFrom":sQuery(id+"F10.wireOp",EDGE,"E589")}),-1.0]])]});
            var Q33;
            Q33=makeQuery(id+"F10.imprint","IMPRINT",FACE,{"disambiguationData":[TD([[makeQuery(id+"F10.imprint","IMPRINT",EDGE,{"derivedFrom":sQuery(id+"F10.wireOp",EDGE,"E611")}),-1.0]])]});
            var Q34;
            {var subQ0=sQuery(id+"F10.wireOp",EDGE,"E539");var subQ1=sQuery(id+"F10.wireOp",EDGE,"E538");var subQ2=makeQuery(id+"F10.imprint","INTERSECT",VERTEX,{"derivedFrom":[subQ1,subQ0]});Q34=makeQuery(id+"F10.imprint","IMPRINT",FACE,{"disambiguationData":[TD([[makeQuery(id+"F10.imprint","IMPRINT",EDGE,{"disambiguationData":[TD([[subQ2,1.0]])],"derivedFrom":subQ1}),1.0]])]});}
            var Q35;
            Q35=makeQuery(id+"F10.imprint","IMPRINT",FACE,{"disambiguationData":[TD([[makeQuery(id+"F10.imprint","IMPRINT",EDGE,{"derivedFrom":sQuery(id+"F10.wireOp",EDGE,"E521")}),-1.0]])]});
            var Q36;
            {var subQ0=sQuery(id+"F10.wireOp",EDGE,"E639");Q36=makeQuery(id+"F10.imprint","IMPRINT",FACE,{"disambiguationData":[TD([[makeQuery(id+"F10.imprint","IMPRINT",EDGE,{"derivedFrom":subQ0}),1.0]])]});}
            var Q37;
            {var subQ4=sQuery(id+"F10.wireOp",EDGE,"E536");Q37=makeQuery(id+"F10.imprint","IMPRINT",FACE,{"disambiguationData":[TD([[makeQuery(id+"F10.imprint","IMPRINT",EDGE,{"derivedFrom":subQ4}),-1.0]])]});}
            var Q38;
            Q38=makeQuery(id+"F10.imprint","IMPRINT",FACE,{"disambiguationData":[TD([[makeQuery(id+"F10.imprint","IMPRINT",EDGE,{"derivedFrom":sQuery(id+"F10.wireOp",EDGE,"E557")}),-1.0]])]});
            var Q39;
            {var subQ0=sQuery(id+"F10.wireOp",EDGE,"E623");Q39=makeQuery(id+"F10.imprint","IMPRINT",FACE,{"disambiguationData":[TD([[makeQuery(id+"F10.imprint","IMPRINT",EDGE,{"derivedFrom":subQ0}),1.0]])]});}
            var Q40;
            {var subQ0=sQuery(id+"F10.wireOp",EDGE,"E656");Q40=makeQuery(id+"F10.imprint","IMPRINT",FACE,{"disambiguationData":[TD([[makeQuery(id+"F10.imprint","IMPRINT",EDGE,{"derivedFrom":subQ0}),1.0]])]});}
            var Q41;
            Q41=makeQuery(id+"F10.imprint","IMPRINT",FACE,{"disambiguationData":[TD([[makeQuery(id+"F10.imprint","IMPRINT",EDGE,{"derivedFrom":sQuery(id+"F10.wireOp",EDGE,"E629")}),1.0]])]});
            var Q42;
            {var subQ0=sQuery(id+"F10.wireOp",EDGE,"E648");Q42=makeQuery(id+"F10.imprint","IMPRINT",FACE,{"disambiguationData":[TD([[makeQuery(id+"F10.imprint","IMPRINT",EDGE,{"derivedFrom":subQ0}),1.0]])]});}
            var Q43;
            {var subQ0=sQuery(id+"F10.wireOp",EDGE,"E637");Q43=makeQuery(id+"F10.imprint","IMPRINT",FACE,{"disambiguationData":[TD([[makeQuery(id+"F10.imprint","IMPRINT",EDGE,{"derivedFrom":subQ0}),1.0]])]});}
            var Q44;
            {var subQ0=sQuery(id+"F10.wireOp",EDGE,"E654");var subQ1=sQuery(id+"F10.wireOp",EDGE,"E572");var subQ2=makeQuery(id+"F10.imprint","INTERSECT",VERTEX,{"derivedFrom":[subQ1,subQ0]});Q44=makeQuery(id+"F10.imprint","IMPRINT",FACE,{"disambiguationData":[TD([[makeQuery(id+"F10.imprint","IMPRINT",EDGE,{"disambiguationData":[TD([[subQ2,-1.0]])],"derivedFrom":subQ1}),-1.0]])]});}
            var Q45;
            {var subQ0=sQuery(id+"F10.wireOp",EDGE,"E621");Q45=makeQuery(id+"F10.imprint","IMPRINT",FACE,{"disambiguationData":[TD([[makeQuery(id+"F10.imprint","IMPRINT",EDGE,{"derivedFrom":subQ0}),1.0]])]});}
            var Q46;
            {var subQ0=sQuery(id+"F10.wireOp",EDGE,"E568");var subQ1=sQuery(id+"F10.wireOp",EDGE,"E567");var subQ2=makeQuery(id+"F10.imprint","INTERSECT",VERTEX,{"derivedFrom":[subQ1,subQ0]});Q46=makeQuery(id+"F10.imprint","IMPRINT",FACE,{"disambiguationData":[TD([[makeQuery(id+"F10.imprint","IMPRINT",EDGE,{"disambiguationData":[TD([[subQ2,1.0]])],"derivedFrom":subQ1}),-1.0]])]});}
            var Q47;
            Q47=makeQuery(id+"F10.imprint","IMPRINT",FACE,{"disambiguationData":[TD([[makeQuery(id+"F10.imprint","IMPRINT",EDGE,{"derivedFrom":sQuery(id+"F10.wireOp",EDGE,"E645")}),1.0]])]});
            var Q48;
            {var subQ0=sQuery(id+"F10.wireOp",EDGE,"E642");var subQ1=sQuery(id+"F10.wireOp",EDGE,"E541");var subQ2=makeQuery(id+"F10.imprint","INTERSECT",VERTEX,{"derivedFrom":[subQ1,subQ0]});Q48=makeQuery(id+"F10.imprint","IMPRINT",FACE,{"disambiguationData":[TD([[makeQuery(id+"F10.imprint","IMPRINT",EDGE,{"disambiguationData":[TD([[subQ2,-1.0]])],"derivedFrom":subQ1}),1.0]])]});}
            var Q49;
            {var subQ12=sQuery(id+"F10.wireOp",EDGE,"E684");Q49=makeQuery(id+"F10.imprint","IMPRINT",FACE,{"disambiguationData":[TD([[makeQuery(id+"F10.imprint","IMPRINT",EDGE,{"derivedFrom":subQ12}),1.0]])]});}
            var Q50;
            Q50=makeQuery(id+"F10.imprint","IMPRINT",FACE,{"disambiguationData":[TD([[makeQuery(id+"F10.imprint","IMPRINT",EDGE,{"derivedFrom":sQuery(id+"F10.wireOp",EDGE,"E663")}),1.0]])]});
            var Q51;
            {var subQ0=sQuery(id+"F10.wireOp",EDGE,"E681");var subQ1=sQuery(id+"F10.wireOp",EDGE,"E680");var subQ2=makeQuery(id+"F10.imprint","INTERSECT",VERTEX,{"derivedFrom":[subQ1,subQ0]});Q51=makeQuery(id+"F10.imprint","IMPRINT",FACE,{"disambiguationData":[TD([[makeQuery(id+"F10.imprint","IMPRINT",EDGE,{"disambiguationData":[TD([[subQ2,1.0]])],"derivedFrom":subQ1}),-1.0]])]});}
            var Q52;
            Q52=makeQuery(id+"F10.imprint","IMPRINT",FACE,{"disambiguationData":[TD([[makeQuery(id+"F10.imprint","IMPRINT",EDGE,{"derivedFrom":sQuery(id+"F10.wireOp",EDGE,"E732")}),1.0]])]});
            var Q53;
            {var subQ1=sQuery(id+"F10.wireOp",EDGE,"E784");Q53=makeQuery(id+"F10.imprint","IMPRINT",FACE,{"disambiguationData":[TD([[makeQuery(id+"F10.imprint","IMPRINT",EDGE,{"derivedFrom":subQ1}),-1.0]])]});}
            var Q54;
            {var subQ8=sQuery(id+"F10.wireOp",EDGE,"E678");Q54=makeQuery(id+"F10.imprint","IMPRINT",FACE,{"disambiguationData":[TD([[makeQuery(id+"F10.imprint","IMPRINT",EDGE,{"derivedFrom":subQ8}),1.0]])]});}
            var Q55;
            Q55=makeQuery(id+"F10.imprint","IMPRINT",FACE,{"disambiguationData":[TD([[makeQuery(id+"F10.imprint","IMPRINT",EDGE,{"derivedFrom":sQuery(id+"F10.wireOp",EDGE,"E742")}),1.0]])]});
            var Q56;
            Q56=makeQuery(id+"F10.imprint","IMPRINT",FACE,{"disambiguationData":[TD([[makeQuery(id+"F10.imprint","IMPRINT",EDGE,{"derivedFrom":sQuery(id+"F10.wireOp",EDGE,"E723")}),1.0]])]});
            var Q57;
            {var subQ4=sQuery(id+"F10.wireOp",EDGE,"E682");Q57=makeQuery(id+"F10.imprint","IMPRINT",FACE,{"disambiguationData":[TD([[makeQuery(id+"F10.imprint","IMPRINT",EDGE,{"derivedFrom":subQ4}),1.0]])]});}
            var Q58;
            {var subQ0=sQuery(id+"F10.wireOp",EDGE,"E775");Q58=makeQuery(id+"F10.imprint","IMPRINT",FACE,{"disambiguationData":[TD([[makeQuery(id+"F10.imprint","IMPRINT",EDGE,{"derivedFrom":subQ0}),-1.0]])]});}
            var Q59;
            {var subQ0=sQuery(id+"F10.wireOp",EDGE,"E711");var subQ1=sQuery(id+"F10.wireOp",EDGE,"E710");var subQ2=makeQuery(id+"F10.imprint","INTERSECT",VERTEX,{"derivedFrom":[subQ1,subQ0]});Q59=makeQuery(id+"F10.imprint","IMPRINT",FACE,{"disambiguationData":[TD([[makeQuery(id+"F10.imprint","IMPRINT",EDGE,{"disambiguationData":[TD([[subQ2,1.0]])],"derivedFrom":subQ1}),1.0]])]});}
            var Q60;
            {var subQ1=sQuery(id+"F10.wireOp",EDGE,"E767");Q60=makeQuery(id+"F10.imprint","IMPRINT",FACE,{"disambiguationData":[TD([[makeQuery(id+"F10.imprint","IMPRINT",EDGE,{"derivedFrom":subQ1}),-1.0]])]});}
            var Q61;
            Q61=makeQuery(id+"F10.imprint","IMPRINT",FACE,{"disambiguationData":[TD([[makeQuery(id+"F10.imprint","IMPRINT",EDGE,{"derivedFrom":sQuery(id+"F10.wireOp",EDGE,"E754")}),1.0]])]});
            var Q62;
            Q62=makeQuery(id+"F10.imprint","IMPRINT",FACE,{"disambiguationData":[TD([[makeQuery(id+"F10.imprint","IMPRINT",EDGE,{"derivedFrom":sQuery(id+"F10.wireOp",EDGE,"E789")}),-1.0]])]});
            var Q63;
            {var subQ1=sQuery(id+"F10.wireOp",EDGE,"E781");Q63=makeQuery(id+"F10.imprint","IMPRINT",FACE,{"disambiguationData":[TD([[makeQuery(id+"F10.imprint","IMPRINT",EDGE,{"derivedFrom":subQ1}),-1.0]])]});}
            var Q64;
            Q64=makeQuery(id+"F10.imprint","IMPRINT",FACE,{"disambiguationData":[TD([[makeQuery(id+"F10.imprint","IMPRINT",EDGE,{"derivedFrom":sQuery(id+"F10.wireOp",EDGE,"E700")}),1.0]])]});
            var Q65;
            Q65=makeQuery(id+"F10.imprint","IMPRINT",FACE,{"disambiguationData":[TD([[makeQuery(id+"F10.imprint","IMPRINT",EDGE,{"derivedFrom":sQuery(id+"F10.wireOp",EDGE,"E764")}),-1.0]])]});
            var Q66;
            {var subQ0=sQuery(id+"F10.wireOp",EDGE,"E800");Q66=makeQuery(id+"F10.imprint","IMPRINT",FACE,{"disambiguationData":[TD([[makeQuery(id+"F10.imprint","IMPRINT",EDGE,{"derivedFrom":subQ0}),-1.0]])]});}
            var Q67;
            {var subQ0=sQuery(id+"F10.wireOp",EDGE,"E773");Q67=makeQuery(id+"F10.imprint","IMPRINT",FACE,{"disambiguationData":[TD([[makeQuery(id+"F10.imprint","IMPRINT",EDGE,{"derivedFrom":subQ0}),-1.0]])]});}
            var Q68;
            {var subQ0=sQuery(id+"F10.wireOp",EDGE,"E786");var subQ1=sQuery(id+"F10.wireOp",EDGE,"E683");var subQ2=makeQuery(id+"F10.imprint","INTERSECT",VERTEX,{"derivedFrom":[subQ1,subQ0]});Q68=makeQuery(id+"F10.imprint","IMPRINT",FACE,{"disambiguationData":[TD([[makeQuery(id+"F10.imprint","IMPRINT",EDGE,{"disambiguationData":[TD([[subQ2,-1.0]])],"derivedFrom":subQ1}),-1.0]])]});}
            var Q69;
            {var subQ0=sQuery(id+"F10.wireOp",EDGE,"E798");var subQ1=sQuery(id+"F10.wireOp",EDGE,"E715");var subQ2=makeQuery(id+"F10.imprint","INTERSECT",VERTEX,{"derivedFrom":[subQ1,subQ0]});Q69=makeQuery(id+"F10.imprint","IMPRINT",FACE,{"disambiguationData":[TD([[makeQuery(id+"F10.imprint","IMPRINT",EDGE,{"disambiguationData":[TD([[subQ2,-1.0]])],"derivedFrom":subQ1}),1.0]])]});}
            extrude(context, id + "F12", {"entities" : qUnion([Q0, Q1, Q2, Q3, Q4, Q5, Q6, Q7, Q8, Q9, Q10, Q11, Q12, Q13, Q14, Q15, Q16, Q17, Q18, Q19, Q20, Q21, Q22, Q23, Q24, Q25, Q26, Q27, Q28, Q29, Q30, Q31, Q32, Q33, Q34, Q35, Q36, Q37, Q38, Q39, Q40, Q41, Q42, Q43, Q44, Q45, Q46, Q47, Q48, Q49, Q50, Q51, Q52, Q53, Q54, Q55, Q56, Q57, Q58, Q59, Q60, Q61, Q62, Q63, Q64, Q65, Q66, Q67, Q68, Q69]), "operationType" : NewBodyOperationType.ADD, "oppositeDirection" : true, "depth" : 2.5 * mm});
        }
        {
            var Q0;
            {var subQ4=sQuery(id+"F10.wireOp",EDGE,"E476");Q0=makeQuery(id+"F10.imprint","IMPRINT",FACE,{"disambiguationData":[TD([[makeQuery(id+"F10.imprint","IMPRINT",EDGE,{"derivedFrom":subQ4}),1.0]])]});}
            var Q1;
            {var subQ0=sQuery(id+"F10.wireOp",EDGE,"E470");Q1=makeQuery(id+"F10.imprint","IMPRINT",FACE,{"disambiguationData":[TD([[makeQuery(id+"F10.imprint","IMPRINT",EDGE,{"derivedFrom":subQ0}),1.0]])]});}
            var Q2;
            {var subQ0=sQuery(id+"F10.wireOp",EDGE,"E508");Q2=makeQuery(id+"F10.imprint","IMPRINT",FACE,{"disambiguationData":[TD([[makeQuery(id+"F10.imprint","IMPRINT",EDGE,{"derivedFrom":subQ0}),1.0]])]});}
            var Q3;
            Q3=makeQuery(id+"F10.imprint","IMPRINT",FACE,{"disambiguationData":[TD([[makeQuery(id+"F10.imprint","IMPRINT",EDGE,{"derivedFrom":sQuery(id+"F10.wireOp",EDGE,"E503")}),1.0]])]});
            var Q4;
            {var subQ0=sQuery(id+"F10.wireOp",EDGE,"E490");Q4=makeQuery(id+"F10.imprint","IMPRINT",FACE,{"disambiguationData":[TD([[makeQuery(id+"F10.imprint","IMPRINT",EDGE,{"derivedFrom":subQ0}),1.0]])]});}
            var Q5;
            Q5=makeQuery(id+"F10.imprint","IMPRINT",FACE,{"disambiguationData":[TD([[makeQuery(id+"F10.imprint","IMPRINT",EDGE,{"derivedFrom":sQuery(id+"F10.wireOp",EDGE,"E487")}),1.0]])]});
            var Q6;
            Q6=makeQuery(id+"F10.imprint","IMPRINT",FACE,{"disambiguationData":[TD([[makeQuery(id+"F10.imprint","IMPRINT",EDGE,{"derivedFrom":sQuery(id+"F10.wireOp",EDGE,"E455")}),1.0]])]});
            var Q7;
            Q7=makeQuery(id+"F10.imprint","IMPRINT",FACE,{"disambiguationData":[TD([[makeQuery(id+"F10.imprint","IMPRINT",EDGE,{"derivedFrom":sQuery(id+"F10.wireOp",EDGE,"E419")}),1.0]])]});
            var Q8;
            {var subQ5=sQuery(id+"F10.wireOp",EDGE,"E429");Q8=makeQuery(id+"F10.imprint","IMPRINT",FACE,{"disambiguationData":[TD([[makeQuery(id+"F10.imprint","IMPRINT",EDGE,{"derivedFrom":subQ5}),1.0]])]});}
            var Q9;
            Q9=makeQuery(id+"F10.imprint","IMPRINT",FACE,{"disambiguationData":[TD([[makeQuery(id+"F10.imprint","IMPRINT",EDGE,{"derivedFrom":sQuery(id+"F10.wireOp",EDGE,"E437")}),1.0]])]});
            var Q10;
            Q10=makeQuery(id+"F10.imprint","IMPRINT",FACE,{"disambiguationData":[TD([[makeQuery(id+"F10.imprint","IMPRINT",EDGE,{"derivedFrom":sQuery(id+"F10.wireOp",EDGE,"E321")}),1.0]])]});
            var Q11;
            {var subQ0=sQuery(id+"F10.wireOp",EDGE,"E342");Q11=makeQuery(id+"F10.imprint","IMPRINT",FACE,{"disambiguationData":[TD([[makeQuery(id+"F10.imprint","IMPRINT",EDGE,{"derivedFrom":subQ0}),1.0]])]});}
            var Q12;
            Q12=makeQuery(id+"F10.imprint","IMPRINT",FACE,{"disambiguationData":[TD([[makeQuery(id+"F10.imprint","IMPRINT",EDGE,{"derivedFrom":sQuery(id+"F10.wireOp",EDGE,"E338")}),1.0]])]});
            var Q13;
            Q13=makeQuery(id+"F10.imprint","IMPRINT",FACE,{"disambiguationData":[TD([[makeQuery(id+"F10.imprint","IMPRINT",EDGE,{"derivedFrom":sQuery(id+"F10.wireOp",EDGE,"E288")}),1.0]])]});
            var Q14;
            Q14=makeQuery(id+"F10.imprint","IMPRINT",FACE,{"disambiguationData":[TD([[makeQuery(id+"F10.imprint","IMPRINT",EDGE,{"derivedFrom":sQuery(id+"F10.wireOp",EDGE,"E307")}),1.0]])]});
            var Q15;
            Q15=makeQuery(id+"F10.imprint","IMPRINT",FACE,{"disambiguationData":[TD([[makeQuery(id+"F10.imprint","IMPRINT",EDGE,{"derivedFrom":sQuery(id+"F10.wireOp",EDGE,"E253")}),1.0]])]});
            var Q16;
            {var subQ0=sQuery(id+"F10.wireOp",EDGE,"E259");Q16=makeQuery(id+"F10.imprint","IMPRINT",FACE,{"disambiguationData":[TD([[makeQuery(id+"F10.imprint","IMPRINT",EDGE,{"derivedFrom":subQ0}),1.0]])]});}
            var Q17;
            Q17=makeQuery(id+"F10.imprint","IMPRINT",FACE,{"disambiguationData":[TD([[makeQuery(id+"F10.imprint","IMPRINT",EDGE,{"derivedFrom":sQuery(id+"F10.wireOp",EDGE,"E271")}),1.0]])]});
            var Q18;
            {var subQ6=sQuery(id+"F10.wireOp",EDGE,"E274");Q18=makeQuery(id+"F10.imprint","IMPRINT",FACE,{"disambiguationData":[TD([[makeQuery(id+"F10.imprint","IMPRINT",EDGE,{"derivedFrom":subQ6}),1.0]])]});}
            var Q19;
            Q19=makeQuery(id+"F10.imprint","IMPRINT",FACE,{"disambiguationData":[TD([[makeQuery(id+"F10.imprint","IMPRINT",EDGE,{"derivedFrom":sQuery(id+"F10.wireOp",EDGE,"E171")}),1.0]])]});
            var Q20;
            Q20=makeQuery(id+"F10.imprint","IMPRINT",FACE,{"disambiguationData":[TD([[makeQuery(id+"F10.imprint","IMPRINT",EDGE,{"derivedFrom":sQuery(id+"F10.wireOp",EDGE,"E153")}),1.0]])]});
            var Q21;
            {var subQ0=sQuery(id+"F10.wireOp",EDGE,"E163");Q21=makeQuery(id+"F10.imprint","IMPRINT",FACE,{"disambiguationData":[TD([[makeQuery(id+"F10.imprint","IMPRINT",EDGE,{"derivedFrom":subQ0}),1.0]])]});}
            var Q22;
            Q22=makeQuery(id+"F10.imprint","IMPRINT",FACE,{"disambiguationData":[TD([[makeQuery(id+"F10.imprint","IMPRINT",EDGE,{"derivedFrom":sQuery(id+"F10.wireOp",EDGE,"E120")}),1.0]])]});
            var Q23;
            Q23=makeQuery(id+"F10.imprint","IMPRINT",FACE,{"disambiguationData":[TD([[makeQuery(id+"F10.imprint","IMPRINT",EDGE,{"derivedFrom":sQuery(id+"F10.wireOp",EDGE,"E132")}),1.0]])]});
            var Q24;
            {var subQ0=sQuery(id+"F10.wireOp",EDGE,"E143");Q24=makeQuery(id+"F10.imprint","IMPRINT",FACE,{"disambiguationData":[TD([[makeQuery(id+"F10.imprint","IMPRINT",EDGE,{"derivedFrom":subQ0}),1.0]])]});}
            var Q25;
            {var subQ0=sQuery(id+"F10.wireOp",EDGE,"E86");Q25=makeQuery(id+"F10.imprint","IMPRINT",FACE,{"disambiguationData":[TD([[makeQuery(id+"F10.imprint","IMPRINT",EDGE,{"derivedFrom":subQ0}),1.0]])]});}
            var Q26;
            {var subQ0=sQuery(id+"F10.wireOp",EDGE,"E92");Q26=makeQuery(id+"F10.imprint","IMPRINT",FACE,{"disambiguationData":[TD([[makeQuery(id+"F10.imprint","IMPRINT",EDGE,{"derivedFrom":subQ0}),1.0]])]});}
            var Q27;
            Q27=makeQuery(id+"F10.imprint","IMPRINT",FACE,{"disambiguationData":[TD([[makeQuery(id+"F10.imprint","IMPRINT",EDGE,{"derivedFrom":sQuery(id+"F10.wireOp",EDGE,"E104")}),1.0]])]});
            var Q28;
            Q28=makeQuery(id+"F10.imprint","IMPRINT",FACE,{"disambiguationData":[TD([[makeQuery(id+"F10.imprint","IMPRINT",EDGE,{"derivedFrom":sQuery(id+"F10.wireOp",EDGE,"E663")}),1.0]])]});
            var Q29;
            {var subQ12=sQuery(id+"F10.wireOp",EDGE,"E684");Q29=makeQuery(id+"F10.imprint","IMPRINT",FACE,{"disambiguationData":[TD([[makeQuery(id+"F10.imprint","IMPRINT",EDGE,{"derivedFrom":subQ12}),1.0]])]});}
            var Q30;
            {var subQ4=sQuery(id+"F10.wireOp",EDGE,"E682");Q30=makeQuery(id+"F10.imprint","IMPRINT",FACE,{"disambiguationData":[TD([[makeQuery(id+"F10.imprint","IMPRINT",EDGE,{"derivedFrom":subQ4}),1.0]])]});}
            var Q31;
            {var subQ8=sQuery(id+"F10.wireOp",EDGE,"E678");Q31=makeQuery(id+"F10.imprint","IMPRINT",FACE,{"disambiguationData":[TD([[makeQuery(id+"F10.imprint","IMPRINT",EDGE,{"derivedFrom":subQ8}),1.0]])]});}
            var Q32;
            Q32=makeQuery(id+"F10.imprint","IMPRINT",FACE,{"disambiguationData":[TD([[makeQuery(id+"F10.imprint","IMPRINT",EDGE,{"derivedFrom":sQuery(id+"F10.wireOp",EDGE,"E521")}),-1.0]])]});
            var Q33;
            {var subQ10=sQuery(id+"F10.wireOp",EDGE,"E542");Q33=makeQuery(id+"F10.imprint","IMPRINT",FACE,{"disambiguationData":[TD([[makeQuery(id+"F10.imprint","IMPRINT",EDGE,{"derivedFrom":subQ10}),-1.0]])]});}
            var Q34;
            {var subQ10=sQuery(id+"F10.wireOp",EDGE,"E540");Q34=makeQuery(id+"F10.imprint","IMPRINT",FACE,{"disambiguationData":[TD([[makeQuery(id+"F10.imprint","IMPRINT",EDGE,{"derivedFrom":subQ10}),-1.0]])]});}
            var Q35;
            {var subQ4=sQuery(id+"F10.wireOp",EDGE,"E536");Q35=makeQuery(id+"F10.imprint","IMPRINT",FACE,{"disambiguationData":[TD([[makeQuery(id+"F10.imprint","IMPRINT",EDGE,{"derivedFrom":subQ4}),-1.0]])]});}
            extrude(context, id + "F13", {"entities" : qUnion([Q0, Q1, Q2, Q3, Q4, Q5, Q6, Q7, Q8, Q9, Q10, Q11, Q12, Q13, Q14, Q15, Q16, Q17, Q18, Q19, Q20, Q21, Q22, Q23, Q24, Q25, Q26, Q27, Q28, Q29, Q30, Q31, Q32, Q33, Q34, Q35]), "operationType" : NewBodyOperationType.ADD, "depth" : 2.5 * mm});
        }
        {
            var Q0;
            Q0=makeQuery(id+"F10.imprint","IMPRINT",FACE,{"disambiguationData":[TD([[makeQuery(id+"F10.imprint","IMPRINT",EDGE,{"derivedFrom":sQuery(id+"F10.wireOp",EDGE,"E557")}),-1.0]])]});
            var Q1;
            {var subQ0=sQuery(id+"F10.wireOp",EDGE,"E656");Q1=makeQuery(id+"F10.imprint","IMPRINT",FACE,{"disambiguationData":[TD([[makeQuery(id+"F10.imprint","IMPRINT",EDGE,{"derivedFrom":subQ0}),1.0]])]});}
            var Q2;
            Q2=makeQuery(id+"F10.imprint","IMPRINT",FACE,{"disambiguationData":[TD([[makeQuery(id+"F10.imprint","IMPRINT",EDGE,{"derivedFrom":sQuery(id+"F10.wireOp",EDGE,"E611")}),-1.0]])]});
            var Q3;
            Q3=makeQuery(id+"F10.imprint","IMPRINT",FACE,{"disambiguationData":[TD([[makeQuery(id+"F10.imprint","IMPRINT",EDGE,{"derivedFrom":sQuery(id+"F10.wireOp",EDGE,"E645")}),1.0]])]});
            var Q4;
            {var subQ0=sQuery(id+"F10.wireOp",EDGE,"E648");Q4=makeQuery(id+"F10.imprint","IMPRINT",FACE,{"disambiguationData":[TD([[makeQuery(id+"F10.imprint","IMPRINT",EDGE,{"derivedFrom":subQ0}),1.0]])]});}
            var Q5;
            {var subQ0=sQuery(id+"F10.wireOp",EDGE,"E639");Q5=makeQuery(id+"F10.imprint","IMPRINT",FACE,{"disambiguationData":[TD([[makeQuery(id+"F10.imprint","IMPRINT",EDGE,{"derivedFrom":subQ0}),1.0]])]});}
            var Q6;
            {var subQ0=sQuery(id+"F10.wireOp",EDGE,"E637");Q6=makeQuery(id+"F10.imprint","IMPRINT",FACE,{"disambiguationData":[TD([[makeQuery(id+"F10.imprint","IMPRINT",EDGE,{"derivedFrom":subQ0}),1.0]])]});}
            var Q7;
            Q7=makeQuery(id+"F10.imprint","IMPRINT",FACE,{"disambiguationData":[TD([[makeQuery(id+"F10.imprint","IMPRINT",EDGE,{"derivedFrom":sQuery(id+"F10.wireOp",EDGE,"E599")}),-1.0]])]});
            var Q8;
            Q8=makeQuery(id+"F10.imprint","IMPRINT",FACE,{"disambiguationData":[TD([[makeQuery(id+"F10.imprint","IMPRINT",EDGE,{"derivedFrom":sQuery(id+"F10.wireOp",EDGE,"E589")}),-1.0]])]});
            var Q9;
            Q9=makeQuery(id+"F10.imprint","IMPRINT",FACE,{"disambiguationData":[TD([[makeQuery(id+"F10.imprint","IMPRINT",EDGE,{"derivedFrom":sQuery(id+"F10.wireOp",EDGE,"E629")}),1.0]])]});
            var Q10;
            {var subQ0=sQuery(id+"F10.wireOp",EDGE,"E621");Q10=makeQuery(id+"F10.imprint","IMPRINT",FACE,{"disambiguationData":[TD([[makeQuery(id+"F10.imprint","IMPRINT",EDGE,{"derivedFrom":subQ0}),1.0]])]});}
            var Q11;
            {var subQ0=sQuery(id+"F10.wireOp",EDGE,"E623");Q11=makeQuery(id+"F10.imprint","IMPRINT",FACE,{"disambiguationData":[TD([[makeQuery(id+"F10.imprint","IMPRINT",EDGE,{"derivedFrom":subQ0}),1.0]])]});}
            var Q12;
            Q12=makeQuery(id+"F10.imprint","IMPRINT",FACE,{"disambiguationData":[TD([[makeQuery(id+"F10.imprint","IMPRINT",EDGE,{"derivedFrom":sQuery(id+"F10.wireOp",EDGE,"E580")}),-1.0]])]});
            var Q13;
            Q13=makeQuery(id+"F10.imprint","IMPRINT",FACE,{"disambiguationData":[TD([[makeQuery(id+"F10.imprint","IMPRINT",EDGE,{"derivedFrom":sQuery(id+"F10.wireOp",EDGE,"E700")}),1.0]])]});
            var Q14;
            Q14=makeQuery(id+"F10.imprint","IMPRINT",FACE,{"disambiguationData":[TD([[makeQuery(id+"F10.imprint","IMPRINT",EDGE,{"derivedFrom":sQuery(id+"F10.wireOp",EDGE,"E723")}),1.0]])]});
            var Q15;
            Q15=makeQuery(id+"F10.imprint","IMPRINT",FACE,{"disambiguationData":[TD([[makeQuery(id+"F10.imprint","IMPRINT",EDGE,{"derivedFrom":sQuery(id+"F10.wireOp",EDGE,"E764")}),-1.0]])]});
            var Q16;
            {var subQ1=sQuery(id+"F10.wireOp",EDGE,"E767");Q16=makeQuery(id+"F10.imprint","IMPRINT",FACE,{"disambiguationData":[TD([[makeQuery(id+"F10.imprint","IMPRINT",EDGE,{"derivedFrom":subQ1}),-1.0]])]});}
            var Q17;
            Q17=makeQuery(id+"F10.imprint","IMPRINT",FACE,{"disambiguationData":[TD([[makeQuery(id+"F10.imprint","IMPRINT",EDGE,{"derivedFrom":sQuery(id+"F10.wireOp",EDGE,"E732")}),1.0]])]});
            var Q18;
            {var subQ0=sQuery(id+"F10.wireOp",EDGE,"E773");Q18=makeQuery(id+"F10.imprint","IMPRINT",FACE,{"disambiguationData":[TD([[makeQuery(id+"F10.imprint","IMPRINT",EDGE,{"derivedFrom":subQ0}),-1.0]])]});}
            var Q19;
            {var subQ0=sQuery(id+"F10.wireOp",EDGE,"E775");Q19=makeQuery(id+"F10.imprint","IMPRINT",FACE,{"disambiguationData":[TD([[makeQuery(id+"F10.imprint","IMPRINT",EDGE,{"derivedFrom":subQ0}),-1.0]])]});}
            var Q20;
            {var subQ1=sQuery(id+"F10.wireOp",EDGE,"E781");Q20=makeQuery(id+"F10.imprint","IMPRINT",FACE,{"disambiguationData":[TD([[makeQuery(id+"F10.imprint","IMPRINT",EDGE,{"derivedFrom":subQ1}),-1.0]])]});}
            var Q21;
            {var subQ1=sQuery(id+"F10.wireOp",EDGE,"E784");Q21=makeQuery(id+"F10.imprint","IMPRINT",FACE,{"disambiguationData":[TD([[makeQuery(id+"F10.imprint","IMPRINT",EDGE,{"derivedFrom":subQ1}),-1.0]])]});}
            var Q22;
            Q22=makeQuery(id+"F10.imprint","IMPRINT",FACE,{"disambiguationData":[TD([[makeQuery(id+"F10.imprint","IMPRINT",EDGE,{"derivedFrom":sQuery(id+"F10.wireOp",EDGE,"E742")}),1.0]])]});
            var Q23;
            Q23=makeQuery(id+"F10.imprint","IMPRINT",FACE,{"disambiguationData":[TD([[makeQuery(id+"F10.imprint","IMPRINT",EDGE,{"derivedFrom":sQuery(id+"F10.wireOp",EDGE,"E789")}),-1.0]])]});
            var Q24;
            Q24=makeQuery(id+"F10.imprint","IMPRINT",FACE,{"disambiguationData":[TD([[makeQuery(id+"F10.imprint","IMPRINT",EDGE,{"derivedFrom":sQuery(id+"F10.wireOp",EDGE,"E754")}),1.0]])]});
            var Q25;
            {var subQ0=sQuery(id+"F10.wireOp",EDGE,"E800");Q25=makeQuery(id+"F10.imprint","IMPRINT",FACE,{"disambiguationData":[TD([[makeQuery(id+"F10.imprint","IMPRINT",EDGE,{"derivedFrom":subQ0}),-1.0]])]});}
            extrude(context, id + "F14", {"entities" : qUnion([Q0, Q1, Q2, Q3, Q4, Q5, Q6, Q7, Q8, Q9, Q10, Q11, Q12, Q13, Q14, Q15, Q16, Q17, Q18, Q19, Q20, Q21, Q22, Q23, Q24, Q25]), "operationType" : NewBodyOperationType.ADD, "depth" : 2 * mm});
        }
    });
